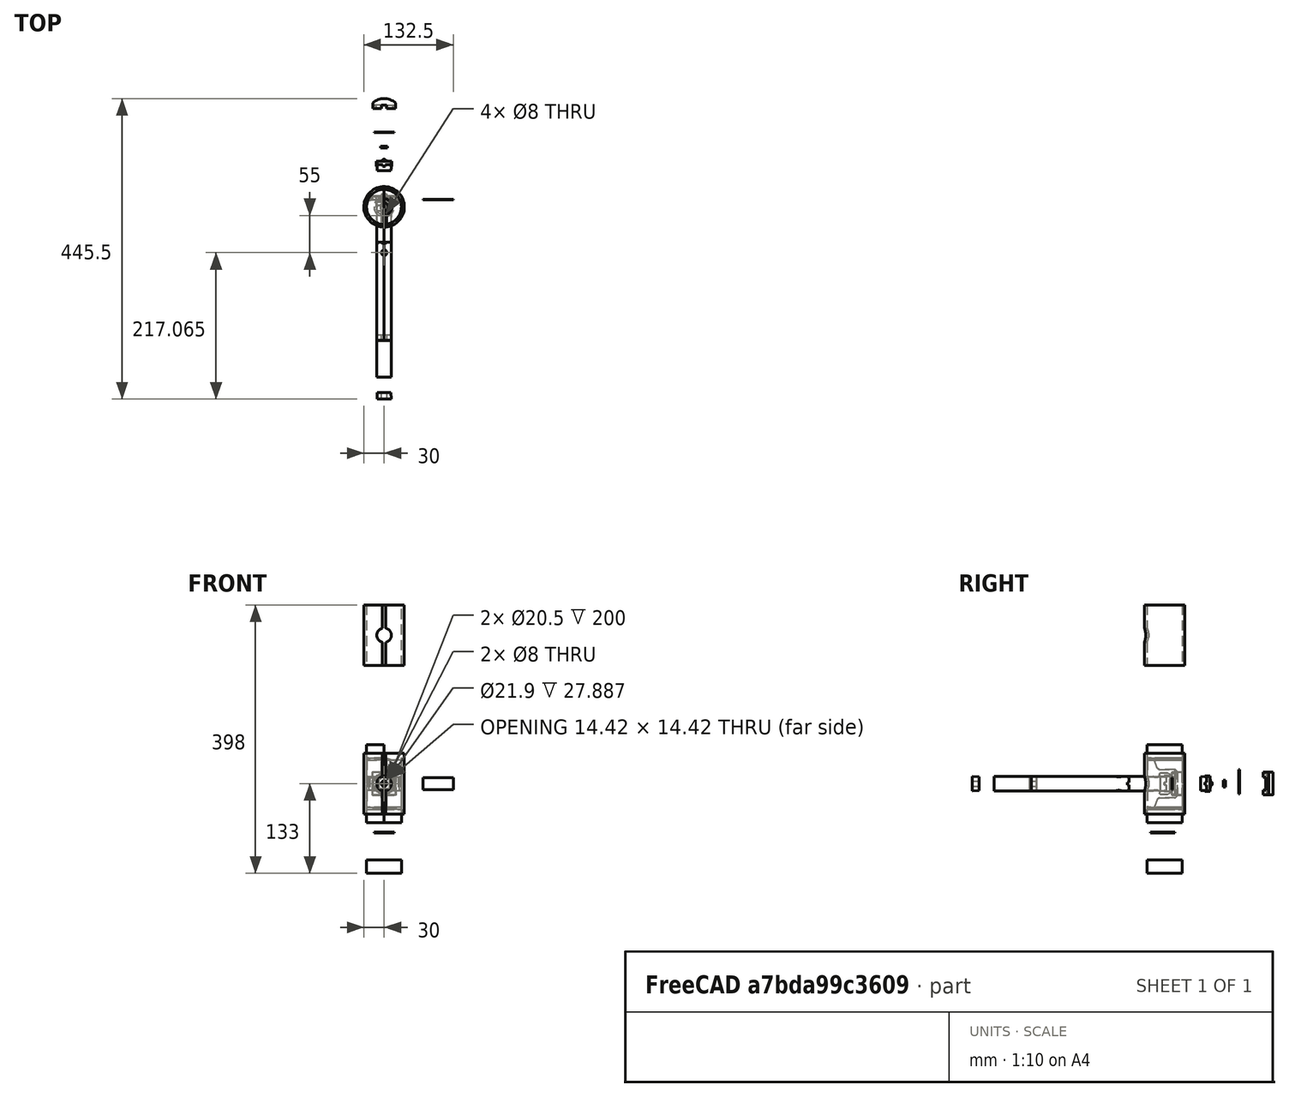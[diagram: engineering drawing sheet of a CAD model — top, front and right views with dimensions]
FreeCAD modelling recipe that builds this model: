
FCSTD DOCUMENT  (FreeCAD 0.21R33771 (Git))
Label: Hammer
License: All rights reserved
LicenseURL: https://en.wikipedia.org/wiki/All_rights_reserved
objects: Sketcher::SketchObject×52, PartDesign::Pad×26, PartDesign::Pocket×26, PartDesign::Body×26, TechDraw::DrawViewDimension×19, TechDraw::DrawProjGroupItem×18, PartDesign::Chamfer×14, App::Link×13, App::DocumentObjectGroupPython×13, Part::Feature×12, TechDraw::DrawViewBalloon×12, TechDraw::DrawSVGTemplate×7, TechDraw::DrawProjGroup×7, TechDraw::DrawPage×7, PartDesign::FeatureBase×6, PartDesign::AdditiveCone×4, PartDesign::Fillet×4, Spreadsheet::Sheet×3, App::DocumentObjectGroup×3, PartDesign::Draft×2, +6 more types
note: 276 computed .brp shape members not serialized (recipe doc carries the construction recipe); baked Part::Feature solids carry a one-line shape summary decoded from their .brp

FEATURE [Spreadsheet::Sheet] Spreadsheet  label="Properties"
  cells = A1='PropertyName; B1='Value; A2='Handle_OD; B2(Handle_OD)=21.5; A3='Head_ID; B3(Head_ID)=51.4; A4='Head_Len; B4(Handle_Len)=110; A5='Clearance; B5(Clearance)=0.2; A6='Inset_Len; B6(Insert_Len)=70; A7='Sensor_Wire_Track_Width; B7(Sensor_Wire_Track_Width)=8; A8='Spring_Plate_Len; B8(Spring_Plate_Len)=46; A9='Sensor_Diameter; B9(Sensor_Diameter)=30; A10='Handle_ID; B10(Handle_ID)=20.5
FEATURE [Sketcher::SketchObject] Sketch  label="base"
  FullyConstrained = true
  MapMode = 5
  Support = -> [XY_Plane001]
  expr: Constraints[1] = <<Properties>>.Head_ID
  sketch-geometry (1):
    g0: Circle CenterX=0 CenterY=0 CenterZ=0 NormalX=0 NormalY=0 NormalZ=1 AngleXU=0 Radius=25.7
  constraints (2):
    c: Coincident(g0,g-1)
    c: Diameter(g0) = 51.4
FEATURE [PartDesign::Pad] Pad  label="Base"
  Direction = (0,0,1)
  Length = 35
  Length2 = 35
  Profile = -> Sketch
  ReferenceAxis = -> Sketch [N_Axis]
  Type = 4
  expr: Length = <<Properties>>.Insert_Len / 2
  expr: Length2 = <<Properties>>.Insert_Len / 2
FEATURE [Sketcher::SketchObject] Sketch001  label="sensor_wire_slot"
  FullyConstrained = true
  MapMode = 5
  Support = -> [XY_Plane001]
  expr: Constraints[11] = <<Properties>>.Sensor_Wire_Track_Width
  expr: Constraints[1] = Sketch.Constraints[1]
  sketch-geometry (7):
    g0: Circle CenterX=0 CenterY=0 CenterZ=0 NormalX=0 NormalY=0 NormalZ=1 AngleXU=0 Radius=25.7
    g1: LineSegment StartX=-4 StartY=-25.3868 StartZ=0 EndX=-4 EndY=-14.4568 EndZ=0
    g2: LineSegment StartX=-4 StartY=-14.4568 StartZ=0 EndX=4 EndY=-14.4568 EndZ=0
    g3: LineSegment StartX=4 StartY=-14.4568 StartZ=0 EndX=4 EndY=-25.3868 EndZ=0
    g4: ArcOfCircle CenterX=0 CenterY=0 CenterZ=0 NormalX=0 NormalY=0 NormalZ=1 AngleXU=0 Radius=25.7 StartAngle=4.55611 EndAngle=4.86867
    g5: GeomPoint X=0 Y=-14.4568 Z=0
    g6: Circle CenterX=0 CenterY=0 CenterZ=0 NormalX=0 NormalY=0 NormalZ=1 AngleXU=0 Radius=15
  constraints (17):
    c: Coincident(g0,g-1)
    c: Diameter(g0) = 51.4
    c: Vertical(g1)
    c: Coincident(g2,g1)
    c: Horizontal(g2)
    c: Coincident(g3,g2)
    c: Vertical(g3)
    c: Coincident(g4,g0)
    c: Coincident(g4,g1)
    c: Coincident(g4,g3)
    c: PointOnObject(g3,g0)
    c: DistanceX(g2,g2) = 8
    c: Symmetric(g2,g2,g5)
    c: PointOnObject(g5,g-2)
    c: Coincident(g6,g4)
    c: Diameter(g6) = 30
    c: PointOnObject(g2,g6)
FEATURE [PartDesign::Pocket] Pocket  label="Sensor_Wire_Slot"
  BaseFeature = -> Pad
  Direction = (0,0,-1)
  Length = 35
  Length2 = 35
  Profile = -> Sketch001
  ReferenceAxis = -> Sketch001 [N_Axis]
  Type = 4
  expr: Length = <<Properties>>.Insert_Len / 2
  expr: Length2 = <<Properties>>.Insert_Len / 2
FEATURE [Sketcher::SketchObject] Sketch002  label="handle_hole"
  FullyConstrained = true
  MapMode = 5
  Placement = pos=(0,0,0) rot=(1,0,0;1.5708rad)
  Support = -> [XZ_Plane001]
  expr: Constraints[1] = <<Properties>>.Handle_OD + <<Properties>>.Clearance * 2
  sketch-geometry (1):
    g0: Circle CenterX=0 CenterY=0 CenterZ=0 NormalX=0 NormalY=0 NormalZ=1 AngleXU=0 Radius=10.95
  constraints (2):
    c: Coincident(g0,g-1)
    c: Diameter(g0) = 21.9
FEATURE [PartDesign::Pocket] Pocket001  label="Handle_hole"
  BaseFeature = -> Pocket
  Direction = (0,1,2e-16)
  Length = 25.7
  Length2 = 25.7
  Profile = -> Sketch002
  ReferenceAxis = -> Sketch002 [N_Axis]
  Type = 4
  expr: Length = <<Properties>>.Head_ID / 2
  expr: Length2 = <<Properties>>.Head_ID / 2
FEATURE [Sketcher::SketchObject] Sketch004  label="top_sensor_hole"
  FullyConstrained = true
  MapMode = 5
  Placement = pos=(0,0,0) rot=(0.57735,0.57735,0.57735;2.0944rad)
  Support = -> [YZ_Plane001]
  expr: Constraints[20] = <<Properties>>.Head_ID
  expr: Constraints[7] = <<Properties>>.Sensor_Diameter + 4
  sketch-geometry (9):
    g0: LineSegment StartX=-25.7 StartY=-17 StartZ=0 EndX=-25.7 EndY=17 EndZ=0
    g1: LineSegment StartX=25.7 StartY=17 StartZ=0 EndX=25.7 EndY=-17 EndZ=0
    g2: LineSegment StartX=25.7 StartY=-17 StartZ=0 EndX=-25.7 EndY=-17 EndZ=0
    g3: GeomPoint X=0 Y=0 Z=0
    g4: LineSegment StartX=10.5 StartY=17 StartZ=0 EndX=25.7 EndY=17 EndZ=0
    g5: LineSegment StartX=25.7 StartY=17 StartZ=0 EndX=25.7 EndY=-17 EndZ=0
    g6: LineSegment StartX=25.7 StartY=-17 StartZ=0 EndX=10.5 EndY=-17 EndZ=0
    g7: LineSegment StartX=10.5 StartY=-17 StartZ=0 EndX=10.5 EndY=17 EndZ=0
    g8: LineSegment StartX=-25.7 StartY=17 StartZ=0 EndX=25.7 EndY=17 EndZ=0
  constraints (23):
    c: Coincident(g1,g2)
    c: Coincident(g2,g0)
    c: Horizontal(g2)
    c: Vertical(g0)
    c: Vertical(g1)
    c: Symmetric(g1,g0,g3)
    c: Coincident(g3,g-1)
    c: DistanceY(g1,g1) = 34
    c: Coincident(g4,g5)
    c: Coincident(g5,g6)
    c: Coincident(g6,g7)
    c: Horizontal(g4)
    c: Horizontal(g6)
    c: Vertical(g5)
    c: Vertical(g7)
    c: PointOnObject(g5,g2)
    c: Coincident(g7,g4)
    c: Coincident(g8,g0)
    c: Coincident(g8,g1)
    c: Horizontal(g8)
    c: DistanceX(g8,g8) = 51.4
    c: Coincident(g4,g1)
    c: DistanceX(g3,g4) = 10.5
FEATURE [PartDesign::Pocket] Pocket002  label="Top_Sensor_Hole"
  BaseFeature = -> Pocket001
  Direction = (-1,2e-16,-3e-16)
  Length = 17
  Length2 = 17
  Profile = -> Sketch004
  ReferenceAxis = -> Sketch004 [N_Axis]
  Type = 4
  expr: Length = <<Properties>>.Sensor_Diameter / 2 + 2
  expr: Length2 = <<Properties>>.Sensor_Diameter / 2 + 2
FEATURE [PartDesign::Chamfer] Chamfer
  Angle = 70
  Base = -> Pocket002 [Edge30,Edge32]
  BaseFeature = -> Pocket002
  ChamferType = 2
  FlipDirection = false
  Size = 8
  Size2 = 1
  SupportTransform = false
  UseAllEdges = false
FEATURE [Sketcher::SketchObject] Sketch003  label="spring_plate_slot"
  FullyConstrained = true
  MapMode = 5
  Support = -> [XY_Plane001]
  expr: Constraints[1] = Sketch.Constraints[1]
  expr: Constraints[3] = <<Properties>>.Sensor_Diameter + <<Properties>>.Clearance * 2
  expr: Constraints[7] = <<Properties>>.Spring_Plate_Len
  sketch-geometry (15):
    g0: Circle CenterX=0 CenterY=0 CenterZ=0 NormalX=0 NormalY=0 NormalZ=1 AngleXU=0 Radius=25.7
    g1: LineSegment StartX=-15.2 StartY=15.4669 StartZ=0 EndX=15.2 EndY=15.4669 EndZ=0
    g2: GeomPoint X=0 Y=15.4669 Z=0
    g3: LineSegment StartX=-23 StartY=11.4669 StartZ=0 EndX=23 EndY=11.4669 EndZ=0
    g4: GeomPoint X=0 Y=11.4669 Z=0
    g5: LineSegment StartX=-15.2 StartY=15.4669 StartZ=0 EndX=-21 EndY=11.4669 EndZ=0
    g6: LineSegment StartX=15.2 StartY=15.4669 StartZ=0 EndX=21 EndY=11.4669 EndZ=0
    g7: LineSegment StartX=21 StartY=11.4669 StartZ=0 EndX=23 EndY=11.4669 EndZ=0
    g8: LineSegment StartX=-21 StartY=11.4669 StartZ=0 EndX=-23 EndY=11.4669 EndZ=0
    g9: ArcOfCircle CenterX=0 CenterY=0 CenterZ=0 NormalX=0 NormalY=0 NormalZ=1 AngleXU=0 Radius=25.7 StartAngle=2.6791 EndAngle=2.80587
    g10: ArcOfCircle CenterX=0 CenterY=0 CenterZ=0 NormalX=0 NormalY=0 NormalZ=1 AngleXU=0 Radius=25.7 StartAngle=0.335723 EndAngle=0.462496
    g11: LineSegment StartX=-11 StartY=10.5 StartZ=0 EndX=-24.2652 EndY=8.46691 EndZ=0
    g12: LineSegment StartX=11 StartY=10.5 StartZ=0 EndX=24.2652 EndY=8.46691 EndZ=0
    g13: LineSegment StartX=11 StartY=10.5 StartZ=0 EndX=-11 EndY=10.5 EndZ=0
    g14: GeomPoint X=0 Y=10.5 Z=0
  constraints (39):
    c: Coincident(g0,g-1)
    c: Diameter(g0) = 51.4
    c: Horizontal(g1)
    c: DistanceX(g1,g1) = 30.4
    c: Symmetric(g1,g1,g2)
    c: PointOnObject(g2,g-2)
    c: Horizontal(g3)
    c: DistanceX(g3,g3) = 46
    c: Symmetric(g3,g3,g4)
    c: PointOnObject(g4,g-2)
    c: Coincident(g5,g1)
    c: PointOnObject(g5,g3)
    c: Coincident(g6,g1)
    c: PointOnObject(g6,g3)
    c: Coincident(g7,g6)
    c: PointOnObject(g7,g0)
    c: Horizontal(g7)
    c: Coincident(g8,g5)
    c: PointOnObject(g8,g0)
    c: Horizontal(g8)
    c: Equal(g8,g7)
    c: PointOnObject(g3,g0)
    c: DistanceY(g6,g1) = 4
    c: DistanceX(g6,g7) = 2
    c: Coincident(g9,g0)
    c: Coincident(g9,g8)
    c: Coincident(g10,g9)
    c: Coincident(g10,g7)
    c: Coincident(g13,g12)
    c: Coincident(g13,g11)
    c: Horizontal(g13)
    c: Coincident(g10,g12)
    c: Coincident(g9,g11)
    c: DistanceX(g12,g6) = 10
    c: Equal(g12,g11)
    c: DistanceY(g10,g7) = 3
    c: Symmetric(g13,g13,g14)
    c: PointOnObject(g14,g-2)
    c: DistanceY(g9,g14) = 10.5
FEATURE [PartDesign::Pocket] Pocket003  label="Spring_Plate_Slot"
  BaseFeature = -> Chamfer
  Direction = (0,0,-1)
  Length = 10
  Length2 = 10
  Profile = -> Sketch003
  ReferenceAxis = -> Sketch003 [N_Axis]
  Type = 4
FEATURE [PartDesign::Chamfer] Chamfer001
  Angle = 45
  Base = -> Pocket003 [Edge43,Edge46,Edge45,Edge47,Edge44,Edge42]
  BaseFeature = -> Pocket003
  ChamferType = 0
  FlipDirection = false
  Size = 0.5
  Size2 = 1
  SupportTransform = false
  UseAllEdges = false
FEATURE [Sketcher::SketchObject] Sketch005  label="top_sens_base"
  FullyConstrained = true
  MapMode = 5
  Support = -> [XY_Plane]
  expr: Constraints[18] = <<Properties>>.Clearance
  expr: Constraints[1] = <<Properties>>.Head_ID
  expr: Constraints[3] = 34 - <<Properties>>.Clearance * 2
  expr: Constraints[6] = 10.5 + <<Properties>>.Clearance
  sketch-geometry (8):
    g0: Circle CenterX=0 CenterY=0 CenterZ=0 NormalX=0 NormalY=0 NormalZ=1 AngleXU=0 Radius=25.7
    g1: LineSegment StartX=-16.8 StartY=10.7 StartZ=0 EndX=16.8 EndY=10.7 EndZ=0
    g2: GeomPoint X=0 Y=10.7 Z=0
    g3: LineSegment StartX=-16.8 StartY=10.7 StartZ=0 EndX=-16.8 EndY=19.1836 EndZ=0
    g4: LineSegment StartX=16.8 StartY=10.7 StartZ=0 EndX=16.8 EndY=19.1836 EndZ=0
    g5: GeomPoint X=0 Y=25.7 Z=0
    g6: ArcOfCircle CenterX=0 CenterY=0 CenterZ=0 NormalX=0 NormalY=0 NormalZ=1 AngleXU=0 Radius=25.5 StartAngle=0.851542 EndAngle=2.29005
    g7: GeomPoint X=0 Y=25.5 Z=0
  constraints (19):
    c: Coincident(g0,g-1)
    c: Diameter(g0) = 51.4
    c: Horizontal(g1)
    c: DistanceX(g1,g1) = 33.6
    c: Symmetric(g1,g1,g2)
    c: PointOnObject(g2,g-2)
    c: DistanceY(g0,g2) = 10.7
    c: Coincident(g3,g1)
    c: Vertical(g3)
    c: Vertical(g4)
    c: Coincident(g4,g1)
    c: PointOnObject(g5,g0)
    c: PointOnObject(g5,g-2)
    c: Coincident(g6,g0)
    c: Coincident(g6,g3)
    c: Coincident(g6,g4)
    c: PointOnObject(g7,g6)
    c: PointOnObject(g7,g-2)
    c: DistanceY(g7,g5) = 0.2
FEATURE [PartDesign::Pad] Pad001  label="Top_Base"
  Direction = (0,0,1)
  Length = 16.8
  Length2 = 16.8
  Profile = -> Sketch005
  ReferenceAxis = -> Sketch005 [N_Axis]
  Type = 4
  expr: Length = <<Properties>>.Sensor_Diameter / 2 + 2 - <<Properties>>.Clearance
  expr: Length2 = <<Properties>>.Sensor_Diameter / 2 + 2 - <<Properties>>.Clearance
FEATURE [Sketcher::SketchObject] Sketch006
  FullyConstrained = true
  MapMode = 5
  Support = -> [XY_Plane]
  expr: Constraints[1] = Sketch003.Constraints[1]
  expr: Constraints[22] = Sketch003.Constraints[22]
  expr: Constraints[23] = Sketch003.Constraints[23]
  expr: Constraints[33] = Sketch003.Constraints[33]
  expr: Constraints[35] = Sketch003.Constraints[35]
  expr: Constraints[38] = Sketch003.Constraints[38]
  expr: Constraints[3] = Sketch003.Constraints[3]
  expr: Constraints[7] = Sketch003.Constraints[7]
  sketch-geometry (15):
    g0: Circle CenterX=0 CenterY=0 CenterZ=0 NormalX=0 NormalY=0 NormalZ=1 AngleXU=0 Radius=25.7
    g1: LineSegment StartX=-15.2 StartY=15.4669 StartZ=0 EndX=15.2 EndY=15.4669 EndZ=0
    g2: GeomPoint X=0 Y=15.4669 Z=0
    g3: LineSegment StartX=-23 StartY=11.4669 StartZ=0 EndX=23 EndY=11.4669 EndZ=0
    g4: GeomPoint X=0 Y=11.4669 Z=0
    g5: LineSegment StartX=-15.2 StartY=15.4669 StartZ=0 EndX=-21 EndY=11.4669 EndZ=0
    g6: LineSegment StartX=15.2 StartY=15.4669 StartZ=0 EndX=21 EndY=11.4669 EndZ=0
    g7: LineSegment StartX=21 StartY=11.4669 StartZ=0 EndX=23 EndY=11.4669 EndZ=0
    g8: LineSegment StartX=-21 StartY=11.4669 StartZ=0 EndX=-23 EndY=11.4669 EndZ=0
    g9: ArcOfCircle CenterX=0 CenterY=0 CenterZ=0 NormalX=0 NormalY=0 NormalZ=1 AngleXU=0 Radius=25.7 StartAngle=2.6791 EndAngle=2.80587
    g10: ArcOfCircle CenterX=0 CenterY=0 CenterZ=0 NormalX=0 NormalY=0 NormalZ=1 AngleXU=0 Radius=25.7 StartAngle=0.335723 EndAngle=0.462496
    g11: LineSegment StartX=-11 StartY=10.5 StartZ=0 EndX=-24.2652 EndY=8.46691 EndZ=0
    g12: LineSegment StartX=11 StartY=10.5 StartZ=0 EndX=24.2652 EndY=8.46691 EndZ=0
    g13: LineSegment StartX=11 StartY=10.5 StartZ=0 EndX=-11 EndY=10.5 EndZ=0
    g14: GeomPoint X=0 Y=10.5 Z=0
  constraints (40):
    c: Coincident(g0,g-1)
    c: Diameter(g0) = 51.4
    c: Horizontal(g1)
    c: DistanceX(g1,g1) = 30.4
    c: Symmetric(g1,g1,g2)
    c: PointOnObject(g2,g-2)
    c: Horizontal(g3)
    c: DistanceX(g3,g3) = 46
    c: Symmetric(g3,g3,g4)
    c: PointOnObject(g4,g-2)
    c: Coincident(g5,g1)
    c: PointOnObject(g5,g3)
    c: Coincident(g6,g1)
    c: PointOnObject(g6,g3)
    c: Coincident(g7,g6)
    c: PointOnObject(g7,g0)
    c: Horizontal(g7)
    c: Coincident(g8,g5)
    c: PointOnObject(g8,g0)
    c: Horizontal(g8)
    c: Equal(g8,g7)
    c: PointOnObject(g3,g0)
    c: DistanceY(g6,g1) = 4
    c: DistanceX(g6,g7) = 2
    c: Coincident(g9,g0)
    c: Coincident(g9,g8)
    c: Coincident(g10,g9)
    c: Coincident(g10,g7)
    c: Coincident(g13,g12)
    c: Coincident(g13,g11)
    c: Horizontal(g13)
    c: Coincident(g10,g12)
    c: Coincident(g9,g11)
    c: DistanceX(g12,g6) = 10
    c: Equal(g12,g11)
    c: DistanceY(g10,g7) = 3
    c: Symmetric(g13,g13,g14)
    c: PointOnObject(g14,g-2)
    c: DistanceY(g9,g14) = 10.5
    c: DistanceY(g9,g2) = 15.4669
FEATURE [PartDesign::Pocket] Pocket004
  BaseFeature = -> Pad001
  Direction = (0,0,-1)
  Length = 9.5
  Length2 = 9.5
  Profile = -> Sketch006
  ReferenceAxis = -> Sketch006 [N_Axis]
  Type = 4
FEATURE [PartDesign::Chamfer] Chamfer002
  Angle = 45
  Base = -> Pocket004 [Edge22,Edge12]
  BaseFeature = -> Pocket004
  ChamferType = 0
  FlipDirection = false
  Size = 0.3
  Size2 = 1
  SupportTransform = false
  UseAllEdges = false
FEATURE [Sketcher::SketchObject] Sketch007
  FullyConstrained = true
  MapMode = 5
  Placement = pos=(0,0,0) rot=(1,0,0;1.5708rad)
  Support = -> [XZ_Plane]
  expr: Constraints[11] = <<Properties>>.Sensor_Wire_Track_Width
  expr: Constraints[1] = <<Properties>>.Sensor_Diameter + 1
  expr: Constraints[27] = <<Properties>>.Sensor_Wire_Track_Width
  sketch-geometry (11):
    g0: Circle CenterX=0 CenterY=0 CenterZ=0 NormalX=0 NormalY=0 NormalZ=1 AngleXU=0 Radius=15.5
    g1: LineSegment StartX=-4 StartY=14.975 StartZ=0 EndX=-4 EndY=27.305 EndZ=0
    g2: LineSegment StartX=-4 StartY=27.305 StartZ=0 EndX=4 EndY=27.305 EndZ=0
    g3: LineSegment StartX=4 StartY=27.305 StartZ=0 EndX=4 EndY=14.975 EndZ=0
    g4: GeomPoint X=0 Y=27.305 Z=0
    g5: LineSegment StartX=-4 StartY=-14.975 StartZ=0 EndX=-4 EndY=-27.305 EndZ=0
    g6: LineSegment StartX=-4 StartY=-27.305 StartZ=0 EndX=4 EndY=-27.305 EndZ=0
    g7: LineSegment StartX=4 StartY=-27.305 StartZ=0 EndX=4 EndY=-14.975 EndZ=0
    g8: GeomPoint X=0 Y=-27.305 Z=0
    g9: ArcOfCircle CenterX=0 CenterY=0 CenterZ=0 NormalX=0 NormalY=0 NormalZ=1 AngleXU=0 Radius=15.5 StartAngle=1.83181 EndAngle=4.45137
    g10: ArcOfCircle CenterX=0 CenterY=0 CenterZ=0 NormalX=0 NormalY=0 NormalZ=1 AngleXU=0 Radius=15.5 StartAngle=4.97341 EndAngle=7.59296
  constraints (28):
    c: Coincident(g0,g-1)
    c: Diameter(g0) = 31
    c: PointOnObject(g1,g0)
    c: Vertical(g1)
    c: Coincident(g2,g1)
    c: Horizontal(g2)
    c: Coincident(g3,g2)
    c: PointOnObject(g3,g0)
    c: Vertical(g3)
    c: Symmetric(g2,g2,g4)
    c: PointOnObject(g4,g-2)
    c: DistanceX(g2,g2) = 8
    c: DistanceY(g3,g3) = 12.33
    c: Vertical(g5)
    c: Coincident(g6,g5)
    c: Horizontal(g6)
    c: Coincident(g7,g6)
    c: Vertical(g7)
    c: Symmetric(g6,g6,g8)
    c: PointOnObject(g8,g-2)
    c: Equal(g7,g3)
    c: Coincident(g9,g0)
    c: Coincident(g9,g1)
    c: Coincident(g9,g5)
    c: Coincident(g10,g9)
    c: Coincident(g10,g3)
    c: Coincident(g10,g7)
    c: DistanceX(g6,g6) = 8
FEATURE [PartDesign::Pocket] Pocket005
  BaseFeature = -> Chamfer002
  Direction = (0,1,2e-16)
  Length = 0
  Length2 = 5
  Offset = 0.4
  Profile = -> Sketch007
  ReferenceAxis = -> Sketch007 [N_Axis]
  Type = 3
  UpToFace = -> Chamfer002 [Face11]
FEATURE [PartDesign::Body] Body001  label="TopSensor"
  Group = -> [Sketch005,Pad001,Sketch006,Pocket004,Chamfer002,Sketch007,Pocket005]
  Origin = -> Origin
  Tip = -> Pocket005
FEATURE [Sketcher::SketchObject] Sketch008
  FullyConstrained = true
  MapMode = 5
  Placement = pos=(0,0,0) rot=(0.57735,0.57735,0.57735;2.0944rad)
  Support = -> [YZ_Plane001]
  expr: Constraints[16] = <<Properties>>.Sensor_Diameter + 2
  sketch-geometry (14):
    g0: LineSegment StartX=15.5 StartY=21 StartZ=0 EndX=15.5 EndY=-21 EndZ=0
    g1: LineSegment StartX=15.5 StartY=-21 StartZ=0 EndX=-19.02 EndY=-21 EndZ=0
    g2: LineSegment StartX=-19.02 StartY=-21 StartZ=0 EndX=-19.02 EndY=-16 EndZ=0
    g3: LineSegment StartX=-19.02 StartY=-16 StartZ=0 EndX=10.5 EndY=-16 EndZ=0
    g4: LineSegment StartX=10.5 StartY=-16 StartZ=0 EndX=10.5 EndY=16 EndZ=0
    g5: LineSegment StartX=10.5 StartY=16 StartZ=0 EndX=-19.02 EndY=16 EndZ=0
    g6: LineSegment StartX=-19.02 StartY=16 StartZ=0 EndX=-19.02 EndY=21 EndZ=0
    g7: LineSegment StartX=-19.02 StartY=21 StartZ=0 EndX=15.5 EndY=21 EndZ=0
    g8: GeomPoint X=10.5 Y=0 Z=0
    g9: GeomPoint X=15.5 Y=0 Z=0
    g10: GeomPoint X=15.5 Y=21 Z=0
    g11: GeomPoint X=15.5 Y=-21 Z=0
    g12: GeomPoint X=10.5 Y=16 Z=0
    g13: GeomPoint X=10.5 Y=-16 Z=0
  constraints (30):
    c: Vertical(g0)
    c: Horizontal(g1)
    c: Coincident(g2,g1)
    c: Vertical(g2)
    c: Coincident(g3,g2)
    c: Horizontal(g3)
    c: Vertical(g4)
    c: Horizontal(g5)
    c: Coincident(g6,g5)
    c: Vertical(g6)
    c: Coincident(g7,g6)
    c: Horizontal(g7)
    c: Symmetric(g10,g11,g9)
    c: Symmetric(g13,g12,g8)
    c: PointOnObject(g8,g-1)
    c: PointOnObject(g9,g-1)
    c: DistanceY(g13,g12) = 32
    c: DistanceY(g6,g6) = 5
    c: DistanceX(g8,g9) = 5
    c: DistanceX(g-1,g8) = 10.5
    c: DistanceX(g7,g10) = 34.52
    c: Coincident(g0,g10)
    c: Coincident(g7,g0)
    c: Coincident(g4,g12)
    c: Coincident(g5,g4)
    c: Coincident(g0,g11)
    c: Coincident(g4,g13)
    c: Coincident(g3,g4)
    c: Coincident(g1,g0)
    c: Equal(g3,g5)
FEATURE [PartDesign::Pocket] Pocket006
  BaseFeature = -> Chamfer001
  Direction = (-1,2e-16,-3e-16)
  Length = 4
  Length2 = 4
  Profile = -> Sketch008
  ReferenceAxis = -> Sketch008 [N_Axis]
  Type = 4
  expr: Length = <<Properties>>.Sensor_Wire_Track_Width / 2
  expr: Length2 = <<Properties>>.Sensor_Wire_Track_Width / 2
FEATURE [PartDesign::Chamfer] Chamfer003
  Angle = 65
  Base = -> Pocket006 [Edge148,Edge154]
  BaseFeature = -> Pocket006
  ChamferType = 2
  FlipDirection = false
  Size = 3
  Size2 = 1
  SupportTransform = false
  UseAllEdges = false
FEATURE [PartDesign::Chamfer] Chamfer004
  Angle = 45
  Base = -> Chamfer003 [Edge167,Edge85,Edge52,Edge56]
  BaseFeature = -> Chamfer003
  ChamferType = 0
  FlipDirection = false
  Size = 2
  Size2 = 1
  SupportTransform = false
  UseAllEdges = false
FEATURE [PartDesign::Chamfer] Chamfer005
  Angle = 45
  Base = -> Chamfer004 [Edge169,Edge38]
  BaseFeature = -> Chamfer004
  ChamferType = 1
  FlipDirection = false
  Size = 4
  Size2 = 3.999
  SupportTransform = false
  UseAllEdges = false
FEATURE [Sketcher::SketchObject] Sketch009
  FullyConstrained = true
  MapMode = 5
  Support = -> [XY_Plane002]
  sketch-geometry (2):
    g0: Circle CenterX=0 CenterY=0 CenterZ=0 NormalX=0 NormalY=0 NormalZ=1 AngleXU=0 Radius=26
    g1: Circle CenterX=0 CenterY=0 CenterZ=0 NormalX=0 NormalY=0 NormalZ=1 AngleXU=0 Radius=30
  constraints (4):
    c: Coincident(g0,g-1)
    c: Coincident(g1,g0)
    c: Diameter(g0) = 52
    c: Diameter(g1) = 60
FEATURE [PartDesign::Pad] Pad002
  Direction = (0,0,1)
  Length = 45
  Length2 = 45
  Profile = -> Sketch009
  ReferenceAxis = -> Sketch009 [N_Axis]
  Type = 4
FEATURE [Sketcher::SketchObject] Sketch010
  FullyConstrained = true
  MapMode = 5
  Placement = pos=(0,0,0) rot=(1,0,0;1.5708rad)
  Support = -> [XZ_Plane002]
  expr: Constraints[1] = <<Properties>>.Handle_OD
  sketch-geometry (1):
    g0: Circle CenterX=0 CenterY=0 CenterZ=0 NormalX=0 NormalY=0 NormalZ=1 AngleXU=0 Radius=10.75
  constraints (2):
    c: Coincident(g0,g-1)
    c: Diameter(g0) = 21.5
FEATURE [PartDesign::Pocket] Pocket007
  BaseFeature = -> Pad002
  Direction = (0,1,2e-16)
  Length = 5
  Length2 = 5
  Profile = -> Sketch010
  ReferenceAxis = -> Sketch010 [N_Axis]
  Reversed = true
  Type = 1
FEATURE [Sketcher::SketchObject] Sketch011
  FullyConstrained = true
  MapMode = 5
  Placement = pos=(0,0,0) rot=(1,0,0;1.5708rad)
  Support = -> [XZ_Plane003]
  expr: Constraints[3] = <<Properties>>.Handle_ID
  sketch-geometry (2):
    g0: Circle CenterX=0 CenterY=0 CenterZ=0 NormalX=0 NormalY=0 NormalZ=1 AngleXU=0 Radius=10.625
    g1: Circle CenterX=0 CenterY=0 CenterZ=0 NormalX=0 NormalY=0 NormalZ=1 AngleXU=0 Radius=10.25
  constraints (4):
    c: Coincident(g0,g-1)
    c: Diameter(g0) = 21.25
    c: Coincident(g1,g0)
    c: Diameter(g1) = 20.5
FEATURE [PartDesign::Pad] Pad003
  Direction = (0,-1,-2e-16)
  Length = 200
  Length2 = 10
  Placement = pos=(0,0,0) rot=(1,0,0;1.5708rad)
  Profile = -> Sketch011
  ReferenceAxis = -> Sketch011 [N_Axis]
  Type = 0
FEATURE [Sketcher::SketchObject] Sketch014
  FullyConstrained = true
  MapMode = 5
  Support = -> [XY_Plane005]
  sketch-geometry (5):
    g0: ArcOfCircle CenterX=0 CenterY=0 CenterZ=0 NormalX=0 NormalY=0 NormalZ=1 AngleXU=0 Radius=15 StartAngle=4.90695 EndAngle=10.801
    g1: LineSegment StartX=2.9 StartY=-14.717 StartZ=0 EndX=2.9 EndY=-20.717 EndZ=0
    g2: LineSegment StartX=2.9 StartY=-20.717 StartZ=0 EndX=-2.9 EndY=-20.717 EndZ=0
    g3: LineSegment StartX=-2.9 StartY=-20.717 StartZ=0 EndX=-2.9 EndY=-14.717 EndZ=0
    g4: LineSegment StartX=2.9 StartY=-14.717 StartZ=0 EndX=-2.9 EndY=-14.717 EndZ=0
  constraints (14):
    c: Coincident(g0,g-1)
    c: Radius(g0) = 15
    c: Coincident(g1,g0)
    c: Vertical(g1)
    c: Coincident(g2,g1)
    c: Horizontal(g2)
    c: Coincident(g3,g2)
    c: Coincident(g3,g0)
    c: Vertical(g3)
    c: DistanceX(g2,g2) = 5.8
    c: Coincident(g4,g0)
    c: Coincident(g4,g0)
    c: Horizontal(g4)
    c: DistanceY(g1,g1) = 6
FEATURE [PartDesign::Pad] Pad007
  Direction = (0,0,1)
  Length = 1
  Length2 = 10
  Profile = -> Sketch014
  ReferenceAxis = -> Sketch014 [N_Axis]
  Type = 0
FEATURE [PartDesign::Body] Body005  label="Sensor1"
  Group = -> [Sketch014,Pad007]
  Origin = -> Origin005
  Placement = pos=(0,0,37) rot=(0,0,1;0rad)
  Tip = -> Pad007
FEATURE [PartDesign::FeatureBase] Clone
  BaseFeature = -> Body005
FEATURE [PartDesign::Body] Body006  label="Sensor2"
  Group = -> [Clone]
  Origin = -> Origin006
  Placement = pos=(0,0,-37) rot=(0,1,0;3.14159rad)
  Tip = -> Clone
FEATURE [PartDesign::FeatureBase] Clone001
  BaseFeature = -> Body005
FEATURE [PartDesign::Body] Body007  label="Sensor3"
  Group = -> [Clone001]
  Origin = -> Origin007
  Placement = pos=(0,16,-4e-15) rot=(0,0.707107,-0.707107;3.14159rad)
  Tip = -> Clone001
FEATURE [PartDesign::AdditiveCone] Cone
  Angle = 360
  AttacherType = Attacher::AttachEngine3D
  BaseFeature = -> Chamfer005
  Height = 1.5
  MapMode = 5
  Placement = pos=(0,0,35) rot=(0,0,1;0rad)
  Radius1 = 12
  Radius2 = 6
  Support = -> [Chamfer005]
FEATURE [PartDesign::AdditiveCone] Cone001
  Angle = 360
  AttacherType = Attacher::AttachEngine3D
  BaseFeature = -> Cone
  Height = 1.5
  MapMode = 5
  Placement = pos=(0,0,-35) rot=(1,0,0;3.14159rad)
  Radius1 = 12
  Radius2 = 6
  Support = -> [Cone]
FEATURE [Sketcher::SketchObject] Sketch015
  FullyConstrained = true
  MapMode = 5
  Support = -> [XY_Plane008]
  sketch-geometry (1):
    g0: Circle CenterX=0 CenterY=0 CenterZ=0 NormalX=0 NormalY=0 NormalZ=1 AngleXU=0 Radius=26
  constraints (2):
    c: Coincident(g0,g-1)
    c: Diameter(g0) = 52
FEATURE [PartDesign::Pad] Pad008
  Direction = (0,0,1)
  Length = 20
  Length2 = 10
  Profile = -> Sketch015
  ReferenceAxis = -> Sketch015 [N_Axis]
  Type = 0
FEATURE [PartDesign::Body] Body008  label="Foam1"
  Group = -> [Sketch015,Pad008]
  Origin = -> Origin008
  Placement = pos=(0,0,38) rot=(0,0,1;0rad)
  Tip = -> Pad008
FEATURE [PartDesign::FeatureBase] Clone002
  BaseFeature = -> Body008
  Placement = pos=(0,0,38) rot=(0,0,1;0rad)
FEATURE [PartDesign::Body] Body009  label="Foam2"
  Group = -> [Clone002]
  Origin = -> Origin009
  Placement = pos=(0,0,0) rot=(1,0,0;3.14159rad)
  Tip = -> Clone002
FEATURE [Sketcher::SketchObject] Sketch016
  FullyConstrained = true
  MapMode = 5
  Support = -> [XY_Plane010]
  sketch-geometry (5):
    g0: LineSegment StartX=-22.5 StartY=-0.4 StartZ=0 EndX=-22.5 EndY=0.4 EndZ=0
    g1: LineSegment StartX=-22.5 StartY=0.4 StartZ=0 EndX=22.5 EndY=0.4 EndZ=0
    g2: LineSegment StartX=22.5 StartY=0.4 StartZ=0 EndX=22.5 EndY=-0.4 EndZ=0
    g3: LineSegment StartX=22.5 StartY=-0.4 StartZ=0 EndX=-22.5 EndY=-0.4 EndZ=0
    g4: GeomPoint X=0 Y=0 Z=0
  constraints (12):
    c: Coincident(g0,g1)
    c: Coincident(g1,g2)
    c: Coincident(g2,g3)
    c: Coincident(g3,g0)
    c: Horizontal(g1)
    c: Horizontal(g3)
    c: Vertical(g0)
    c: Vertical(g2)
    c: Symmetric(g1,g0,g4)
    c: Coincident(g4,g-1)
    c: DistanceX(g1,g1) = 45
    c: DistanceY(g2,g2) = 0.8
FEATURE [PartDesign::Pad] Pad009
  Direction = (0,0,1)
  Length = 9
  Length2 = 9
  Profile = -> Sketch016
  ReferenceAxis = -> Sketch016 [N_Axis]
  Type = 4
FEATURE [PartDesign::Body] Body010  label="ShimStock"
  Group = -> [Sketch016,Pad009]
  Origin = -> Origin010
  Placement = pos=(0,11,0) rot=(0,0,1;0rad)
  Tip = -> Pad009
FEATURE [Sketcher::SketchObject] Sketch017
  FullyConstrained = true
  MapMode = 5
  Placement = pos=(0,0,0) rot=(1,0,0;1.5708rad)
  Support = -> [XZ_Plane011]
  sketch-geometry (1):
    g0: Circle CenterX=0 CenterY=0 CenterZ=0 NormalX=0 NormalY=0 NormalZ=1 AngleXU=0 Radius=5
  constraints (2):
    c: Coincident(g0,g-1)
    c: Diameter(g0) = 10
FEATURE [PartDesign::Pad] Pad010
  Direction = (0,-1,-2e-16)
  Length = 3
  Length2 = 10
  Placement = pos=(0,0,0) rot=(1,0,0;1.5708rad)
  Profile = -> Sketch017
  ReferenceAxis = -> Sketch017 [N_Axis]
  Type = 0
FEATURE [PartDesign::Body] Body011  label="TopFoam"
  Group = -> [Sketch017,Pad010]
  Origin = -> Origin011
  Placement = pos=(0,15,0) rot=(0,0,1;0rad)
  Tip = -> Pad010
FEATURE [Sketcher::SketchObject] Sketch018
  FullyConstrained = false
  MapMode = 5
  Support = -> [XY_Plane003]
  sketch-geometry (1):
    g0: Circle CenterX=0 CenterY=-15.4348 CenterZ=0 NormalX=0 NormalY=0 NormalZ=1 AngleXU=0 Radius=4
  constraints (2):
    c: PointOnObject(g0,g-2)
    c: Diameter(g0) = 8
FEATURE [PartDesign::Pocket] Pocket008
  BaseFeature = -> Pad003
  Direction = (0,0,-1)
  Length = 50
  Length2 = 50
  Placement = pos=(0,0,0) rot=(1,0,0;1.5708rad)
  Profile = -> Sketch018
  ReferenceAxis = -> Sketch018 [N_Axis]
  Type = 4
FEATURE [Sketcher::SketchObject] Sketch019
  FullyConstrained = true
  MapMode = 5
  Placement = pos=(0,0,0) rot=(1,0,0;1.5708rad)
  Support = -> [XZ_Plane003]
  sketch-geometry (17):
    g0: LineSegment StartX=12 StartY=-2 StartZ=0 EndX=12 EndY=2 EndZ=0
    g1: LineSegment StartX=12 StartY=2 StartZ=0 EndX=2 EndY=2 EndZ=0
    g2: LineSegment StartX=2 StartY=2 StartZ=0 EndX=2 EndY=12 EndZ=0
    g3: LineSegment StartX=2 StartY=12 StartZ=0 EndX=-2 EndY=12 EndZ=0
    g4: LineSegment StartX=-2 StartY=12 StartZ=0 EndX=-2 EndY=2 EndZ=0
    g5: LineSegment StartX=-2 StartY=2 StartZ=0 EndX=-12 EndY=2 EndZ=0
    g6: LineSegment StartX=-12 StartY=2 StartZ=0 EndX=-12 EndY=-2 EndZ=0
    g7: LineSegment StartX=-12 StartY=-2 StartZ=0 EndX=-2 EndY=-2 EndZ=0
    g8: LineSegment StartX=-2 StartY=-2 StartZ=0 EndX=-2 EndY=-12 EndZ=0
    g9: LineSegment StartX=-2 StartY=-12 StartZ=0 EndX=2 EndY=-12 EndZ=0
    g10: LineSegment StartX=2 StartY=-12 StartZ=0 EndX=2 EndY=-2 EndZ=0
    g11: LineSegment StartX=2 StartY=-2 StartZ=0 EndX=12 EndY=-2 EndZ=0
    g12: LineSegment StartX=-2 StartY=-2 StartZ=0 EndX=-2 EndY=2 EndZ=0
    g13: LineSegment StartX=-2 StartY=2 StartZ=0 EndX=2 EndY=2 EndZ=0
    g14: LineSegment StartX=2 StartY=2 StartZ=0 EndX=2 EndY=-2 EndZ=0
    g15: LineSegment StartX=2 StartY=-2 StartZ=0 EndX=-2 EndY=-2 EndZ=0
    g16: GeomPoint X=0 Y=0 Z=0
  constraints (46):
    c: Vertical(g0)
    c: Coincident(g1,g0)
    c: Horizontal(g1)
    c: Coincident(g2,g1)
    c: Vertical(g2)
    c: Coincident(g3,g2)
    c: Horizontal(g3)
    c: Coincident(g4,g3)
    c: Vertical(g4)
    c: Coincident(g5,g4)
    c: Horizontal(g5)
    c: Coincident(g6,g5)
    c: Vertical(g6)
    c: Horizontal(g7)
    c: Coincident(g8,g7)
    c: Vertical(g8)
    c: Horizontal(g9)
    c: Coincident(g10,g9)
    c: Vertical(g10)
    c: Coincident(g11,g10)
    c: Coincident(g11,g0)
    c: Horizontal(g11)
    c: Equal(g0,g3)
    c: Equal(g3,g6)
    c: Equal(g6,g9)
    c: Coincident(g6,g7)
    c: Coincident(g9,g8)
    c: Equal(g11,g7)
    c: Equal(g11,g1)
    c: Equal(g2,g4)
    c: Equal(g5,g10)
    c: Coincident(g12,g13)
    c: Coincident(g13,g14)
    c: Coincident(g14,g15)
    c: Coincident(g15,g12)
    c: Horizontal(g13)
    c: Horizontal(g15)
    c: Vertical(g12)
    c: Vertical(g14)
    c: Symmetric(g13,g12,g16)
    c: Coincident(g16,g-1)
    c: Coincident(g13,g1)
    c: Coincident(g7,g12)
    c: DistanceX(g13,g13) = 4
    c: DistanceY(g2,g2) = 10
    c: Equal(g10,g2)
FEATURE [PartDesign::Pocket] Pocket009
  BaseFeature = -> Pocket008
  Direction = (0,1,2e-16)
  Length = 3
  Length2 = 5
  Placement = pos=(0,0,0) rot=(1,0,0;1.5708rad)
  Profile = -> Sketch019
  ReferenceAxis = -> Sketch019 [N_Axis]
  Reversed = true
  Type = 0
FEATURE [PartDesign::Body] Body003  label="MetalHandle"
  Group = -> [Sketch011,Pad003,Sketch018,Pocket008,Sketch019,Pocket009]
  Origin = -> Origin003
  Placement = pos=(0,2.5,0) rot=(0,0,1;0rad)
  Tip = -> Pocket009
FEATURE [Sketcher::SketchObject] Sketch020
  FullyConstrained = true
  MapMode = 5
  Placement = pos=(0,0,0) rot=(1,0,0;1.5708rad)
  Support = -> [XZ_Plane012]
  expr: Constraints[43] = Sketch019.Constraints[43]
  expr: Constraints[44] = Sketch019.Constraints[44]
  expr: Constraints[77] = <<Properties>>.Clearance
  expr: Constraints[78] = <<Properties>>.Clearance
  expr: Constraints[79] = <<Properties>>.Clearance
  expr: Constraints[81] = (<<Properties>>.Handle_OD + 2) / 2 - <<Properties>>.Clearance
  sketch-geometry (29):
    g0: LineSegment StartX=12 StartY=-2 StartZ=0 EndX=12 EndY=2 EndZ=0
    g1: LineSegment StartX=12 StartY=2 StartZ=0 EndX=2 EndY=2 EndZ=0
    g2: LineSegment StartX=2 StartY=2 StartZ=0 EndX=2 EndY=12 EndZ=0
    g3: LineSegment StartX=2 StartY=12 StartZ=0 EndX=-2 EndY=12 EndZ=0
    g4: LineSegment StartX=-2 StartY=12 StartZ=0 EndX=-2 EndY=2 EndZ=0
    g5: LineSegment StartX=-2 StartY=2 StartZ=0 EndX=-12 EndY=2 EndZ=0
    g6: LineSegment StartX=-12 StartY=2 StartZ=0 EndX=-12 EndY=-2 EndZ=0
    g7: LineSegment StartX=-12 StartY=-2 StartZ=0 EndX=-2 EndY=-2 EndZ=0
    g8: LineSegment StartX=-2 StartY=-2 StartZ=0 EndX=-2 EndY=-12 EndZ=0
    g9: LineSegment StartX=-2 StartY=-12 StartZ=0 EndX=2 EndY=-12 EndZ=0
    g10: LineSegment StartX=2 StartY=-12 StartZ=0 EndX=2 EndY=-2 EndZ=0
    g11: LineSegment StartX=2 StartY=-2 StartZ=0 EndX=12 EndY=-2 EndZ=0
    g12: LineSegment StartX=-2 StartY=-2 StartZ=0 EndX=-2 EndY=2 EndZ=0
    g13: LineSegment StartX=-2 StartY=2 StartZ=0 EndX=2 EndY=2 EndZ=0
    g14: LineSegment StartX=2 StartY=2 StartZ=0 EndX=2 EndY=-2 EndZ=0
    g15: LineSegment StartX=2 StartY=-2 StartZ=0 EndX=-2 EndY=-2 EndZ=0
    g16: GeomPoint X=0 Y=0 Z=0
    g17: LineSegment StartX=-1.8 StartY=11.55 StartZ=0 EndX=-1.8 EndY=1.8 EndZ=0
    g18: LineSegment StartX=-1.8 StartY=1.8 StartZ=0 EndX=-11.55 EndY=1.8 EndZ=0
    g19: LineSegment StartX=-11.55 StartY=1.8 StartZ=0 EndX=-11.55 EndY=-1.8 EndZ=0
    g20: LineSegment StartX=-11.55 StartY=-1.8 StartZ=0 EndX=-1.8 EndY=-1.8 EndZ=0
    g21: LineSegment StartX=-1.8 StartY=-1.8 StartZ=0 EndX=-1.8 EndY=-11.55 EndZ=0
    g22: LineSegment StartX=-1.8 StartY=-11.55 StartZ=0 EndX=1.8 EndY=-11.55 EndZ=0
    g23: LineSegment StartX=1.8 StartY=-11.55 StartZ=0 EndX=1.8 EndY=-1.8 EndZ=0
    g24: LineSegment StartX=1.8 StartY=-1.8 StartZ=0 EndX=11.55 EndY=-1.8 EndZ=0
    g25: LineSegment StartX=11.55 StartY=-1.8 StartZ=0 EndX=11.55 EndY=1.8 EndZ=0
    g26: LineSegment StartX=11.55 StartY=1.8 StartZ=0 EndX=1.8 EndY=1.8 EndZ=0
    g27: LineSegment StartX=1.8 StartY=1.8 StartZ=0 EndX=1.8 EndY=11.55 EndZ=0
    g28: LineSegment StartX=1.8 StartY=11.55 StartZ=0 EndX=-1.8 EndY=11.55 EndZ=0
  constraints (82):
    c: Vertical(g0)
    c: Coincident(g1,g0)
    c: Horizontal(g1)
    c: Coincident(g2,g1)
    c: Vertical(g2)
    c: Coincident(g3,g2)
    c: Horizontal(g3)
    c: Coincident(g4,g3)
    c: Vertical(g4)
    c: Coincident(g5,g4)
    c: Horizontal(g5)
    c: Coincident(g6,g5)
    c: Vertical(g6)
    c: Horizontal(g7)
    c: Coincident(g8,g7)
    c: Vertical(g8)
    c: Horizontal(g9)
    c: Coincident(g10,g9)
    c: Vertical(g10)
    c: Coincident(g11,g10)
    c: Coincident(g11,g0)
    c: Horizontal(g11)
    c: Equal(g0,g3)
    c: Equal(g3,g6)
    c: Equal(g6,g9)
    c: Coincident(g6,g7)
    c: Coincident(g9,g8)
    c: Equal(g11,g7)
    c: Equal(g11,g1)
    c: Equal(g2,g4)
    c: Equal(g5,g10)
    c: Coincident(g12,g13)
    c: Coincident(g13,g14)
    c: Coincident(g14,g15)
    c: Coincident(g15,g12)
    c: Horizontal(g13)
    c: Horizontal(g15)
    c: Vertical(g12)
    c: Vertical(g14)
    c: Symmetric(g13,g12,g16)
    c: Coincident(g16,g-1)
    c: Coincident(g13,g1)
    c: Coincident(g7,g12)
    c: DistanceX(g13,g13) = 4
    c: DistanceY(g2,g2) = 10
    c: Equal(g10,g2)
    c: Vertical(g17)
    c: Coincident(g18,g17)
    c: Horizontal(g18)
    c: Coincident(g19,g18)
    c: Vertical(g19)
    c: Coincident(g20,g19)
    c: Horizontal(g20)
    c: Coincident(g21,g20)
    c: Vertical(g21)
    c: Coincident(g22,g21)
    c: Horizontal(g22)
    c: Coincident(g23,g22)
    c: Vertical(g23)
    c: Coincident(g24,g23)
    c: Horizontal(g24)
    c: Coincident(g25,g24)
    c: Vertical(g25)
    c: Coincident(g26,g25)
    c: Horizontal(g26)
    c: Coincident(g27,g26)
    c: Vertical(g27)
    c: Coincident(g28,g27)
    c: Coincident(g28,g17)
    c: Horizontal(g28)
    c: Equal(g26,g18)
    c: Equal(g27,g17)
    c: Equal(g26,g24)
    c: Equal(g20,g24)
    c: Equal(g21,g23)
    c: Equal(g23,g27)
    c: Equal(g22,g25)
    c: DistanceX(g26,g1) = 0.2
    c: DistanceY(g26,g1) = 0.2
    c: DistanceY(g0,g24) = 0.2
    c: Equal(g23,g24)
    c: DistanceX(g16,g25) = 11.55
FEATURE [PartDesign::Pad] Pad011
  Direction = (0,-1,2e-16)
  Length = 2.8
  Length2 = 10
  Placement = pos=(0,0,0) rot=(1,0,0;1.5708rad)
  Profile = -> Sketch020
  ReferenceAxis = -> Sketch020 [N_Axis]
  Type = 0
FEATURE [Sketcher::SketchObject] Sketch021
  FullyConstrained = true
  MapMode = 5
  Placement = pos=(0,0,0) rot=(1,0,0;1.5708rad)
  Support = -> [XZ_Plane012]
  expr: Constraints[53] = Sketch020.Constraints[43]
  expr: Constraints[54] = Sketch020.Constraints[44]
  expr: Constraints[87] = Sketch020.Constraints[77]
  expr: Constraints[88] = Sketch020.Constraints[78]
  expr: Constraints[89] = Sketch020.Constraints[79]
  expr: Constraints[91] = Sketch020.Constraints[81]
  sketch-geometry (34):
    g0: LineSegment StartX=11.55 StartY=11.55 StartZ=0 EndX=11.55 EndY=-11.55 EndZ=0
    g1: LineSegment StartX=11.55 StartY=-11.55 StartZ=0 EndX=-11.55 EndY=-11.55 EndZ=0
    g2: LineSegment StartX=-11.55 StartY=-11.55 StartZ=0 EndX=-11.55 EndY=11.55 EndZ=0
    g3: LineSegment StartX=-11.55 StartY=11.55 StartZ=0 EndX=11.55 EndY=11.55 EndZ=0
    g4: GeomPoint X=0 Y=0 Z=0
    g5: LineSegment StartX=12 StartY=-2 StartZ=0 EndX=12 EndY=2 EndZ=0
    g6: LineSegment StartX=12 StartY=2 StartZ=0 EndX=2 EndY=2 EndZ=0
    g7: LineSegment StartX=2 StartY=2 StartZ=0 EndX=2 EndY=12 EndZ=0
    g8: LineSegment StartX=2 StartY=12 StartZ=0 EndX=-2 EndY=12 EndZ=0
    g9: LineSegment StartX=-2 StartY=12 StartZ=0 EndX=-2 EndY=2 EndZ=0
    g10: LineSegment StartX=-2 StartY=2 StartZ=0 EndX=-12 EndY=2 EndZ=0
    g11: LineSegment StartX=-12 StartY=2 StartZ=0 EndX=-12 EndY=-2 EndZ=0
    g12: LineSegment StartX=-12 StartY=-2 StartZ=0 EndX=-2 EndY=-2 EndZ=0
    g13: LineSegment StartX=-2 StartY=-2 StartZ=0 EndX=-2 EndY=-12 EndZ=0
    g14: LineSegment StartX=-2 StartY=-12 StartZ=0 EndX=2 EndY=-12 EndZ=0
    g15: LineSegment StartX=2 StartY=-12 StartZ=0 EndX=2 EndY=-2 EndZ=0
    g16: LineSegment StartX=2 StartY=-2 StartZ=0 EndX=12 EndY=-2 EndZ=0
    g17: LineSegment StartX=-2 StartY=-2 StartZ=0 EndX=-2 EndY=2 EndZ=0
    g18: LineSegment StartX=-2 StartY=2 StartZ=0 EndX=2 EndY=2 EndZ=0
    g19: LineSegment StartX=2 StartY=2 StartZ=0 EndX=2 EndY=-2 EndZ=0
    g20: LineSegment StartX=2 StartY=-2 StartZ=0 EndX=-2 EndY=-2 EndZ=0
    g21: GeomPoint X=0 Y=0 Z=0
    g22: LineSegment StartX=-1.8 StartY=11.55 StartZ=0 EndX=-1.8 EndY=1.8 EndZ=0
    g23: LineSegment StartX=-1.8 StartY=1.8 StartZ=0 EndX=-11.55 EndY=1.8 EndZ=0
    g24: LineSegment StartX=-11.55 StartY=1.8 StartZ=0 EndX=-11.55 EndY=-1.8 EndZ=0
    g25: LineSegment StartX=-11.55 StartY=-1.8 StartZ=0 EndX=-1.8 EndY=-1.8 EndZ=0
    g26: LineSegment StartX=-1.8 StartY=-1.8 StartZ=0 EndX=-1.8 EndY=-11.55 EndZ=0
    g27: LineSegment StartX=-1.8 StartY=-11.55 StartZ=0 EndX=1.8 EndY=-11.55 EndZ=0
    g28: LineSegment StartX=1.8 StartY=-11.55 StartZ=0 EndX=1.8 EndY=-1.8 EndZ=0
    g29: LineSegment StartX=1.8 StartY=-1.8 StartZ=0 EndX=11.55 EndY=-1.8 EndZ=0
    g30: LineSegment StartX=11.55 StartY=-1.8 StartZ=0 EndX=11.55 EndY=1.8 EndZ=0
    g31: LineSegment StartX=11.55 StartY=1.8 StartZ=0 EndX=1.8 EndY=1.8 EndZ=0
    g32: LineSegment StartX=1.8 StartY=1.8 StartZ=0 EndX=1.8 EndY=11.55 EndZ=0
    g33: LineSegment StartX=1.8 StartY=11.55 StartZ=0 EndX=-1.8 EndY=11.55 EndZ=0
  constraints (94):
    c: Coincident(g0,g1)
    c: Coincident(g1,g2)
    c: Coincident(g2,g3)
    c: Coincident(g3,g0)
    c: Horizontal(g1)
    c: Horizontal(g3)
    c: Vertical(g0)
    c: Vertical(g2)
    c: Symmetric(g1,g0,g4)
    c: Coincident(g4,g-1)
    c: Vertical(g5)
    c: Coincident(g6,g5)
    c: Horizontal(g6)
    c: Coincident(g7,g6)
    c: Vertical(g7)
    c: Coincident(g8,g7)
    c: Horizontal(g8)
    c: Coincident(g9,g8)
    c: Vertical(g9)
    c: Coincident(g10,g9)
    c: Horizontal(g10)
    c: Coincident(g11,g10)
    c: Vertical(g11)
    c: Horizontal(g12)
    c: Coincident(g13,g12)
    c: Vertical(g13)
    c: Horizontal(g14)
    c: Coincident(g15,g14)
    c: Vertical(g15)
    c: Coincident(g16,g15)
    c: Coincident(g16,g5)
    c: Horizontal(g16)
    c: Equal(g5,g8)
    c: Equal(g8,g11)
    c: Equal(g11,g14)
    c: Coincident(g11,g12)
    c: Coincident(g14,g13)
    c: Equal(g16,g12)
    c: Equal(g16,g6)
    c: Equal(g7,g9)
    c: Equal(g10,g15)
    c: Coincident(g17,g18)
    c: Coincident(g18,g19)
    c: Coincident(g19,g20)
    c: Coincident(g20,g17)
    c: Horizontal(g18)
    c: Horizontal(g20)
    c: Vertical(g17)
    c: Vertical(g19)
    c: Symmetric(g18,g17,g21)
    c: Coincident(g21,g-1)
    c: Coincident(g18,g6)
    c: Coincident(g12,g17)
    c: DistanceX(g18,g18) = 4
    c: DistanceY(g7,g7) = 10
    c: Equal(g15,g7)
    c: Vertical(g22)
    c: Coincident(g23,g22)
    c: Horizontal(g23)
    c: Coincident(g24,g23)
    c: Vertical(g24)
    c: Coincident(g25,g24)
    c: Horizontal(g25)
    c: Coincident(g26,g25)
    c: Vertical(g26)
    c: Coincident(g27,g26)
    c: Horizontal(g27)
    c: Coincident(g28,g27)
    c: Vertical(g28)
    c: Coincident(g29,g28)
    c: Horizontal(g29)
    c: Coincident(g30,g29)
    c: Vertical(g30)
    c: Coincident(g31,g30)
    c: Horizontal(g31)
    c: Coincident(g32,g31)
    c: Vertical(g32)
    c: Coincident(g33,g32)
    c: Coincident(g33,g22)
    c: Horizontal(g33)
    c: Equal(g31,g23)
    c: Equal(g32,g22)
    c: Equal(g31,g29)
    c: Equal(g25,g29)
    c: Equal(g26,g28)
    c: Equal(g28,g32)
    c: Equal(g27,g30)
    c: DistanceX(g31,g6) = 0.2
    c: DistanceY(g31,g6) = 0.2
    c: DistanceY(g5,g29) = 0.2
    c: Equal(g28,g29)
    c: DistanceX(g21,g30) = 11.55
    c: PointOnObject(g22,g3)
    c: PointOnObject(g23,g2)
FEATURE [PartDesign::Pad] Pad012
  BaseFeature = -> Pad011
  Direction = (0,-1,2e-16)
  Length = 5
  Length2 = 10
  Placement = pos=(0,0,0) rot=(1,0,0;1.5708rad)
  Profile = -> Sketch021
  ReferenceAxis = -> Sketch021 [N_Axis]
  Reversed = true
  Type = 0
FEATURE [Sketcher::SketchObject] Sketch022
  ExternalGeometry = -> [Cone001]
  FullyConstrained = true
  MapMode = 5
  Placement = pos=(2.3e-15,10.5,-35) rot=(-1,0,0;1.5708rad)
  Support = -> [Cone001]
  expr: Constraints[11] = <<Properties>>.Handle_OD + 2
  sketch-geometry (5):
    g0: LineSegment StartX=-11.75 StartY=-46.75 StartZ=0 EndX=-11.75 EndY=-23.25 EndZ=0
    g1: LineSegment StartX=-11.75 StartY=-23.25 StartZ=0 EndX=11.75 EndY=-23.25 EndZ=0
    g2: LineSegment StartX=11.75 StartY=-23.25 StartZ=0 EndX=11.75 EndY=-46.75 EndZ=0
    g3: LineSegment StartX=11.75 StartY=-46.75 StartZ=0 EndX=-11.75 EndY=-46.75 EndZ=0
    g4: GeomPoint X=-2.3e-15 Y=-35 Z=0
  constraints (12):
    c: Coincident(g0,g1)
    c: Coincident(g1,g2)
    c: Coincident(g2,g3)
    c: Coincident(g3,g0)
    c: Horizontal(g1)
    c: Horizontal(g3)
    c: Vertical(g0)
    c: Vertical(g2)
    c: Symmetric(g1,g0,g4)
    c: Coincident(g4,g-3)
    c: Equal(g2,g1)
    c: DistanceX(g1,g1) = 23.5
FEATURE [PartDesign::Pocket] Pocket010
  BaseFeature = -> Cone001
  Direction = (-2e-16,-1,2e-16)
  Length = 8
  Length2 = 5
  Placement = pos=(0,0,-35) rot=(1,0,0;3.14159rad)
  Profile = -> Sketch022
  ReferenceAxis = -> Sketch022 [N_Axis]
  Type = 0
FEATURE [Sketcher::SketchObject] Sketch023
  FullyConstrained = true
  MapMode = 5
  Placement = pos=(0,5,-2.2e-15) rot=(-1,0,0;1.5708rad)
  Support = -> [Pad012]
  sketch-geometry (1):
    g0: Circle CenterX=0 CenterY=0 CenterZ=0 NormalX=0 NormalY=0 NormalZ=1 AngleXU=0 Radius=2.5
  constraints (2):
    c: Coincident(g0,g-1)
    c: Diameter(g0) = 5
FEATURE [PartDesign::Pad] Pad013
  BaseFeature = -> Pad012
  Direction = (0,1,-2e-16)
  Length = 3
  Length2 = 10
  Placement = pos=(0,0,0) rot=(1,0,0;1.5708rad)
  Profile = -> Sketch023
  ReferenceAxis = -> Sketch023 [N_Axis]
  Type = 0
FEATURE [PartDesign::Fillet] Fillet
  Base = -> Pad013 [Edge51]
  BaseFeature = -> Pad013
  Placement = pos=(0,0,0) rot=(1,0,0;1.5708rad)
  Radius = 2
  SupportTransform = false
  UseAllEdges = false
FEATURE [Sketcher::SketchObject] Sketch024
  ExternalGeometry = -> [Cone001]
  FullyConstrained = true
  MapMode = 5
  Placement = pos=(6e-16,2.5,-35) rot=(-1,0,0;1.5708rad)
  Support = -> [Pocket010]
  expr: Constraints[11] = Sketch022.Constraints[11]
  expr: Constraints[54] = Sketch019.Constraints[43]
  expr: Constraints[55] = Sketch019.Constraints[44]
  sketch-geometry (34):
    g0: LineSegment StartX=-11.75 StartY=-46.75 StartZ=0 EndX=-11.75 EndY=-23.25 EndZ=0
    g1: LineSegment StartX=-11.75 StartY=-23.25 StartZ=0 EndX=11.75 EndY=-23.25 EndZ=0
    g2: LineSegment StartX=11.75 StartY=-23.25 StartZ=0 EndX=11.75 EndY=-46.75 EndZ=0
    g3: LineSegment StartX=11.75 StartY=-46.75 StartZ=0 EndX=-11.75 EndY=-46.75 EndZ=0
    g4: GeomPoint X=-2.4e-15 Y=-35 Z=0
    g5: LineSegment StartX=12 StartY=-37 StartZ=0 EndX=12 EndY=-33 EndZ=0
    g6: LineSegment StartX=12 StartY=-33 StartZ=0 EndX=2 EndY=-33 EndZ=0
    g7: LineSegment StartX=2 StartY=-33 StartZ=0 EndX=2 EndY=-23 EndZ=0
    g8: LineSegment StartX=2 StartY=-23 StartZ=0 EndX=-2 EndY=-23 EndZ=0
    g9: LineSegment StartX=-2 StartY=-23 StartZ=0 EndX=-2 EndY=-33 EndZ=0
    g10: LineSegment StartX=-2 StartY=-33 StartZ=0 EndX=-12 EndY=-33 EndZ=0
    g11: LineSegment StartX=-12 StartY=-33 StartZ=0 EndX=-12 EndY=-37 EndZ=0
    g12: LineSegment StartX=-12 StartY=-37 StartZ=0 EndX=-2 EndY=-37 EndZ=0
    g13: LineSegment StartX=-2 StartY=-37 StartZ=0 EndX=-2 EndY=-47 EndZ=0
    g14: LineSegment StartX=-2 StartY=-47 StartZ=0 EndX=2 EndY=-47 EndZ=0
    g15: LineSegment StartX=2 StartY=-47 StartZ=0 EndX=2 EndY=-37 EndZ=0
    g16: LineSegment StartX=2 StartY=-37 StartZ=0 EndX=12 EndY=-37 EndZ=0
    g17: LineSegment StartX=-2 StartY=-37 StartZ=0 EndX=-2 EndY=-33 EndZ=0
    g18: LineSegment StartX=-2 StartY=-33 StartZ=0 EndX=2 EndY=-33 EndZ=0
    g19: LineSegment StartX=2 StartY=-33 StartZ=0 EndX=2 EndY=-37 EndZ=0
    g20: LineSegment StartX=2 StartY=-37 StartZ=0 EndX=-2 EndY=-37 EndZ=0
    g21: GeomPoint X=0 Y=0 Z=0
    g22: LineSegment StartX=-2 StartY=-23.25 StartZ=0 EndX=2 EndY=-23.25 EndZ=0
    g23: LineSegment StartX=2 StartY=-23.25 StartZ=0 EndX=2 EndY=-33 EndZ=0
    g24: LineSegment StartX=2 StartY=-33 StartZ=0 EndX=11.75 EndY=-33 EndZ=0
    g25: LineSegment StartX=11.75 StartY=-33 StartZ=0 EndX=11.75 EndY=-37 EndZ=0
    g26: LineSegment StartX=11.75 StartY=-37 StartZ=0 EndX=2 EndY=-37 EndZ=0
    g27: LineSegment StartX=2 StartY=-37 StartZ=0 EndX=2 EndY=-46.75 EndZ=0
    g28: LineSegment StartX=2 StartY=-46.75 StartZ=0 EndX=-2 EndY=-46.75 EndZ=0
    g29: LineSegment StartX=-2 StartY=-46.75 StartZ=0 EndX=-2 EndY=-37 EndZ=0
    g30: LineSegment StartX=-2 StartY=-37 StartZ=0 EndX=-11.75 EndY=-37 EndZ=0
    g31: LineSegment StartX=-11.75 StartY=-37 StartZ=0 EndX=-11.75 EndY=-33 EndZ=0
    g32: LineSegment StartX=-11.75 StartY=-33 StartZ=0 EndX=-2 EndY=-33 EndZ=0
    g33: LineSegment StartX=-2 StartY=-33 StartZ=0 EndX=-2 EndY=-23.25 EndZ=0
  constraints (90):
    c: Coincident(g0,g1)
    c: Coincident(g1,g2)
    c: Coincident(g2,g3)
    c: Coincident(g3,g0)
    c: Horizontal(g1)
    c: Horizontal(g3)
    c: Vertical(g0)
    c: Vertical(g2)
    c: Symmetric(g1,g0,g4)
    c: Coincident(g4,g-3)
    c: Equal(g2,g1)
    c: DistanceX(g1,g1) = 23.5
    c: Vertical(g5)
    c: Coincident(g6,g5)
    c: Horizontal(g6)
    c: Coincident(g7,g6)
    c: Vertical(g7)
    c: Coincident(g8,g7)
    c: Horizontal(g8)
    c: Coincident(g9,g8)
    c: Vertical(g9)
    c: Coincident(g10,g9)
    c: Horizontal(g10)
    c: Coincident(g11,g10)
    c: Vertical(g11)
    c: Horizontal(g12)
    c: Coincident(g13,g12)
    c: Vertical(g13)
    c: Horizontal(g14)
    c: Coincident(g15,g14)
    c: Vertical(g15)
    c: Coincident(g16,g15)
    c: Coincident(g16,g5)
    c: Horizontal(g16)
    c: Equal(g5,g8)
    c: Equal(g8,g11)
    c: Equal(g11,g14)
    c: Coincident(g11,g12)
    c: Coincident(g14,g13)
    c: Equal(g16,g12)
    c: Equal(g16,g6)
    c: Equal(g7,g9)
    c: Equal(g10,g15)
    c: Coincident(g17,g18)
    c: Coincident(g18,g19)
    c: Coincident(g19,g20)
    c: Coincident(g20,g17)
    c: Horizontal(g18)
    c: Horizontal(g20)
    c: Vertical(g17)
    c: Vertical(g19)
    c: Coincident(g21,g-1)
    c: Coincident(g18,g6)
    c: Coincident(g12,g17)
    c: DistanceX(g18,g18) = 4
    c: DistanceY(g7,g7) = 10
    c: Equal(g15,g7)
    c: Symmetric(g6,g12,g4)
    c: PointOnObject(g22,g9)
    c: PointOnObject(g22,g1)
    c: Horizontal(g22)
    c: PointOnObject(g22,g7)
    c: Coincident(g23,g22)
    c: Coincident(g23,g6)
    c: Coincident(g24,g23)
    c: PointOnObject(g24,g2)
    c: Horizontal(g24)
    c: Coincident(g25,g24)
    c: PointOnObject(g25,g16)
    c: Vertical(g25)
    c: Coincident(g26,g25)
    c: Coincident(g26,g15)
    c: Coincident(g27,g26)
    c: PointOnObject(g27,g3)
    c: Vertical(g27)
    c: Coincident(g28,g27)
    c: PointOnObject(g28,g13)
    c: Horizontal(g28)
    c: Coincident(g29,g28)
    c: Coincident(g29,g12)
    c: Coincident(g30,g29)
    c: PointOnObject(g30,g0)
    c: Horizontal(g30)
    c: Coincident(g31,g30)
    c: PointOnObject(g31,g10)
    c: Vertical(g31)
    c: Coincident(g32,g31)
    c: Coincident(g32,g9)
    c: Coincident(g33,g32)
    c: Coincident(g33,g22)
FEATURE [PartDesign::Pocket] Pocket011
  BaseFeature = -> Pocket010
  Direction = (-2e-16,-1,2e-16)
  Length = 3
  Length2 = 5
  Placement = pos=(0,0,-35) rot=(1,0,0;3.14159rad)
  Profile = -> Sketch024
  ReferenceAxis = -> Sketch024 [N_Axis]
  Type = 0
FEATURE [PartDesign::Body] Body  label="HeadInstert"
  Group = -> [Sketch,Pad,Sketch001,Pocket,Sketch002,Pocket001,Sketch004,Pocket002,Chamfer,Sketch003,Pocket003,Chamfer001,Sketch008,Pocket006,Chamfer003,Chamfer004,Chamfer005,Cone,Cone001,Sketch022,Pocket010,Sketch024,Pocket011]
  Origin = -> Origin001
  Tip = -> Pocket011
FEATURE [PartDesign::Fillet] Fillet001
  Base = -> Fillet [Edge3]
  BaseFeature = -> Fillet
  Placement = pos=(0,0,0) rot=(1,0,0;1.5708rad)
  Radius = 7
  SupportTransform = false
  UseAllEdges = false
FEATURE [Sketcher::SketchObject] Sketch025
  FullyConstrained = true
  MapMode = 5
  Placement = pos=(0,0,0) rot=(1,0,0;1.5708rad)
  Support = -> [XZ_Plane012]
  expr: Constraints[1] = <<Properties>>.Handle_OD - <<Properties>>.Clearance * 2
  sketch-geometry (1):
    g0: Circle CenterX=0 CenterY=0 CenterZ=0 NormalX=0 NormalY=0 NormalZ=1 AngleXU=0 Radius=10.55
  constraints (2):
    c: Coincident(g0,g-1)
    c: Diameter(g0) = 21.1
FEATURE [PartDesign::Pad] Pad014
  BaseFeature = -> Fillet001
  Direction = (0,-1,2e-16)
  Length = 9
  Length2 = 10
  Placement = pos=(0,0,0) rot=(1,0,0;1.5708rad)
  Profile = -> Sketch025
  ReferenceAxis = -> Sketch025 [N_Axis]
  TaperAngle = -2
  Type = 0
FEATURE [PartDesign::Chamfer] Chamfer006
  Angle = 45
  Base = -> Pad014 [Edge15,Edge19,Edge10,Edge11]
  BaseFeature = -> Pad014
  ChamferType = 0
  FlipDirection = false
  Placement = pos=(0,0,0) rot=(1,0,0;1.5708rad)
  Size = 1
  Size2 = 1
  SupportTransform = false
  UseAllEdges = false
FEATURE [PartDesign::Body] Body012  label="Pusher"
  Group = -> [Sketch020,Pad011,Sketch021,Pad012,Sketch023,Pad013,Fillet,Fillet001,Sketch025,Pad014,Chamfer006]
  Origin = -> Origin012
  Placement = pos=(0,2.5,0) rot=(0,0,1;0rad)
  Tip = -> Chamfer006
FEATURE [Sketcher::SketchObject] Sketch026
  FullyConstrained = true
  MapMode = 5
  Placement = pos=(0,0,0) rot=(1,0,0;1.5708rad)
  Support = -> [XZ_Plane013]
  expr: Constraints[1] = <<Properties>>.Handle_OD - 1
  sketch-geometry (2):
    g0: Circle CenterX=0 CenterY=0 CenterZ=0 NormalX=0 NormalY=0 NormalZ=1 AngleXU=0 Radius=10.25
    g1: Circle CenterX=0 CenterY=0 CenterZ=0 NormalX=0 NormalY=0 NormalZ=1 AngleXU=0 Radius=4
  constraints (4):
    c: Coincident(g0,g-1)
    c: Diameter(g0) = 20.5
    c: Coincident(g1,g0)
    c: Diameter(g1) = 8
FEATURE [PartDesign::Pad] Pad015
  Direction = (0,-1,-2e-16)
  Length = 10
  Length2 = 10
  Placement = pos=(0,0,0) rot=(1,0,0;1.5708rad)
  Profile = -> Sketch026
  ReferenceAxis = -> Sketch026 [N_Axis]
  Type = 0
FEATURE [PartDesign::Draft] Draft
  Angle = 2
  Base = -> Pad015 [Face1]
  BaseFeature = -> Pad015
  NeutralPlane = -> Pad015 [Face3]
  Placement = pos=(0,0,0) rot=(1,0,0;1.5708rad)
  SupportTransform = false
FEATURE [PartDesign::Body] Body013  label="WirePlug"
  Group = -> [Sketch026,Pad015,Draft]
  Origin = -> Origin013
  Placement = pos=(0,-190,0) rot=(0,0,1;0rad)
  Tip = -> Draft
FEATURE [App::Link] Body_CutLink
  LinkTransform = true
  LinkedObject = -> Body
FEATURE [App::Link] Body001_CutLink
  LinkTransform = true
  LinkedObject = -> Body001
FEATURE [App::Link] Body002_CutLink
  LinkTransform = true
  LinkedObject = -> Body002
FEATURE [App::Link] Body003_CutLink
  LinkTransform = true
  LinkedObject = -> Body003
FEATURE [App::Link] Body005_CutLink
  LinkTransform = true
  LinkedObject = -> Body005
FEATURE [App::Link] Body006_CutLink
  LinkTransform = true
  LinkedObject = -> Body006
FEATURE [App::Link] Body007_CutLink
  LinkTransform = true
  LinkedObject = -> Body007
FEATURE [App::Link] Body008_CutLink
  LinkTransform = true
  LinkedObject = -> Body008
FEATURE [App::Link] Body009_CutLink
  LinkTransform = true
  LinkedObject = -> Body009
FEATURE [App::Link] Body010_CutLink
  LinkTransform = true
  LinkedObject = -> Body010
FEATURE [App::Link] Body011_CutLink
  LinkTransform = true
  LinkedObject = -> Body011
FEATURE [App::Link] Body012_CutLink
  LinkTransform = true
  LinkedObject = -> Body012
FEATURE [App::Link] Body013_CutLink
  LinkTransform = true
  LinkedObject = -> Body013
FEATURE [Part::FeaturePython] SectionCutCompound  # WARN: FeaturePython — macro-defined, semantics opaque (R4)
  Mode = 0
  Objects = -> [Body_CutLink,Body001_CutLink,Body002_CutLink,Body003_CutLink,Body005_CutLink,Body006_CutLink,Body007_CutLink,Body008_CutLink,Body009_CutLink,Body010_CutLink,Body011_CutLink,Body012_CutLink,Body013_CutLink]
  Tolerance = 0
FEATURE [Part::Box] SectionCutBoxX
  AttacherType = Attacher::AttachEngine3D
  Height = 117
  Length = 111
  Placement = pos=(0,-200.5,-58.5) rot=(0,0,1;0rad)
  Width = 256
FEATURE [Part::Cut] SectionCutX
  Base = -> SectionCutCompound
  Tool = -> SectionCutBoxX
FEATURE [Sketcher::SketchObject] Sketch027
  FullyConstrained = true
  MapMode = 5
  Placement = pos=(0,0,0) rot=(1,0,0;1.5708rad)
  Support = -> [XZ_Plane002]
  sketch-geometry (5):
    g0: LineSegment StartX=-2.5 StartY=-45 StartZ=0 EndX=-2.5 EndY=45 EndZ=0
    g1: LineSegment StartX=-2.5 StartY=45 StartZ=0 EndX=2.5 EndY=45 EndZ=0
    g2: LineSegment StartX=2.5 StartY=45 StartZ=0 EndX=2.5 EndY=-45 EndZ=0
    g3: LineSegment StartX=2.5 StartY=-45 StartZ=0 EndX=-2.5 EndY=-45 EndZ=0
    g4: GeomPoint X=0 Y=0 Z=0
  constraints (12):
    c: Coincident(g0,g1)
    c: Coincident(g1,g2)
    c: Coincident(g2,g3)
    c: Coincident(g3,g0)
    c: Horizontal(g1)
    c: Horizontal(g3)
    c: Vertical(g0)
    c: Vertical(g2)
    c: Symmetric(g1,g0,g4)
    c: Coincident(g4,g-1)
    c: DistanceX(g1,g1) = 5
    c: DistanceY(g2,g2) = 90
FEATURE [PartDesign::Pocket] Pocket012
  BaseFeature = -> Pocket007
  Direction = (0,1,2e-16)
  Length = 5
  Length2 = 5
  Profile = -> Sketch027
  ReferenceAxis = -> Sketch027 [N_Axis]
  Reversed = true
  Type = 1
FEATURE [PartDesign::Body] Body002  label="PVCHammerHeadShell"
  Group = -> [Sketch009,Pad002,Sketch010,Pocket007,Sketch027,Pocket012]
  Origin = -> Origin002
  Tip = -> Pocket012
FEATURE [App::DocumentObjectGroup] Group  label="Non3DPrints"
  Group = -> [Body007,Body006,Body005,Body003,Body002,Body008,Body009,Body010,Body011]
FEATURE [TechDraw::DrawSVGTemplate] Template004
  EditableTexts = AuthorName=Alex Anastasakis; CheckDate=2024/11/11; CreationDate=2024/11/10; FC-Scale=1:2; FC-Title=Hammer; SheetNumber=1 of 2; Subtitle=Course: Industrial Design for Game Hardware; SupervisorName=Alvaro Uribe Quevedo
  Height = 297
  Orientation = 1
  Template = C:/Program Files/FreeCAD 0.21/data/Mod/TechDraw/Templates/A3_LandscapeTD.svg
  Width = 420
FEATURE [Part::Feature] trajectory_line011
  Placement = pos=(0,-250,0) rot=(0,0,1;0rad)
  shape: bbox 2e-07 x 20 x 2e-07 mm, 0 faces, 0 solids (baked)
FEATURE [App::DocumentObjectGroupPython] SimpleGroup011  label="Plug"  # scripted group (container) (typed FeaturePython)
  AnimationStepTime = 0
  AnimationSteps = 60
  Distance = 30
  Group = -> [trajectory_line011]
  Revolutions = 0
  dir_vectors = (1) [(0,-1,2.0446e-18)]
  rot_centers = (1) [(4.44089e-15,-10,1.14086e-15)]
  rot_vectors = (1) [(0,-1,2.0446e-18)]
FEATURE [Part::Feature] trajectory_line
  shape: bbox 2e-07 x 2e-07 x 160 mm, 0 faces, 0 solids (baked)
FEATURE [App::DocumentObjectGroupPython] SimpleGroup  label="PVC"  # scripted group (container) (typed FeaturePython)
  AnimationStepTime = 0
  AnimationSteps = 80
  Distance = 210
  Group = -> [trajectory_line]
  Revolutions = 0
  dir_vectors = (1) [(0,0,1)]
  rot_centers = (1) [(-8.88178e-15,0.160065,45)]
  rot_vectors = (1) [(0,0,1)]
FEATURE [Part::Feature] trajectory_line001
  shape: bbox 2e-07 x 2e-07 x 40 mm, 0 faces, 0 solids (baked)
FEATURE [App::DocumentObjectGroupPython] SimpleGroup001  label="FoamL"  # scripted group (container) (typed FeaturePython)
  AnimationStepTime = 0
  AnimationSteps = 80
  Distance = 65
  Group = -> [trajectory_line001]
  Revolutions = 0
  dir_vectors = (1) [(0,0,1)]
  rot_centers = (1) [(-3.55271e-15,2.04964e-16,20)]
  rot_vectors = (1) [(0,0,1)]
FEATURE [Part::Feature] trajectory_line002
  Placement = pos=(0,0,-150) rot=(0,0,1;0rad)
  shape: bbox 2e-07 x 2e-07 x 40 mm, 0 faces, 0 solids (baked)
FEATURE [App::DocumentObjectGroupPython] SimpleGroup002  label="FoamR"  # scripted group (container) (typed FeaturePython)
  AnimationStepTime = 0
  AnimationSteps = 80
  Distance = 65
  Group = -> [trajectory_line002]
  Revolutions = 0
  dir_vectors = (1) [(0,0,1)]
  rot_centers = (1) [(-3.55271e-15,2.04964e-16,58)]
  rot_vectors = (1) [(0,0,1)]
FEATURE [Part::Feature] trajectory_line003
  shape: bbox 2e-07 x 2e-07 x 20 mm, 0 faces, 0 solids (baked)
FEATURE [App::DocumentObjectGroupPython] SimpleGroup003  label="SensL"  # scripted group (container) (typed FeaturePython)
  AnimationStepTime = 0
  AnimationSteps = 60
  Distance = 30
  Group = -> [trajectory_line003]
  Revolutions = 0
  dir_vectors = (1) [(0,0,1)]
  rot_centers = (1) [(-1.04153e-16,-0.81059,1)]
  rot_vectors = (1) [(0,0,1)]
FEATURE [Part::Feature] trajectory_line004
  Placement = pos=(0,0,-65) rot=(0,0,1;0rad)
  shape: bbox 2e-07 x 2e-07 x 20 mm, 0 faces, 0 solids (baked)
FEATURE [App::DocumentObjectGroupPython] SimpleGroup004  label="SensR"  # scripted group (container) (typed FeaturePython)
  AnimationStepTime = 0
  AnimationSteps = 60
  Distance = 30
  Group = -> [trajectory_line004]
  Revolutions = 0
  dir_vectors = (1) [(0,0,1)]
  rot_centers = (1) [(-1.04153e-16,-0.81059,1)]
  rot_vectors = (1) [(0,0,1)]
FEATURE [Part::Feature] trajectory_line005
  Placement = pos=(0,11,0) rot=(0,0,1;0rad)
  shape: bbox 80 x 2e-07 x 2e-07 mm, 0 faces, 0 solids (baked)
FEATURE [App::DocumentObjectGroupPython] SimpleGroup005  label="Plate"  # scripted group (container) (typed FeaturePython)
  AnimationStepTime = 0
  AnimationSteps = 80
  Distance = 90
  Group = -> [trajectory_line005]
  Revolutions = 0
  dir_vectors = (1) [(1,0,0)]
  rot_centers = (1) [(22.5,6.50521e-19,0)]
  rot_vectors = (1) [(1,0,0)]
FEATURE [Part::Feature] trajectory_line006
  Placement = pos=(-80,0,0) rot=(0,0,1;0rad)
  shape: bbox 2e-07 x 50 x 2e-07 mm, 0 faces, 0 solids (baked)
FEATURE [App::DocumentObjectGroupPython] SimpleGroup006  label="HandleAssembly"  # scripted group (container) (typed FeaturePython)
  AnimationStepTime = 0
  AnimationSteps = 40
  Distance = 60
  Group = -> [trajectory_line006]
  Revolutions = 0
  dir_vectors = (6) [(0,1,0),(0,1,0),(0,1,0),(0,1,0),(0,1,0),(0,1,0)]
  rot_centers = (6) [(80,0.4,-2.36848e-16),(80,0.4,-2.36848e-16),(80,0.4,-2.36848e-16),(80,0.4,-2.36848e-16),(80,0.4,-2.36848e-16),(80,0.4,-2.36848e-16)]
  rot_vectors = (6) [(0,1,0),(0,1,0),(0,1,0),(0,1,0),(0,1,0),(0,1,0)]
FEATURE [Part::Feature] trajectory_line007
  Placement = pos=(-80,0,0) rot=(0,0,1;0rad)
  shape: bbox 2e-07 x 30 x 2e-07 mm, 0 faces, 0 solids (baked)
FEATURE [App::DocumentObjectGroupPython] SimpleGroup007  label="Top003"  # scripted group (container) (typed FeaturePython)
  AnimationStepTime = 0
  AnimationSteps = 40
  Distance = 70
  Group = -> [trajectory_line007]
  Revolutions = 0
  dir_vectors = (3) [(0,1,0),(0,1,0),(0,1,0)]
  rot_centers = (3) [(80,0.4,-2.36848e-16),(80,0.4,-2.36848e-16),(80,0.4,-2.36848e-16)]
  rot_vectors = (3) [(0,1,0),(0,1,0),(0,1,0)]
FEATURE [Part::Feature] trajectory_line008
  Placement = pos=(0,118,0) rot=(0,0,1;0rad)
  shape: bbox 2e-07 x 25 x 2e-07 mm, 0 faces, 0 solids (baked)
FEATURE [App::DocumentObjectGroupPython] SimpleGroup008  label="Foam"  # scripted group (container) (typed FeaturePython)
  AnimationStepTime = 0
  AnimationSteps = 80
  Distance = 55
  Group = -> [trajectory_line008]
  Revolutions = 0
  dir_vectors = (1) [(-2.46519e-32,-1,-2.22045e-16)]
  rot_centers = (1) [(0,-3,-5.24025e-16)]
  rot_vectors = (1) [(-2.46519e-32,-1,-2.22045e-16)]
FEATURE [Part::Feature] trajectory_line009
  Placement = pos=(0,111,0) rot=(0,0,1;0rad)
  shape: bbox 2e-07 x 2e-07 x 15 mm, 0 faces, 0 solids (baked)
FEATURE [App::DocumentObjectGroupPython] SimpleGroup009  label="Sens"  # scripted group (container) (typed FeaturePython)
  AnimationStepTime = 0
  AnimationSteps = 80
  Distance = 35
  Group = -> [trajectory_line009]
  Revolutions = 0
  dir_vectors = (1) [(0,0,1)]
  rot_centers = (1) [(-1.04153e-16,-0.81059,1)]
  rot_vectors = (1) [(0,0,1)]
FEATURE [Part::Feature] trajectory_line010
  shape: bbox 2e-07 x 90 x 2e-07 mm, 0 faces, 0 solids (baked)
FEATURE [App::DocumentObjectGroupPython] SimpleGroup010  label="Handle"  # scripted group (container) (typed FeaturePython)
  AnimationStepTime = 0
  AnimationSteps = 40
  Distance = 120
  Group = -> [trajectory_line010]
  Revolutions = 0
  dir_vectors = (2) [(0,-1,2.0446e-18),(0,-1,2.0446e-18)]
  rot_centers = (2) [(4.44089e-15,-10,1.14086e-15),(4.44089e-15,-10,1.14086e-15)]
  rot_vectors = (2) [(0,-1,2.0446e-18),(0,-1,2.0446e-18)]
FEATURE [App::DocumentObjectGroupPython] ExplodedAssembly  # scripted group (container) (typed FeaturePython)
  AnimationStep = 0
  CurrentTrajectory = 0
  Group = -> [SimpleGroup,SimpleGroup001,SimpleGroup002,SimpleGroup003,SimpleGroup004,SimpleGroup005,SimpleGroup006,SimpleGroup007,SimpleGroup008,SimpleGroup009,SimpleGroup010,SimpleGroup011]
  InAnimation = false
  RemoveAllTrajectories = false
  ResetAnimation = false
FEATURE [Spreadsheet::Sheet] Spreadsheet001  label="#BOM#"
  cells = A1='PARTS LIST; A2='ITEM NO.; B2='QTY; C2='NAME; D2='PART DESCRIPTION; E2='MATERIAL; F2='COST; A3=1; B3=1; C3='Shell; D3='Hammer head reinforcement; E3='PVC; F3='$19.49 (tube of PVC); A4=2; B4=2; C4='Foam Disc; D4='Large foam disc; E4='Polyethylene Foam; F4='$26.99 (pack of foam); A5=3; B5=1; C5='Head Top Cover; D5='Cover for top sensor; E5='PLA; F5='$22.99 (1kg of filament); A6=4; B6=3; C6='Sensor; D6='Force sensor; E6='Plastic/Metal; F6='$14.19ea; A7=5; B7=1; C7='Foam Disc; D7='Small foam disc; E7='Foam; F7='Shares cost of item NO. 2; A8=6; B8=1; C8='Pusher; D8='Top sensor pusher; E8='PLA; F8='Shares cost of item NO. 3; A9=7; B9=1; C9='Head Inner; D9='Container and support of all components; E9='PLA; F9='Shares cost of item NO. 3; A10=8; B10=1; C10='Handle; E10='Metal; F10='$19.99 (broom stick with desired handle); A11=9; B11=1; C11='Plug; D11='Makes a smaller hole for cable management; E11='PLA; F11='Shares cost of item NO. 3; A12=10; B12=1; C12='Spring Plate; D12='Resets the pusher; E12='Steel; F12='$40.06 (pack of shim stock)
FEATURE [TechDraw::DrawViewSpreadsheet] Sheet
  CellEnd = F12
  CellStart = A1
  Font = osifont
  LineWidth = 0.5
  LockPosition = false
  Rotation = 0
  ScaleType = 2
  Source = -> Spreadsheet001
  Symbol = <blob: 14343 chars omitted>
  TextSize = 12
  X = 306.458
  Y = 238.752
FEATURE [TechDraw::DrawViewBalloon] Balloon001
  BubbleShape = 0
  EndType = 0
  EndTypeScale = 1
  KinkLength = 5
  LockPosition = false
  OriginX = -28.3847
  OriginY = 126.188
  Rotation = 0
  Scale = 0.5
  ScaleType = 0
  ShapeScale = 1
  Text = 2
  TextWrapLen = -1
  X = -73.8491
  Y = 217.191
FEATURE [TechDraw::DrawViewBalloon] Balloon003
  BubbleShape = 0
  EndType = 0
  EndTypeScale = 1
  KinkLength = 5
  LockPosition = false
  OriginX = 64.6649
  OriginY = 141.874
  Rotation = 0
  Scale = 0.5
  ScaleType = 0
  ShapeScale = 1
  Text = 4
  TextWrapLen = -1
  X = 174.864
  Y = 182.273
FEATURE [App::Part] Part
  Group = -> [Body,Body001,Body002,Body003,Body005,Body006,Body007,Body008,Body009,Body010,Body011,Group,Body012,Body013]
  Origin = -> Origin014
FEATURE [Sketcher::SketchObject] Sketch028  label="base001"
  FullyConstrained = true
  MapMode = 5
  Support = -> [XY_Plane016]
  expr: Constraints[1] = <<Properties001>>.Head_ID
  sketch-geometry (1):
    g0: Circle CenterX=0 CenterY=0 CenterZ=0 NormalX=0 NormalY=0 NormalZ=1 AngleXU=0 Radius=25.7
  constraints (2):
    c: Coincident(g0,g-1)
    c: Diameter(g0) = 51.4
FEATURE [PartDesign::Pad] Pad016  label="Base001"
  Direction = (0,0,1)
  Length = 35
  Length2 = 35
  Profile = -> Sketch028
  ReferenceAxis = -> Sketch028 [N_Axis]
  Type = 4
  expr: Length = <<Properties001>>.Insert_Len / 2
  expr: Length2 = <<Properties001>>.Insert_Len / 2
FEATURE [Sketcher::SketchObject] Sketch029  label="sensor_wire_slot001"
  FullyConstrained = true
  MapMode = 5
  Support = -> [XY_Plane016]
  expr: Constraints[11] = <<Properties001>>.Sensor_Wire_Track_Width
  expr: Constraints[1] = Sketch028.Constraints[1]
  sketch-geometry (7):
    g0: Circle CenterX=0 CenterY=0 CenterZ=0 NormalX=0 NormalY=0 NormalZ=1 AngleXU=0 Radius=25.7
    g1: LineSegment StartX=-4 StartY=-25.3868 StartZ=0 EndX=-4 EndY=-14.4568 EndZ=0
    g2: LineSegment StartX=-4 StartY=-14.4568 StartZ=0 EndX=4 EndY=-14.4568 EndZ=0
    g3: LineSegment StartX=4 StartY=-14.4568 StartZ=0 EndX=4 EndY=-25.3868 EndZ=0
    g4: ArcOfCircle CenterX=0 CenterY=0 CenterZ=0 NormalX=0 NormalY=0 NormalZ=1 AngleXU=0 Radius=25.7 StartAngle=4.55611 EndAngle=4.86867
    g5: GeomPoint X=0 Y=-14.4568 Z=0
    g6: Circle CenterX=0 CenterY=0 CenterZ=0 NormalX=0 NormalY=0 NormalZ=1 AngleXU=0 Radius=15
  constraints (17):
    c: Coincident(g0,g-1)
    c: Diameter(g0) = 51.4
    c: Vertical(g1)
    c: Coincident(g2,g1)
    c: Horizontal(g2)
    c: Coincident(g3,g2)
    c: Vertical(g3)
    c: Coincident(g4,g0)
    c: Coincident(g4,g1)
    c: Coincident(g4,g3)
    c: PointOnObject(g3,g0)
    c: DistanceX(g2,g2) = 8
    c: Symmetric(g2,g2,g5)
    c: PointOnObject(g5,g-2)
    c: Coincident(g6,g4)
    c: Diameter(g6) = 30
    c: PointOnObject(g2,g6)
FEATURE [PartDesign::Pocket] Pocket013  label="Sensor_Wire_Slot001"
  BaseFeature = -> Pad016
  Direction = (0,0,-1)
  Length = 35
  Length2 = 35
  Profile = -> Sketch029
  ReferenceAxis = -> Sketch029 [N_Axis]
  Type = 4
  expr: Length = <<Properties001>>.Insert_Len / 2
  expr: Length2 = <<Properties001>>.Insert_Len / 2
FEATURE [Sketcher::SketchObject] Sketch030  label="handle_hole001"
  FullyConstrained = true
  MapMode = 5
  Placement = pos=(0,0,0) rot=(1,0,0;1.5708rad)
  Support = -> [XZ_Plane016]
  expr: Constraints[1] = <<Properties001>>.Handle_OD + <<Properties001>>.Clearance * 2
  sketch-geometry (1):
    g0: Circle CenterX=0 CenterY=0 CenterZ=0 NormalX=0 NormalY=0 NormalZ=1 AngleXU=0 Radius=10.95
  constraints (2):
    c: Coincident(g0,g-1)
    c: Diameter(g0) = 21.9
FEATURE [PartDesign::Pocket] Pocket014  label="Handle_hole001"
  BaseFeature = -> Pocket013
  Direction = (0,1,2e-16)
  Length = 25.7
  Length2 = 25.7
  Profile = -> Sketch030
  ReferenceAxis = -> Sketch030 [N_Axis]
  Type = 4
  expr: Length = <<Properties001>>.Head_ID / 2
  expr: Length2 = <<Properties001>>.Head_ID / 2
FEATURE [Sketcher::SketchObject] Sketch031  label="spring_plate_slot001"
  FullyConstrained = true
  MapMode = 5
  Support = -> [XY_Plane016]
  expr: Constraints[1] = Sketch028.Constraints[1]
  expr: Constraints[3] = <<Properties001>>.Sensor_Diameter + <<Properties001>>.Clearance * 2
  expr: Constraints[7] = <<Properties001>>.Spring_Plate_Len
  sketch-geometry (15):
    g0: Circle CenterX=0 CenterY=0 CenterZ=0 NormalX=0 NormalY=0 NormalZ=1 AngleXU=0 Radius=25.7
    g1: LineSegment StartX=-15.2 StartY=15.4669 StartZ=0 EndX=15.2 EndY=15.4669 EndZ=0
    g2: GeomPoint X=0 Y=15.4669 Z=0
    g3: LineSegment StartX=-23 StartY=11.4669 StartZ=0 EndX=23 EndY=11.4669 EndZ=0
    g4: GeomPoint X=0 Y=11.4669 Z=0
    g5: LineSegment StartX=-15.2 StartY=15.4669 StartZ=0 EndX=-21 EndY=11.4669 EndZ=0
    g6: LineSegment StartX=15.2 StartY=15.4669 StartZ=0 EndX=21 EndY=11.4669 EndZ=0
    g7: LineSegment StartX=21 StartY=11.4669 StartZ=0 EndX=23 EndY=11.4669 EndZ=0
    g8: LineSegment StartX=-21 StartY=11.4669 StartZ=0 EndX=-23 EndY=11.4669 EndZ=0
    g9: ArcOfCircle CenterX=0 CenterY=0 CenterZ=0 NormalX=0 NormalY=0 NormalZ=1 AngleXU=0 Radius=25.7 StartAngle=2.6791 EndAngle=2.80587
    g10: ArcOfCircle CenterX=0 CenterY=0 CenterZ=0 NormalX=0 NormalY=0 NormalZ=1 AngleXU=0 Radius=25.7 StartAngle=0.335723 EndAngle=0.462496
    g11: LineSegment StartX=-11 StartY=10.5 StartZ=0 EndX=-24.2652 EndY=8.46691 EndZ=0
    g12: LineSegment StartX=11 StartY=10.5 StartZ=0 EndX=24.2652 EndY=8.46691 EndZ=0
    g13: LineSegment StartX=11 StartY=10.5 StartZ=0 EndX=-11 EndY=10.5 EndZ=0
    g14: GeomPoint X=0 Y=10.5 Z=0
  constraints (39):
    c: Coincident(g0,g-1)
    c: Diameter(g0) = 51.4
    c: Horizontal(g1)
    c: DistanceX(g1,g1) = 30.4
    c: Symmetric(g1,g1,g2)
    c: PointOnObject(g2,g-2)
    c: Horizontal(g3)
    c: DistanceX(g3,g3) = 46
    c: Symmetric(g3,g3,g4)
    c: PointOnObject(g4,g-2)
    c: Coincident(g5,g1)
    c: PointOnObject(g5,g3)
    c: Coincident(g6,g1)
    c: PointOnObject(g6,g3)
    c: Coincident(g7,g6)
    c: PointOnObject(g7,g0)
    c: Horizontal(g7)
    c: Coincident(g8,g5)
    c: PointOnObject(g8,g0)
    c: Horizontal(g8)
    c: Equal(g8,g7)
    c: PointOnObject(g3,g0)
    c: DistanceY(g6,g1) = 4
    c: DistanceX(g6,g7) = 2
    c: Coincident(g9,g0)
    c: Coincident(g9,g8)
    c: Coincident(g10,g9)
    c: Coincident(g10,g7)
    c: Coincident(g13,g12)
    c: Coincident(g13,g11)
    c: Horizontal(g13)
    c: Coincident(g10,g12)
    c: Coincident(g9,g11)
    c: DistanceX(g12,g6) = 10
    c: Equal(g12,g11)
    c: DistanceY(g10,g7) = 3
    c: Symmetric(g13,g13,g14)
    c: PointOnObject(g14,g-2)
    c: DistanceY(g9,g14) = 10.5
FEATURE [Sketcher::SketchObject] Sketch032  label="top_sensor_hole001"
  FullyConstrained = true
  MapMode = 5
  Placement = pos=(0,0,0) rot=(0.57735,0.57735,0.57735;2.0944rad)
  Support = -> [YZ_Plane016]
  expr: Constraints[20] = <<Properties001>>.Head_ID
  expr: Constraints[7] = <<Properties001>>.Sensor_Diameter + 4
  sketch-geometry (9):
    g0: LineSegment StartX=-25.7 StartY=-17 StartZ=0 EndX=-25.7 EndY=17 EndZ=0
    g1: LineSegment StartX=25.7 StartY=17 StartZ=0 EndX=25.7 EndY=-17 EndZ=0
    g2: LineSegment StartX=25.7 StartY=-17 StartZ=0 EndX=-25.7 EndY=-17 EndZ=0
    g3: GeomPoint X=0 Y=0 Z=0
    g4: LineSegment StartX=10.5 StartY=17 StartZ=0 EndX=25.7 EndY=17 EndZ=0
    g5: LineSegment StartX=25.7 StartY=17 StartZ=0 EndX=25.7 EndY=-17 EndZ=0
    g6: LineSegment StartX=25.7 StartY=-17 StartZ=0 EndX=10.5 EndY=-17 EndZ=0
    g7: LineSegment StartX=10.5 StartY=-17 StartZ=0 EndX=10.5 EndY=17 EndZ=0
    g8: LineSegment StartX=-25.7 StartY=17 StartZ=0 EndX=25.7 EndY=17 EndZ=0
  constraints (23):
    c: Coincident(g1,g2)
    c: Coincident(g2,g0)
    c: Horizontal(g2)
    c: Vertical(g0)
    c: Vertical(g1)
    c: Symmetric(g1,g0,g3)
    c: Coincident(g3,g-1)
    c: DistanceY(g1,g1) = 34
    c: Coincident(g4,g5)
    c: Coincident(g5,g6)
    c: Coincident(g6,g7)
    c: Horizontal(g4)
    c: Horizontal(g6)
    c: Vertical(g5)
    c: Vertical(g7)
    c: PointOnObject(g5,g2)
    c: Coincident(g7,g4)
    c: Coincident(g8,g0)
    c: Coincident(g8,g1)
    c: Horizontal(g8)
    c: DistanceX(g8,g8) = 51.4
    c: Coincident(g4,g1)
    c: DistanceX(g3,g4) = 10.5
FEATURE [PartDesign::Pocket] Pocket015  label="Top_Sensor_Hole001"
  BaseFeature = -> Pocket014
  Direction = (-1,2e-16,-3e-16)
  Length = 17
  Length2 = 17
  Profile = -> Sketch032
  ReferenceAxis = -> Sketch032 [N_Axis]
  Type = 4
  expr: Length = <<Properties001>>.Sensor_Diameter / 2 + 2
  expr: Length2 = <<Properties001>>.Sensor_Diameter / 2 + 2
FEATURE [PartDesign::Chamfer] Chamfer007
  Angle = 70
  Base = -> Pocket015 [Edge30,Edge32]
  BaseFeature = -> Pocket015
  ChamferType = 2
  FlipDirection = false
  Size = 8
  Size2 = 1
  SupportTransform = false
  UseAllEdges = false
FEATURE [PartDesign::Pocket] Pocket016  label="Spring_Plate_Slot001"
  BaseFeature = -> Chamfer007
  Direction = (0,0,-1)
  Length = 10
  Length2 = 10
  Profile = -> Sketch031
  ReferenceAxis = -> Sketch031 [N_Axis]
  Type = 4
FEATURE [PartDesign::Chamfer] Chamfer008
  Angle = 45
  Base = -> Pocket016 [Edge43,Edge46,Edge45,Edge47,Edge44,Edge42]
  BaseFeature = -> Pocket016
  ChamferType = 0
  FlipDirection = false
  Size = 0.5
  Size2 = 1
  SupportTransform = false
  UseAllEdges = false
FEATURE [Sketcher::SketchObject] Sketch033  label="top_sens_base001"
  FullyConstrained = true
  MapMode = 5
  Support = -> [XY_Plane015]
  expr: Constraints[18] = <<Properties001>>.Clearance
  expr: Constraints[1] = <<Properties001>>.Head_ID
  expr: Constraints[3] = 34 - <<Properties001>>.Clearance * 2
  expr: Constraints[6] = 10.5 + <<Properties001>>.Clearance
  sketch-geometry (8):
    g0: Circle CenterX=0 CenterY=0 CenterZ=0 NormalX=0 NormalY=0 NormalZ=1 AngleXU=0 Radius=25.7
    g1: LineSegment StartX=-16.8 StartY=10.7 StartZ=0 EndX=16.8 EndY=10.7 EndZ=0
    g2: GeomPoint X=0 Y=10.7 Z=0
    g3: LineSegment StartX=-16.8 StartY=10.7 StartZ=0 EndX=-16.8 EndY=19.1836 EndZ=0
    g4: LineSegment StartX=16.8 StartY=10.7 StartZ=0 EndX=16.8 EndY=19.1836 EndZ=0
    g5: GeomPoint X=0 Y=25.7 Z=0
    g6: ArcOfCircle CenterX=0 CenterY=0 CenterZ=0 NormalX=0 NormalY=0 NormalZ=1 AngleXU=0 Radius=25.5 StartAngle=0.851542 EndAngle=2.29005
    g7: GeomPoint X=0 Y=25.5 Z=0
  constraints (19):
    c: Coincident(g0,g-1)
    c: Diameter(g0) = 51.4
    c: Horizontal(g1)
    c: DistanceX(g1,g1) = 33.6
    c: Symmetric(g1,g1,g2)
    c: PointOnObject(g2,g-2)
    c: DistanceY(g0,g2) = 10.7
    c: Coincident(g3,g1)
    c: Vertical(g3)
    c: Vertical(g4)
    c: Coincident(g4,g1)
    c: PointOnObject(g5,g0)
    c: PointOnObject(g5,g-2)
    c: Coincident(g6,g0)
    c: Coincident(g6,g3)
    c: Coincident(g6,g4)
    c: PointOnObject(g7,g6)
    c: PointOnObject(g7,g-2)
    c: DistanceY(g7,g5) = 0.2
FEATURE [PartDesign::Pad] Pad017  label="Top_Base001"
  Direction = (0,0,1)
  Length = 16.8
  Length2 = 16.8
  Profile = -> Sketch033
  ReferenceAxis = -> Sketch033 [N_Axis]
  Type = 4
  expr: Length = <<Properties001>>.Sensor_Diameter / 2 + 2 - <<Properties001>>.Clearance
  expr: Length2 = <<Properties001>>.Sensor_Diameter / 2 + 2 - <<Properties001>>.Clearance
FEATURE [Sketcher::SketchObject] Sketch034
  FullyConstrained = true
  MapMode = 5
  Support = -> [XY_Plane015]
  expr: Constraints[1] = Sketch031.Constraints[1]
  expr: Constraints[22] = Sketch031.Constraints[22]
  expr: Constraints[23] = Sketch031.Constraints[23]
  expr: Constraints[33] = Sketch031.Constraints[33]
  expr: Constraints[35] = Sketch031.Constraints[35]
  expr: Constraints[38] = Sketch031.Constraints[38]
  expr: Constraints[3] = Sketch031.Constraints[3]
  expr: Constraints[7] = Sketch031.Constraints[7]
  sketch-geometry (15):
    g0: Circle CenterX=0 CenterY=0 CenterZ=0 NormalX=0 NormalY=0 NormalZ=1 AngleXU=0 Radius=25.7
    g1: LineSegment StartX=-15.2 StartY=15.4669 StartZ=0 EndX=15.2 EndY=15.4669 EndZ=0
    g2: GeomPoint X=0 Y=15.4669 Z=0
    g3: LineSegment StartX=-23 StartY=11.4669 StartZ=0 EndX=23 EndY=11.4669 EndZ=0
    g4: GeomPoint X=0 Y=11.4669 Z=0
    g5: LineSegment StartX=-15.2 StartY=15.4669 StartZ=0 EndX=-21 EndY=11.4669 EndZ=0
    g6: LineSegment StartX=15.2 StartY=15.4669 StartZ=0 EndX=21 EndY=11.4669 EndZ=0
    g7: LineSegment StartX=21 StartY=11.4669 StartZ=0 EndX=23 EndY=11.4669 EndZ=0
    g8: LineSegment StartX=-21 StartY=11.4669 StartZ=0 EndX=-23 EndY=11.4669 EndZ=0
    g9: ArcOfCircle CenterX=0 CenterY=0 CenterZ=0 NormalX=0 NormalY=0 NormalZ=1 AngleXU=0 Radius=25.7 StartAngle=2.6791 EndAngle=2.80587
    g10: ArcOfCircle CenterX=0 CenterY=0 CenterZ=0 NormalX=0 NormalY=0 NormalZ=1 AngleXU=0 Radius=25.7 StartAngle=0.335723 EndAngle=0.462496
    g11: LineSegment StartX=-11 StartY=10.5 StartZ=0 EndX=-24.2652 EndY=8.46691 EndZ=0
    g12: LineSegment StartX=11 StartY=10.5 StartZ=0 EndX=24.2652 EndY=8.46691 EndZ=0
    g13: LineSegment StartX=11 StartY=10.5 StartZ=0 EndX=-11 EndY=10.5 EndZ=0
    g14: GeomPoint X=0 Y=10.5 Z=0
  constraints (40):
    c: Coincident(g0,g-1)
    c: Diameter(g0) = 51.4
    c: Horizontal(g1)
    c: DistanceX(g1,g1) = 30.4
    c: Symmetric(g1,g1,g2)
    c: PointOnObject(g2,g-2)
    c: Horizontal(g3)
    c: DistanceX(g3,g3) = 46
    c: Symmetric(g3,g3,g4)
    c: PointOnObject(g4,g-2)
    c: Coincident(g5,g1)
    c: PointOnObject(g5,g3)
    c: Coincident(g6,g1)
    c: PointOnObject(g6,g3)
    c: Coincident(g7,g6)
    c: PointOnObject(g7,g0)
    c: Horizontal(g7)
    c: Coincident(g8,g5)
    c: PointOnObject(g8,g0)
    c: Horizontal(g8)
    c: Equal(g8,g7)
    c: PointOnObject(g3,g0)
    c: DistanceY(g6,g1) = 4
    c: DistanceX(g6,g7) = 2
    c: Coincident(g9,g0)
    c: Coincident(g9,g8)
    c: Coincident(g10,g9)
    c: Coincident(g10,g7)
    c: Coincident(g13,g12)
    c: Coincident(g13,g11)
    c: Horizontal(g13)
    c: Coincident(g10,g12)
    c: Coincident(g9,g11)
    c: DistanceX(g12,g6) = 10
    c: Equal(g12,g11)
    c: DistanceY(g10,g7) = 3
    c: Symmetric(g13,g13,g14)
    c: PointOnObject(g14,g-2)
    c: DistanceY(g9,g14) = 10.5
    c: DistanceY(g9,g2) = 15.4669
FEATURE [PartDesign::Pocket] Pocket017
  BaseFeature = -> Pad017
  Direction = (0,0,-1)
  Length = 9.5
  Length2 = 9.5
  Profile = -> Sketch034
  ReferenceAxis = -> Sketch034 [N_Axis]
  Type = 4
FEATURE [PartDesign::Chamfer] Chamfer009
  Angle = 45
  Base = -> Pocket017 [Edge22,Edge12]
  BaseFeature = -> Pocket017
  ChamferType = 0
  FlipDirection = false
  Size = 0.3
  Size2 = 1
  SupportTransform = false
  UseAllEdges = false
FEATURE [Sketcher::SketchObject] Sketch035
  FullyConstrained = true
  MapMode = 5
  Placement = pos=(0,0,0) rot=(1,0,0;1.5708rad)
  Support = -> [XZ_Plane015]
  expr: Constraints[11] = <<Properties001>>.Sensor_Wire_Track_Width
  expr: Constraints[1] = <<Properties001>>.Sensor_Diameter + 1
  expr: Constraints[27] = <<Properties001>>.Sensor_Wire_Track_Width
  sketch-geometry (11):
    g0: Circle CenterX=0 CenterY=0 CenterZ=0 NormalX=0 NormalY=0 NormalZ=1 AngleXU=0 Radius=15.5
    g1: LineSegment StartX=-4 StartY=14.975 StartZ=0 EndX=-4 EndY=27.305 EndZ=0
    g2: LineSegment StartX=-4 StartY=27.305 StartZ=0 EndX=4 EndY=27.305 EndZ=0
    g3: LineSegment StartX=4 StartY=27.305 StartZ=0 EndX=4 EndY=14.975 EndZ=0
    g4: GeomPoint X=0 Y=27.305 Z=0
    g5: LineSegment StartX=-4 StartY=-14.975 StartZ=0 EndX=-4 EndY=-27.305 EndZ=0
    g6: LineSegment StartX=-4 StartY=-27.305 StartZ=0 EndX=4 EndY=-27.305 EndZ=0
    g7: LineSegment StartX=4 StartY=-27.305 StartZ=0 EndX=4 EndY=-14.975 EndZ=0
    g8: GeomPoint X=0 Y=-27.305 Z=0
    g9: ArcOfCircle CenterX=0 CenterY=0 CenterZ=0 NormalX=0 NormalY=0 NormalZ=1 AngleXU=0 Radius=15.5 StartAngle=1.83181 EndAngle=4.45137
    g10: ArcOfCircle CenterX=0 CenterY=0 CenterZ=0 NormalX=0 NormalY=0 NormalZ=1 AngleXU=0 Radius=15.5 StartAngle=4.97341 EndAngle=7.59296
  constraints (28):
    c: Coincident(g0,g-1)
    c: Diameter(g0) = 31
    c: PointOnObject(g1,g0)
    c: Vertical(g1)
    c: Coincident(g2,g1)
    c: Horizontal(g2)
    c: Coincident(g3,g2)
    c: PointOnObject(g3,g0)
    c: Vertical(g3)
    c: Symmetric(g2,g2,g4)
    c: PointOnObject(g4,g-2)
    c: DistanceX(g2,g2) = 8
    c: DistanceY(g3,g3) = 12.33
    c: Vertical(g5)
    c: Coincident(g6,g5)
    c: Horizontal(g6)
    c: Coincident(g7,g6)
    c: Vertical(g7)
    c: Symmetric(g6,g6,g8)
    c: PointOnObject(g8,g-2)
    c: Equal(g7,g3)
    c: Coincident(g9,g0)
    c: Coincident(g9,g1)
    c: Coincident(g9,g5)
    c: Coincident(g10,g9)
    c: Coincident(g10,g3)
    c: Coincident(g10,g7)
    c: DistanceX(g6,g6) = 8
FEATURE [PartDesign::Pocket] Pocket018
  BaseFeature = -> Chamfer009
  Direction = (0,1,2e-16)
  Length = 0
  Length2 = 5
  Offset = 0.4
  Profile = -> Sketch035
  ReferenceAxis = -> Sketch035 [N_Axis]
  Type = 3
  UpToFace = -> Chamfer009 [Face11]
FEATURE [PartDesign::Body] Body015  label="TopSensor001"
  Group = -> [Sketch033,Pad017,Sketch034,Pocket017,Chamfer009,Sketch035,Pocket018]
  Origin = -> Origin015
  Placement = pos=(0,135,0) rot=(0,0,1;0rad)
  Tip = -> Pocket018
FEATURE [Sketcher::SketchObject] Sketch036
  FullyConstrained = true
  MapMode = 5
  Placement = pos=(0,0,0) rot=(0.57735,0.57735,0.57735;2.0944rad)
  Support = -> [YZ_Plane016]
  expr: Constraints[16] = <<Properties001>>.Sensor_Diameter + 2
  sketch-geometry (14):
    g0: LineSegment StartX=15.5 StartY=21 StartZ=0 EndX=15.5 EndY=-21 EndZ=0
    g1: LineSegment StartX=15.5 StartY=-21 StartZ=0 EndX=-19.02 EndY=-21 EndZ=0
    g2: LineSegment StartX=-19.02 StartY=-21 StartZ=0 EndX=-19.02 EndY=-16 EndZ=0
    g3: LineSegment StartX=-19.02 StartY=-16 StartZ=0 EndX=10.5 EndY=-16 EndZ=0
    g4: LineSegment StartX=10.5 StartY=-16 StartZ=0 EndX=10.5 EndY=16 EndZ=0
    g5: LineSegment StartX=10.5 StartY=16 StartZ=0 EndX=-19.02 EndY=16 EndZ=0
    g6: LineSegment StartX=-19.02 StartY=16 StartZ=0 EndX=-19.02 EndY=21 EndZ=0
    g7: LineSegment StartX=-19.02 StartY=21 StartZ=0 EndX=15.5 EndY=21 EndZ=0
    g8: GeomPoint X=10.5 Y=0 Z=0
    g9: GeomPoint X=15.5 Y=0 Z=0
    g10: GeomPoint X=15.5 Y=21 Z=0
    g11: GeomPoint X=15.5 Y=-21 Z=0
    g12: GeomPoint X=10.5 Y=16 Z=0
    g13: GeomPoint X=10.5 Y=-16 Z=0
  constraints (30):
    c: Vertical(g0)
    c: Horizontal(g1)
    c: Coincident(g2,g1)
    c: Vertical(g2)
    c: Coincident(g3,g2)
    c: Horizontal(g3)
    c: Vertical(g4)
    c: Horizontal(g5)
    c: Coincident(g6,g5)
    c: Vertical(g6)
    c: Coincident(g7,g6)
    c: Horizontal(g7)
    c: Symmetric(g10,g11,g9)
    c: Symmetric(g13,g12,g8)
    c: PointOnObject(g8,g-1)
    c: PointOnObject(g9,g-1)
    c: DistanceY(g13,g12) = 32
    c: DistanceY(g6,g6) = 5
    c: DistanceX(g8,g9) = 5
    c: DistanceX(g-1,g8) = 10.5
    c: DistanceX(g7,g10) = 34.52
    c: Coincident(g0,g10)
    c: Coincident(g7,g0)
    c: Coincident(g4,g12)
    c: Coincident(g5,g4)
    c: Coincident(g0,g11)
    c: Coincident(g4,g13)
    c: Coincident(g3,g4)
    c: Coincident(g1,g0)
    c: Equal(g3,g5)
FEATURE [PartDesign::Pocket] Pocket019
  BaseFeature = -> Chamfer008
  Direction = (-1,2e-16,-3e-16)
  Length = 4
  Length2 = 4
  Profile = -> Sketch036
  ReferenceAxis = -> Sketch036 [N_Axis]
  Type = 4
  expr: Length = <<Properties001>>.Sensor_Wire_Track_Width / 2
  expr: Length2 = <<Properties001>>.Sensor_Wire_Track_Width / 2
FEATURE [PartDesign::Chamfer] Chamfer010
  Angle = 65
  Base = -> Pocket019 [Edge148,Edge154]
  BaseFeature = -> Pocket019
  ChamferType = 2
  FlipDirection = false
  Size = 3
  Size2 = 1
  SupportTransform = false
  UseAllEdges = false
FEATURE [PartDesign::Chamfer] Chamfer011
  Angle = 45
  Base = -> Chamfer010 [Edge167,Edge85,Edge52,Edge56]
  BaseFeature = -> Chamfer010
  ChamferType = 0
  FlipDirection = false
  Size = 2
  Size2 = 1
  SupportTransform = false
  UseAllEdges = false
FEATURE [PartDesign::Chamfer] Chamfer012
  Angle = 45
  Base = -> Chamfer011 [Edge169,Edge38]
  BaseFeature = -> Chamfer011
  ChamferType = 1
  FlipDirection = false
  Size = 4
  Size2 = 3.999
  SupportTransform = false
  UseAllEdges = false
FEATURE [PartDesign::AdditiveCone] Cone002
  Angle = 360
  AttacherType = Attacher::AttachEngine3D
  BaseFeature = -> Chamfer012
  Height = 1.5
  MapMode = 5
  Placement = pos=(0,0,35) rot=(0,0,1;0rad)
  Radius1 = 12
  Radius2 = 6
  Support = -> [Chamfer012]
FEATURE [PartDesign::AdditiveCone] Cone003
  Angle = 360
  AttacherType = Attacher::AttachEngine3D
  BaseFeature = -> Cone002
  Height = 1.5
  MapMode = 5
  Placement = pos=(0,0,-35) rot=(1,0,0;3.14159rad)
  Radius1 = 12
  Radius2 = 6
  Support = -> [Cone002]
FEATURE [Sketcher::SketchObject] Sketch037
  FullyConstrained = true
  MapMode = 5
  Support = -> [XY_Plane017]
  sketch-geometry (2):
    g0: Circle CenterX=0 CenterY=0 CenterZ=0 NormalX=0 NormalY=0 NormalZ=1 AngleXU=0 Radius=26
    g1: Circle CenterX=0 CenterY=0 CenterZ=0 NormalX=0 NormalY=0 NormalZ=1 AngleXU=0 Radius=30
  constraints (4):
    c: Coincident(g0,g-1)
    c: Coincident(g1,g0)
    c: Diameter(g0) = 52
    c: Diameter(g1) = 60
FEATURE [PartDesign::Pad] Pad018
  Direction = (0,0,1)
  Length = 45
  Length2 = 45
  Profile = -> Sketch037
  ReferenceAxis = -> Sketch037 [N_Axis]
  Type = 4
FEATURE [Sketcher::SketchObject] Sketch038
  FullyConstrained = true
  MapMode = 5
  Placement = pos=(0,0,0) rot=(1,0,0;1.5708rad)
  Support = -> [XZ_Plane017]
  expr: Constraints[1] = <<Properties001>>.Handle_OD
  sketch-geometry (1):
    g0: Circle CenterX=0 CenterY=0 CenterZ=0 NormalX=0 NormalY=0 NormalZ=1 AngleXU=0 Radius=10.75
  constraints (2):
    c: Coincident(g0,g-1)
    c: Diameter(g0) = 21.5
FEATURE [PartDesign::Pocket] Pocket020
  BaseFeature = -> Pad018
  Direction = (0,1,2e-16)
  Length = 5
  Length2 = 5
  Profile = -> Sketch038
  ReferenceAxis = -> Sketch038 [N_Axis]
  Reversed = true
  Type = 1
FEATURE [Sketcher::SketchObject] Sketch039
  FullyConstrained = true
  MapMode = 5
  Placement = pos=(0,0,0) rot=(1,0,0;1.5708rad)
  Support = -> [XZ_Plane018]
  expr: Constraints[3] = <<Properties001>>.Handle_ID
  sketch-geometry (2):
    g0: Circle CenterX=0 CenterY=0 CenterZ=0 NormalX=0 NormalY=0 NormalZ=1 AngleXU=0 Radius=10.625
    g1: Circle CenterX=0 CenterY=0 CenterZ=0 NormalX=0 NormalY=0 NormalZ=1 AngleXU=0 Radius=10.25
  constraints (4):
    c: Coincident(g0,g-1)
    c: Diameter(g0) = 21.25
    c: Coincident(g1,g0)
    c: Diameter(g1) = 20.5
FEATURE [PartDesign::Pad] Pad019
  Direction = (0,-1,-2e-16)
  Length = 200
  Length2 = 10
  Placement = pos=(0,0,0) rot=(1,0,0;1.5708rad)
  Profile = -> Sketch039
  ReferenceAxis = -> Sketch039 [N_Axis]
  Type = 0
FEATURE [Sketcher::SketchObject] Sketch040
  FullyConstrained = true
  MapMode = 5
  Support = -> [XY_Plane019]
  sketch-geometry (5):
    g0: ArcOfCircle CenterX=0 CenterY=0 CenterZ=0 NormalX=0 NormalY=0 NormalZ=1 AngleXU=0 Radius=15 StartAngle=4.90695 EndAngle=10.801
    g1: LineSegment StartX=2.9 StartY=-14.717 StartZ=0 EndX=2.9 EndY=-20.717 EndZ=0
    g2: LineSegment StartX=2.9 StartY=-20.717 StartZ=0 EndX=-2.9 EndY=-20.717 EndZ=0
    g3: LineSegment StartX=-2.9 StartY=-20.717 StartZ=0 EndX=-2.9 EndY=-14.717 EndZ=0
    g4: LineSegment StartX=2.9 StartY=-14.717 StartZ=0 EndX=-2.9 EndY=-14.717 EndZ=0
  constraints (14):
    c: Coincident(g0,g-1)
    c: Radius(g0) = 15
    c: Coincident(g1,g0)
    c: Vertical(g1)
    c: Coincident(g2,g1)
    c: Horizontal(g2)
    c: Coincident(g3,g2)
    c: Coincident(g3,g0)
    c: Vertical(g3)
    c: DistanceX(g2,g2) = 5.8
    c: Coincident(g4,g0)
    c: Coincident(g4,g0)
    c: Horizontal(g4)
    c: DistanceY(g1,g1) = 6
FEATURE [PartDesign::Pad] Pad020
  Direction = (0,0,1)
  Length = 1
  Length2 = 10
  Profile = -> Sketch040
  ReferenceAxis = -> Sketch040 [N_Axis]
  Type = 0
FEATURE [PartDesign::Body] Body018  label="Sensor004"
  Group = -> [Sketch040,Pad020]
  Origin = -> Origin019
  Placement = pos=(0,0,72) rot=(0,0,1;0rad)
  Tip = -> Pad020
FEATURE [PartDesign::FeatureBase] Clone003
  BaseFeature = -> Body018
FEATURE [PartDesign::Body] Body019  label="Sensor005"
  Group = -> [Clone003]
  Origin = -> Origin020
  Placement = pos=(0,0,-72) rot=(0,1,0;3.14159rad)
  Tip = -> Clone003
FEATURE [PartDesign::FeatureBase] Clone004
  BaseFeature = -> Body018
FEATURE [PartDesign::Body] Body020  label="Sensor006"
  Group = -> [Clone004]
  Origin = -> Origin021
  Placement = pos=(0,111,1.7e-14) rot=(0,0.707107,-0.707107;3.14159rad)
  Tip = -> Clone004
FEATURE [Sketcher::SketchObject] Sketch041
  FullyConstrained = true
  MapMode = 5
  Support = -> [XY_Plane022]
  sketch-geometry (1):
    g0: Circle CenterX=0 CenterY=0 CenterZ=0 NormalX=0 NormalY=0 NormalZ=1 AngleXU=0 Radius=26
  constraints (2):
    c: Coincident(g0,g-1)
    c: Diameter(g0) = 52
FEATURE [PartDesign::Pad] Pad021
  Direction = (0,0,1)
  Length = 20
  Length2 = 10
  Profile = -> Sketch041
  ReferenceAxis = -> Sketch041 [N_Axis]
  Type = 0
FEATURE [PartDesign::Body] Body021  label="Foam003"
  Group = -> [Sketch041,Pad021]
  Origin = -> Origin022
  Placement = pos=(0,0,108) rot=(0,0,1;0rad)
  Tip = -> Pad021
FEATURE [PartDesign::FeatureBase] Clone005
  BaseFeature = -> Body021
  Placement = pos=(0,0,38) rot=(0,0,1;0rad)
FEATURE [PartDesign::Body] Body022  label="Foam004"
  Group = -> [Clone005]
  Origin = -> Origin023
  Placement = pos=(0,0,-75) rot=(1,0,0;3.14159rad)
  Tip = -> Clone005
FEATURE [Sketcher::SketchObject] Sketch042
  FullyConstrained = true
  MapMode = 5
  Support = -> [XY_Plane024]
  sketch-geometry (5):
    g0: LineSegment StartX=-22.5 StartY=-0.4 StartZ=0 EndX=-22.5 EndY=0.4 EndZ=0
    g1: LineSegment StartX=-22.5 StartY=0.4 StartZ=0 EndX=22.5 EndY=0.4 EndZ=0
    g2: LineSegment StartX=22.5 StartY=0.4 StartZ=0 EndX=22.5 EndY=-0.4 EndZ=0
    g3: LineSegment StartX=22.5 StartY=-0.4 StartZ=0 EndX=-22.5 EndY=-0.4 EndZ=0
    g4: GeomPoint X=0 Y=0 Z=0
  constraints (12):
    c: Coincident(g0,g1)
    c: Coincident(g1,g2)
    c: Coincident(g2,g3)
    c: Coincident(g3,g0)
    c: Horizontal(g1)
    c: Horizontal(g3)
    c: Vertical(g0)
    c: Vertical(g2)
    c: Symmetric(g1,g0,g4)
    c: Coincident(g4,g-1)
    c: DistanceX(g1,g1) = 45
    c: DistanceY(g2,g2) = 0.8
FEATURE [PartDesign::Pad] Pad022
  Direction = (0,0,1)
  Length = 9
  Length2 = 9
  Profile = -> Sketch042
  ReferenceAxis = -> Sketch042 [N_Axis]
  Type = 4
FEATURE [PartDesign::Body] Body023  label="ShimStock001"
  Group = -> [Sketch042,Pad022]
  Origin = -> Origin024
  Placement = pos=(80,11,0) rot=(0,0,1;0rad)
  Tip = -> Pad022
FEATURE [Sketcher::SketchObject] Sketch043
  FullyConstrained = true
  MapMode = 5
  Placement = pos=(0,0,0) rot=(1,0,0;1.5708rad)
  Support = -> [XZ_Plane025]
  sketch-geometry (1):
    g0: Circle CenterX=0 CenterY=0 CenterZ=0 NormalX=0 NormalY=0 NormalZ=1 AngleXU=0 Radius=5
  constraints (2):
    c: Coincident(g0,g-1)
    c: Diameter(g0) = 10
FEATURE [PartDesign::Pad] Pad023
  Direction = (0,-1,-2e-16)
  Length = 3
  Length2 = 10
  Placement = pos=(0,0,0) rot=(1,0,0;1.5708rad)
  Profile = -> Sketch043
  ReferenceAxis = -> Sketch043 [N_Axis]
  Type = 0
FEATURE [PartDesign::Body] Body024  label="TopFoam001"
  Group = -> [Sketch043,Pad023]
  Origin = -> Origin025
  Placement = pos=(0,90,0) rot=(0,0,1;0rad)
  Tip = -> Pad023
FEATURE [Sketcher::SketchObject] Sketch044
  FullyConstrained = false
  MapMode = 5
  Support = -> [XY_Plane018]
  sketch-geometry (1):
    g0: Circle CenterX=0 CenterY=-15.4348 CenterZ=0 NormalX=0 NormalY=0 NormalZ=1 AngleXU=0 Radius=4
  constraints (2):
    c: PointOnObject(g0,g-2)
    c: Diameter(g0) = 8
FEATURE [PartDesign::Pocket] Pocket021
  BaseFeature = -> Pad019
  Direction = (0,0,-1)
  Length = 50
  Length2 = 50
  Placement = pos=(0,0,0) rot=(1,0,0;1.5708rad)
  Profile = -> Sketch044
  ReferenceAxis = -> Sketch044 [N_Axis]
  Type = 4
FEATURE [Sketcher::SketchObject] Sketch045
  FullyConstrained = true
  MapMode = 5
  Placement = pos=(0,0,0) rot=(1,0,0;1.5708rad)
  Support = -> [XZ_Plane018]
  sketch-geometry (17):
    g0: LineSegment StartX=12 StartY=-2 StartZ=0 EndX=12 EndY=2 EndZ=0
    g1: LineSegment StartX=12 StartY=2 StartZ=0 EndX=2 EndY=2 EndZ=0
    g2: LineSegment StartX=2 StartY=2 StartZ=0 EndX=2 EndY=12 EndZ=0
    g3: LineSegment StartX=2 StartY=12 StartZ=0 EndX=-2 EndY=12 EndZ=0
    g4: LineSegment StartX=-2 StartY=12 StartZ=0 EndX=-2 EndY=2 EndZ=0
    g5: LineSegment StartX=-2 StartY=2 StartZ=0 EndX=-12 EndY=2 EndZ=0
    g6: LineSegment StartX=-12 StartY=2 StartZ=0 EndX=-12 EndY=-2 EndZ=0
    g7: LineSegment StartX=-12 StartY=-2 StartZ=0 EndX=-2 EndY=-2 EndZ=0
    g8: LineSegment StartX=-2 StartY=-2 StartZ=0 EndX=-2 EndY=-12 EndZ=0
    g9: LineSegment StartX=-2 StartY=-12 StartZ=0 EndX=2 EndY=-12 EndZ=0
    g10: LineSegment StartX=2 StartY=-12 StartZ=0 EndX=2 EndY=-2 EndZ=0
    g11: LineSegment StartX=2 StartY=-2 StartZ=0 EndX=12 EndY=-2 EndZ=0
    g12: LineSegment StartX=-2 StartY=-2 StartZ=0 EndX=-2 EndY=2 EndZ=0
    g13: LineSegment StartX=-2 StartY=2 StartZ=0 EndX=2 EndY=2 EndZ=0
    g14: LineSegment StartX=2 StartY=2 StartZ=0 EndX=2 EndY=-2 EndZ=0
    g15: LineSegment StartX=2 StartY=-2 StartZ=0 EndX=-2 EndY=-2 EndZ=0
    g16: GeomPoint X=0 Y=0 Z=0
  constraints (46):
    c: Vertical(g0)
    c: Coincident(g1,g0)
    c: Horizontal(g1)
    c: Coincident(g2,g1)
    c: Vertical(g2)
    c: Coincident(g3,g2)
    c: Horizontal(g3)
    c: Coincident(g4,g3)
    c: Vertical(g4)
    c: Coincident(g5,g4)
    c: Horizontal(g5)
    c: Coincident(g6,g5)
    c: Vertical(g6)
    c: Horizontal(g7)
    c: Coincident(g8,g7)
    c: Vertical(g8)
    c: Horizontal(g9)
    c: Coincident(g10,g9)
    c: Vertical(g10)
    c: Coincident(g11,g10)
    c: Coincident(g11,g0)
    c: Horizontal(g11)
    c: Equal(g0,g3)
    c: Equal(g3,g6)
    c: Equal(g6,g9)
    c: Coincident(g6,g7)
    c: Coincident(g9,g8)
    c: Equal(g11,g7)
    c: Equal(g11,g1)
    c: Equal(g2,g4)
    c: Equal(g5,g10)
    c: Coincident(g12,g13)
    c: Coincident(g13,g14)
    c: Coincident(g14,g15)
    c: Coincident(g15,g12)
    c: Horizontal(g13)
    c: Horizontal(g15)
    c: Vertical(g12)
    c: Vertical(g14)
    c: Symmetric(g13,g12,g16)
    c: Coincident(g16,g-1)
    c: Coincident(g13,g1)
    c: Coincident(g7,g12)
    c: DistanceX(g13,g13) = 4
    c: DistanceY(g2,g2) = 10
    c: Equal(g10,g2)
FEATURE [PartDesign::Pocket] Pocket022
  BaseFeature = -> Pocket021
  Direction = (0,1,2e-16)
  Length = 3
  Length2 = 5
  Placement = pos=(0,0,0) rot=(1,0,0;1.5708rad)
  Profile = -> Sketch045
  ReferenceAxis = -> Sketch045 [N_Axis]
  Reversed = true
  Type = 0
FEATURE [PartDesign::Body] Body017  label="MetalHandle001"
  Group = -> [Sketch039,Pad019,Sketch044,Pocket021,Sketch045,Pocket022]
  Origin = -> Origin018
  Placement = pos=(0,-52.5,0) rot=(0,0,1;0rad)
  Tip = -> Pocket022
FEATURE [Sketcher::SketchObject] Sketch046
  FullyConstrained = true
  MapMode = 5
  Placement = pos=(0,0,0) rot=(1,0,0;1.5708rad)
  Support = -> [XZ_Plane026]
  expr: Constraints[43] = Sketch045.Constraints[43]
  expr: Constraints[44] = Sketch045.Constraints[44]
  expr: Constraints[77] = <<Properties001>>.Clearance
  expr: Constraints[78] = <<Properties001>>.Clearance
  expr: Constraints[79] = <<Properties001>>.Clearance
  expr: Constraints[81] = (<<Properties001>>.Handle_OD + 2) / 2 - <<Properties001>>.Clearance
  sketch-geometry (29):
    g0: LineSegment StartX=12 StartY=-2 StartZ=0 EndX=12 EndY=2 EndZ=0
    g1: LineSegment StartX=12 StartY=2 StartZ=0 EndX=2 EndY=2 EndZ=0
    g2: LineSegment StartX=2 StartY=2 StartZ=0 EndX=2 EndY=12 EndZ=0
    g3: LineSegment StartX=2 StartY=12 StartZ=0 EndX=-2 EndY=12 EndZ=0
    g4: LineSegment StartX=-2 StartY=12 StartZ=0 EndX=-2 EndY=2 EndZ=0
    g5: LineSegment StartX=-2 StartY=2 StartZ=0 EndX=-12 EndY=2 EndZ=0
    g6: LineSegment StartX=-12 StartY=2 StartZ=0 EndX=-12 EndY=-2 EndZ=0
    g7: LineSegment StartX=-12 StartY=-2 StartZ=0 EndX=-2 EndY=-2 EndZ=0
    g8: LineSegment StartX=-2 StartY=-2 StartZ=0 EndX=-2 EndY=-12 EndZ=0
    g9: LineSegment StartX=-2 StartY=-12 StartZ=0 EndX=2 EndY=-12 EndZ=0
    g10: LineSegment StartX=2 StartY=-12 StartZ=0 EndX=2 EndY=-2 EndZ=0
    g11: LineSegment StartX=2 StartY=-2 StartZ=0 EndX=12 EndY=-2 EndZ=0
    g12: LineSegment StartX=-2 StartY=-2 StartZ=0 EndX=-2 EndY=2 EndZ=0
    g13: LineSegment StartX=-2 StartY=2 StartZ=0 EndX=2 EndY=2 EndZ=0
    g14: LineSegment StartX=2 StartY=2 StartZ=0 EndX=2 EndY=-2 EndZ=0
    g15: LineSegment StartX=2 StartY=-2 StartZ=0 EndX=-2 EndY=-2 EndZ=0
    g16: GeomPoint X=0 Y=0 Z=0
    g17: LineSegment StartX=-1.8 StartY=11.55 StartZ=0 EndX=-1.8 EndY=1.8 EndZ=0
    g18: LineSegment StartX=-1.8 StartY=1.8 StartZ=0 EndX=-11.55 EndY=1.8 EndZ=0
    g19: LineSegment StartX=-11.55 StartY=1.8 StartZ=0 EndX=-11.55 EndY=-1.8 EndZ=0
    g20: LineSegment StartX=-11.55 StartY=-1.8 StartZ=0 EndX=-1.8 EndY=-1.8 EndZ=0
    g21: LineSegment StartX=-1.8 StartY=-1.8 StartZ=0 EndX=-1.8 EndY=-11.55 EndZ=0
    g22: LineSegment StartX=-1.8 StartY=-11.55 StartZ=0 EndX=1.8 EndY=-11.55 EndZ=0
    g23: LineSegment StartX=1.8 StartY=-11.55 StartZ=0 EndX=1.8 EndY=-1.8 EndZ=0
    g24: LineSegment StartX=1.8 StartY=-1.8 StartZ=0 EndX=11.55 EndY=-1.8 EndZ=0
    g25: LineSegment StartX=11.55 StartY=-1.8 StartZ=0 EndX=11.55 EndY=1.8 EndZ=0
    g26: LineSegment StartX=11.55 StartY=1.8 StartZ=0 EndX=1.8 EndY=1.8 EndZ=0
    g27: LineSegment StartX=1.8 StartY=1.8 StartZ=0 EndX=1.8 EndY=11.55 EndZ=0
    g28: LineSegment StartX=1.8 StartY=11.55 StartZ=0 EndX=-1.8 EndY=11.55 EndZ=0
  constraints (82):
    c: Vertical(g0)
    c: Coincident(g1,g0)
    c: Horizontal(g1)
    c: Coincident(g2,g1)
    c: Vertical(g2)
    c: Coincident(g3,g2)
    c: Horizontal(g3)
    c: Coincident(g4,g3)
    c: Vertical(g4)
    c: Coincident(g5,g4)
    c: Horizontal(g5)
    c: Coincident(g6,g5)
    c: Vertical(g6)
    c: Horizontal(g7)
    c: Coincident(g8,g7)
    c: Vertical(g8)
    c: Horizontal(g9)
    c: Coincident(g10,g9)
    c: Vertical(g10)
    c: Coincident(g11,g10)
    c: Coincident(g11,g0)
    c: Horizontal(g11)
    c: Equal(g0,g3)
    c: Equal(g3,g6)
    c: Equal(g6,g9)
    c: Coincident(g6,g7)
    c: Coincident(g9,g8)
    c: Equal(g11,g7)
    c: Equal(g11,g1)
    c: Equal(g2,g4)
    c: Equal(g5,g10)
    c: Coincident(g12,g13)
    c: Coincident(g13,g14)
    c: Coincident(g14,g15)
    c: Coincident(g15,g12)
    c: Horizontal(g13)
    c: Horizontal(g15)
    c: Vertical(g12)
    c: Vertical(g14)
    c: Symmetric(g13,g12,g16)
    c: Coincident(g16,g-1)
    c: Coincident(g13,g1)
    c: Coincident(g7,g12)
    c: DistanceX(g13,g13) = 4
    c: DistanceY(g2,g2) = 10
    c: Equal(g10,g2)
    c: Vertical(g17)
    c: Coincident(g18,g17)
    c: Horizontal(g18)
    c: Coincident(g19,g18)
    c: Vertical(g19)
    c: Coincident(g20,g19)
    c: Horizontal(g20)
    c: Coincident(g21,g20)
    c: Vertical(g21)
    c: Coincident(g22,g21)
    c: Horizontal(g22)
    c: Coincident(g23,g22)
    c: Vertical(g23)
    c: Coincident(g24,g23)
    c: Horizontal(g24)
    c: Coincident(g25,g24)
    c: Vertical(g25)
    c: Coincident(g26,g25)
    c: Horizontal(g26)
    c: Coincident(g27,g26)
    c: Vertical(g27)
    c: Coincident(g28,g27)
    c: Coincident(g28,g17)
    c: Horizontal(g28)
    c: Equal(g26,g18)
    c: Equal(g27,g17)
    c: Equal(g26,g24)
    c: Equal(g20,g24)
    c: Equal(g21,g23)
    c: Equal(g23,g27)
    c: Equal(g22,g25)
    c: DistanceX(g26,g1) = 0.2
    c: DistanceY(g26,g1) = 0.2
    c: DistanceY(g0,g24) = 0.2
    c: Equal(g23,g24)
    c: DistanceX(g16,g25) = 11.55
FEATURE [PartDesign::Pad] Pad024
  Direction = (0,-1,2e-16)
  Length = 2.8
  Length2 = 10
  Placement = pos=(0,0,0) rot=(1,0,0;1.5708rad)
  Profile = -> Sketch046
  ReferenceAxis = -> Sketch046 [N_Axis]
  Type = 0
FEATURE [Sketcher::SketchObject] Sketch047
  FullyConstrained = true
  MapMode = 5
  Placement = pos=(0,0,0) rot=(1,0,0;1.5708rad)
  Support = -> [XZ_Plane026]
  expr: Constraints[53] = Sketch046.Constraints[43]
  expr: Constraints[54] = Sketch046.Constraints[44]
  expr: Constraints[87] = Sketch046.Constraints[77]
  expr: Constraints[88] = Sketch046.Constraints[78]
  expr: Constraints[89] = Sketch046.Constraints[79]
  expr: Constraints[91] = Sketch046.Constraints[81]
  sketch-geometry (34):
    g0: LineSegment StartX=11.55 StartY=11.55 StartZ=0 EndX=11.55 EndY=-11.55 EndZ=0
    g1: LineSegment StartX=11.55 StartY=-11.55 StartZ=0 EndX=-11.55 EndY=-11.55 EndZ=0
    g2: LineSegment StartX=-11.55 StartY=-11.55 StartZ=0 EndX=-11.55 EndY=11.55 EndZ=0
    g3: LineSegment StartX=-11.55 StartY=11.55 StartZ=0 EndX=11.55 EndY=11.55 EndZ=0
    g4: GeomPoint X=0 Y=0 Z=0
    g5: LineSegment StartX=12 StartY=-2 StartZ=0 EndX=12 EndY=2 EndZ=0
    g6: LineSegment StartX=12 StartY=2 StartZ=0 EndX=2 EndY=2 EndZ=0
    g7: LineSegment StartX=2 StartY=2 StartZ=0 EndX=2 EndY=12 EndZ=0
    g8: LineSegment StartX=2 StartY=12 StartZ=0 EndX=-2 EndY=12 EndZ=0
    g9: LineSegment StartX=-2 StartY=12 StartZ=0 EndX=-2 EndY=2 EndZ=0
    g10: LineSegment StartX=-2 StartY=2 StartZ=0 EndX=-12 EndY=2 EndZ=0
    g11: LineSegment StartX=-12 StartY=2 StartZ=0 EndX=-12 EndY=-2 EndZ=0
    g12: LineSegment StartX=-12 StartY=-2 StartZ=0 EndX=-2 EndY=-2 EndZ=0
    g13: LineSegment StartX=-2 StartY=-2 StartZ=0 EndX=-2 EndY=-12 EndZ=0
    g14: LineSegment StartX=-2 StartY=-12 StartZ=0 EndX=2 EndY=-12 EndZ=0
    g15: LineSegment StartX=2 StartY=-12 StartZ=0 EndX=2 EndY=-2 EndZ=0
    g16: LineSegment StartX=2 StartY=-2 StartZ=0 EndX=12 EndY=-2 EndZ=0
    g17: LineSegment StartX=-2 StartY=-2 StartZ=0 EndX=-2 EndY=2 EndZ=0
    g18: LineSegment StartX=-2 StartY=2 StartZ=0 EndX=2 EndY=2 EndZ=0
    g19: LineSegment StartX=2 StartY=2 StartZ=0 EndX=2 EndY=-2 EndZ=0
    g20: LineSegment StartX=2 StartY=-2 StartZ=0 EndX=-2 EndY=-2 EndZ=0
    g21: GeomPoint X=0 Y=0 Z=0
    g22: LineSegment StartX=-1.8 StartY=11.55 StartZ=0 EndX=-1.8 EndY=1.8 EndZ=0
    g23: LineSegment StartX=-1.8 StartY=1.8 StartZ=0 EndX=-11.55 EndY=1.8 EndZ=0
    g24: LineSegment StartX=-11.55 StartY=1.8 StartZ=0 EndX=-11.55 EndY=-1.8 EndZ=0
    g25: LineSegment StartX=-11.55 StartY=-1.8 StartZ=0 EndX=-1.8 EndY=-1.8 EndZ=0
    g26: LineSegment StartX=-1.8 StartY=-1.8 StartZ=0 EndX=-1.8 EndY=-11.55 EndZ=0
    g27: LineSegment StartX=-1.8 StartY=-11.55 StartZ=0 EndX=1.8 EndY=-11.55 EndZ=0
    g28: LineSegment StartX=1.8 StartY=-11.55 StartZ=0 EndX=1.8 EndY=-1.8 EndZ=0
    g29: LineSegment StartX=1.8 StartY=-1.8 StartZ=0 EndX=11.55 EndY=-1.8 EndZ=0
    g30: LineSegment StartX=11.55 StartY=-1.8 StartZ=0 EndX=11.55 EndY=1.8 EndZ=0
    g31: LineSegment StartX=11.55 StartY=1.8 StartZ=0 EndX=1.8 EndY=1.8 EndZ=0
    g32: LineSegment StartX=1.8 StartY=1.8 StartZ=0 EndX=1.8 EndY=11.55 EndZ=0
    g33: LineSegment StartX=1.8 StartY=11.55 StartZ=0 EndX=-1.8 EndY=11.55 EndZ=0
  constraints (94):
    c: Coincident(g0,g1)
    c: Coincident(g1,g2)
    c: Coincident(g2,g3)
    c: Coincident(g3,g0)
    c: Horizontal(g1)
    c: Horizontal(g3)
    c: Vertical(g0)
    c: Vertical(g2)
    c: Symmetric(g1,g0,g4)
    c: Coincident(g4,g-1)
    c: Vertical(g5)
    c: Coincident(g6,g5)
    c: Horizontal(g6)
    c: Coincident(g7,g6)
    c: Vertical(g7)
    c: Coincident(g8,g7)
    c: Horizontal(g8)
    c: Coincident(g9,g8)
    c: Vertical(g9)
    c: Coincident(g10,g9)
    c: Horizontal(g10)
    c: Coincident(g11,g10)
    c: Vertical(g11)
    c: Horizontal(g12)
    c: Coincident(g13,g12)
    c: Vertical(g13)
    c: Horizontal(g14)
    c: Coincident(g15,g14)
    c: Vertical(g15)
    c: Coincident(g16,g15)
    c: Coincident(g16,g5)
    c: Horizontal(g16)
    c: Equal(g5,g8)
    c: Equal(g8,g11)
    c: Equal(g11,g14)
    c: Coincident(g11,g12)
    c: Coincident(g14,g13)
    c: Equal(g16,g12)
    c: Equal(g16,g6)
    c: Equal(g7,g9)
    c: Equal(g10,g15)
    c: Coincident(g17,g18)
    c: Coincident(g18,g19)
    c: Coincident(g19,g20)
    c: Coincident(g20,g17)
    c: Horizontal(g18)
    c: Horizontal(g20)
    c: Vertical(g17)
    c: Vertical(g19)
    c: Symmetric(g18,g17,g21)
    c: Coincident(g21,g-1)
    c: Coincident(g18,g6)
    c: Coincident(g12,g17)
    c: DistanceX(g18,g18) = 4
    c: DistanceY(g7,g7) = 10
    c: Equal(g15,g7)
    c: Vertical(g22)
    c: Coincident(g23,g22)
    c: Horizontal(g23)
    c: Coincident(g24,g23)
    c: Vertical(g24)
    c: Coincident(g25,g24)
    c: Horizontal(g25)
    c: Coincident(g26,g25)
    c: Vertical(g26)
    c: Coincident(g27,g26)
    c: Horizontal(g27)
    c: Coincident(g28,g27)
    c: Vertical(g28)
    c: Coincident(g29,g28)
    c: Horizontal(g29)
    c: Coincident(g30,g29)
    c: Vertical(g30)
    c: Coincident(g31,g30)
    c: Horizontal(g31)
    c: Coincident(g32,g31)
    c: Vertical(g32)
    c: Coincident(g33,g32)
    c: Coincident(g33,g22)
    c: Horizontal(g33)
    c: Equal(g31,g23)
    c: Equal(g32,g22)
    c: Equal(g31,g29)
    c: Equal(g25,g29)
    c: Equal(g26,g28)
    c: Equal(g28,g32)
    c: Equal(g27,g30)
    c: DistanceX(g31,g6) = 0.2
    c: DistanceY(g31,g6) = 0.2
    c: DistanceY(g5,g29) = 0.2
    c: Equal(g28,g29)
    c: DistanceX(g21,g30) = 11.55
    c: PointOnObject(g22,g3)
    c: PointOnObject(g23,g2)
FEATURE [PartDesign::Pad] Pad025
  BaseFeature = -> Pad024
  Direction = (0,-1,2e-16)
  Length = 5
  Length2 = 10
  Placement = pos=(0,0,0) rot=(1,0,0;1.5708rad)
  Profile = -> Sketch047
  ReferenceAxis = -> Sketch047 [N_Axis]
  Reversed = true
  Type = 0
FEATURE [Sketcher::SketchObject] Sketch048
  ExternalGeometry = -> [Cone003]
  FullyConstrained = true
  MapMode = 5
  Placement = pos=(2.3e-15,10.5,-35) rot=(-1,0,0;1.5708rad)
  Support = -> [Cone003]
  expr: Constraints[11] = <<Properties001>>.Handle_OD + 2
  sketch-geometry (5):
    g0: LineSegment StartX=-11.75 StartY=-46.75 StartZ=0 EndX=-11.75 EndY=-23.25 EndZ=0
    g1: LineSegment StartX=-11.75 StartY=-23.25 StartZ=0 EndX=11.75 EndY=-23.25 EndZ=0
    g2: LineSegment StartX=11.75 StartY=-23.25 StartZ=0 EndX=11.75 EndY=-46.75 EndZ=0
    g3: LineSegment StartX=11.75 StartY=-46.75 StartZ=0 EndX=-11.75 EndY=-46.75 EndZ=0
    g4: GeomPoint X=-2.3e-15 Y=-35 Z=0
  constraints (12):
    c: Coincident(g0,g1)
    c: Coincident(g1,g2)
    c: Coincident(g2,g3)
    c: Coincident(g3,g0)
    c: Horizontal(g1)
    c: Horizontal(g3)
    c: Vertical(g0)
    c: Vertical(g2)
    c: Symmetric(g1,g0,g4)
    c: Coincident(g4,g-3)
    c: Equal(g2,g1)
    c: DistanceX(g1,g1) = 23.5
FEATURE [PartDesign::Pocket] Pocket023
  BaseFeature = -> Cone003
  Direction = (-2e-16,-1,2e-16)
  Length = 8
  Length2 = 5
  Placement = pos=(0,0,-35) rot=(1,0,0;3.14159rad)
  Profile = -> Sketch048
  ReferenceAxis = -> Sketch048 [N_Axis]
  Type = 0
FEATURE [Sketcher::SketchObject] Sketch049
  FullyConstrained = true
  MapMode = 5
  Placement = pos=(0,5,-2.2e-15) rot=(-1,0,0;1.5708rad)
  Support = -> [Pad025]
  sketch-geometry (1):
    g0: Circle CenterX=0 CenterY=0 CenterZ=0 NormalX=0 NormalY=0 NormalZ=1 AngleXU=0 Radius=2.5
  constraints (2):
    c: Coincident(g0,g-1)
    c: Diameter(g0) = 5
FEATURE [PartDesign::Pad] Pad026
  BaseFeature = -> Pad025
  Direction = (0,1,-2e-16)
  Length = 3
  Length2 = 10
  Placement = pos=(0,0,0) rot=(1,0,0;1.5708rad)
  Profile = -> Sketch049
  ReferenceAxis = -> Sketch049 [N_Axis]
  Type = 0
FEATURE [PartDesign::Fillet] Fillet002
  Base = -> Pad026 [Edge51]
  BaseFeature = -> Pad026
  Placement = pos=(0,0,0) rot=(1,0,0;1.5708rad)
  Radius = 2
  SupportTransform = false
  UseAllEdges = false
FEATURE [PartDesign::Fillet] Fillet003
  Base = -> Fillet002 [Edge3]
  BaseFeature = -> Fillet002
  Placement = pos=(0,0,0) rot=(1,0,0;1.5708rad)
  Radius = 7
  SupportTransform = false
  UseAllEdges = false
FEATURE [Sketcher::SketchObject] Sketch050
  ExternalGeometry = -> [Cone003]
  FullyConstrained = true
  MapMode = 5
  Placement = pos=(6e-16,2.5,-35) rot=(-1,0,0;1.5708rad)
  Support = -> [Pocket023]
  expr: Constraints[11] = Sketch048.Constraints[11]
  expr: Constraints[54] = Sketch045.Constraints[43]
  expr: Constraints[55] = Sketch045.Constraints[44]
  sketch-geometry (34):
    g0: LineSegment StartX=-11.75 StartY=-46.75 StartZ=0 EndX=-11.75 EndY=-23.25 EndZ=0
    g1: LineSegment StartX=-11.75 StartY=-23.25 StartZ=0 EndX=11.75 EndY=-23.25 EndZ=0
    g2: LineSegment StartX=11.75 StartY=-23.25 StartZ=0 EndX=11.75 EndY=-46.75 EndZ=0
    g3: LineSegment StartX=11.75 StartY=-46.75 StartZ=0 EndX=-11.75 EndY=-46.75 EndZ=0
    g4: GeomPoint X=-2.4e-15 Y=-35 Z=0
    g5: LineSegment StartX=12 StartY=-37 StartZ=0 EndX=12 EndY=-33 EndZ=0
    g6: LineSegment StartX=12 StartY=-33 StartZ=0 EndX=2 EndY=-33 EndZ=0
    g7: LineSegment StartX=2 StartY=-33 StartZ=0 EndX=2 EndY=-23 EndZ=0
    g8: LineSegment StartX=2 StartY=-23 StartZ=0 EndX=-2 EndY=-23 EndZ=0
    g9: LineSegment StartX=-2 StartY=-23 StartZ=0 EndX=-2 EndY=-33 EndZ=0
    g10: LineSegment StartX=-2 StartY=-33 StartZ=0 EndX=-12 EndY=-33 EndZ=0
    g11: LineSegment StartX=-12 StartY=-33 StartZ=0 EndX=-12 EndY=-37 EndZ=0
    g12: LineSegment StartX=-12 StartY=-37 StartZ=0 EndX=-2 EndY=-37 EndZ=0
    g13: LineSegment StartX=-2 StartY=-37 StartZ=0 EndX=-2 EndY=-47 EndZ=0
    g14: LineSegment StartX=-2 StartY=-47 StartZ=0 EndX=2 EndY=-47 EndZ=0
    g15: LineSegment StartX=2 StartY=-47 StartZ=0 EndX=2 EndY=-37 EndZ=0
    g16: LineSegment StartX=2 StartY=-37 StartZ=0 EndX=12 EndY=-37 EndZ=0
    g17: LineSegment StartX=-2 StartY=-37 StartZ=0 EndX=-2 EndY=-33 EndZ=0
    g18: LineSegment StartX=-2 StartY=-33 StartZ=0 EndX=2 EndY=-33 EndZ=0
    g19: LineSegment StartX=2 StartY=-33 StartZ=0 EndX=2 EndY=-37 EndZ=0
    g20: LineSegment StartX=2 StartY=-37 StartZ=0 EndX=-2 EndY=-37 EndZ=0
    g21: GeomPoint X=0 Y=0 Z=0
    g22: LineSegment StartX=-2 StartY=-23.25 StartZ=0 EndX=2 EndY=-23.25 EndZ=0
    g23: LineSegment StartX=2 StartY=-23.25 StartZ=0 EndX=2 EndY=-33 EndZ=0
    g24: LineSegment StartX=2 StartY=-33 StartZ=0 EndX=11.75 EndY=-33 EndZ=0
    g25: LineSegment StartX=11.75 StartY=-33 StartZ=0 EndX=11.75 EndY=-37 EndZ=0
    g26: LineSegment StartX=11.75 StartY=-37 StartZ=0 EndX=2 EndY=-37 EndZ=0
    g27: LineSegment StartX=2 StartY=-37 StartZ=0 EndX=2 EndY=-46.75 EndZ=0
    g28: LineSegment StartX=2 StartY=-46.75 StartZ=0 EndX=-2 EndY=-46.75 EndZ=0
    g29: LineSegment StartX=-2 StartY=-46.75 StartZ=0 EndX=-2 EndY=-37 EndZ=0
    g30: LineSegment StartX=-2 StartY=-37 StartZ=0 EndX=-11.75 EndY=-37 EndZ=0
    g31: LineSegment StartX=-11.75 StartY=-37 StartZ=0 EndX=-11.75 EndY=-33 EndZ=0
    g32: LineSegment StartX=-11.75 StartY=-33 StartZ=0 EndX=-2 EndY=-33 EndZ=0
    g33: LineSegment StartX=-2 StartY=-33 StartZ=0 EndX=-2 EndY=-23.25 EndZ=0
  constraints (90):
    c: Coincident(g0,g1)
    c: Coincident(g1,g2)
    c: Coincident(g2,g3)
    c: Coincident(g3,g0)
    c: Horizontal(g1)
    c: Horizontal(g3)
    c: Vertical(g0)
    c: Vertical(g2)
    c: Symmetric(g1,g0,g4)
    c: Coincident(g4,g-3)
    c: Equal(g2,g1)
    c: DistanceX(g1,g1) = 23.5
    c: Vertical(g5)
    c: Coincident(g6,g5)
    c: Horizontal(g6)
    c: Coincident(g7,g6)
    c: Vertical(g7)
    c: Coincident(g8,g7)
    c: Horizontal(g8)
    c: Coincident(g9,g8)
    c: Vertical(g9)
    c: Coincident(g10,g9)
    c: Horizontal(g10)
    c: Coincident(g11,g10)
    c: Vertical(g11)
    c: Horizontal(g12)
    c: Coincident(g13,g12)
    c: Vertical(g13)
    c: Horizontal(g14)
    c: Coincident(g15,g14)
    c: Vertical(g15)
    c: Coincident(g16,g15)
    c: Coincident(g16,g5)
    c: Horizontal(g16)
    c: Equal(g5,g8)
    c: Equal(g8,g11)
    c: Equal(g11,g14)
    c: Coincident(g11,g12)
    c: Coincident(g14,g13)
    c: Equal(g16,g12)
    c: Equal(g16,g6)
    c: Equal(g7,g9)
    c: Equal(g10,g15)
    c: Coincident(g17,g18)
    c: Coincident(g18,g19)
    c: Coincident(g19,g20)
    c: Coincident(g20,g17)
    c: Horizontal(g18)
    c: Horizontal(g20)
    c: Vertical(g17)
    c: Vertical(g19)
    c: Coincident(g21,g-1)
    c: Coincident(g18,g6)
    c: Coincident(g12,g17)
    c: DistanceX(g18,g18) = 4
    c: DistanceY(g7,g7) = 10
    c: Equal(g15,g7)
    c: Symmetric(g6,g12,g4)
    c: PointOnObject(g22,g9)
    c: PointOnObject(g22,g1)
    c: Horizontal(g22)
    c: PointOnObject(g22,g7)
    c: Coincident(g23,g22)
    c: Coincident(g23,g6)
    c: Coincident(g24,g23)
    c: PointOnObject(g24,g2)
    c: Horizontal(g24)
    c: Coincident(g25,g24)
    c: PointOnObject(g25,g16)
    c: Vertical(g25)
    c: Coincident(g26,g25)
    c: Coincident(g26,g15)
    c: Coincident(g27,g26)
    c: PointOnObject(g27,g3)
    c: Vertical(g27)
    c: Coincident(g28,g27)
    c: PointOnObject(g28,g13)
    c: Horizontal(g28)
    c: Coincident(g29,g28)
    c: Coincident(g29,g12)
    c: Coincident(g30,g29)
    c: PointOnObject(g30,g0)
    c: Horizontal(g30)
    c: Coincident(g31,g30)
    c: PointOnObject(g31,g10)
    c: Vertical(g31)
    c: Coincident(g32,g31)
    c: Coincident(g32,g9)
    c: Coincident(g33,g32)
    c: Coincident(g33,g22)
FEATURE [PartDesign::Pocket] Pocket024
  BaseFeature = -> Pocket023
  Direction = (-2e-16,-1,2e-16)
  Length = 3
  Length2 = 5
  Placement = pos=(0,0,-35) rot=(1,0,0;3.14159rad)
  Profile = -> Sketch050
  ReferenceAxis = -> Sketch050 [N_Axis]
  Type = 0
FEATURE [PartDesign::Body] Body014  label="HeadInstert001"
  Group = -> [Sketch028,Pad016,Sketch029,Pocket013,Sketch030,Pocket014,Sketch032,Pocket015,Chamfer007,Sketch031,Pocket016,Chamfer008,Sketch036,Pocket019,Chamfer010,Chamfer011,Chamfer012,Cone002,Cone003,Sketch048,Pocket023,Sketch050,Pocket024]
  Origin = -> Origin016
  Tip = -> Pocket024
FEATURE [Sketcher::SketchObject] Sketch051
  FullyConstrained = true
  MapMode = 5
  Placement = pos=(0,0,0) rot=(1,0,0;1.5708rad)
  Support = -> [XZ_Plane026]
  expr: Constraints[1] = <<Properties001>>.Handle_OD - <<Properties001>>.Clearance * 2
  sketch-geometry (1):
    g0: Circle CenterX=0 CenterY=0 CenterZ=0 NormalX=0 NormalY=0 NormalZ=1 AngleXU=0 Radius=10.55
  constraints (2):
    c: Coincident(g0,g-1)
    c: Diameter(g0) = 21.1
FEATURE [PartDesign::Pad] Pad027
  BaseFeature = -> Fillet003
  Direction = (0,-1,2e-16)
  Length = 9
  Length2 = 10
  Placement = pos=(0,0,0) rot=(1,0,0;1.5708rad)
  Profile = -> Sketch051
  ReferenceAxis = -> Sketch051 [N_Axis]
  TaperAngle = -2
  Type = 0
FEATURE [PartDesign::Chamfer] Chamfer013
  Angle = 45
  Base = -> Pad027 [Edge15,Edge19,Edge10,Edge11]
  BaseFeature = -> Pad027
  ChamferType = 0
  FlipDirection = false
  Placement = pos=(0,0,0) rot=(1,0,0;1.5708rad)
  Size = 1
  Size2 = 1
  SupportTransform = false
  UseAllEdges = false
FEATURE [PartDesign::Body] Body025  label="Pusher001"
  Group = -> [Sketch046,Pad024,Sketch047,Pad025,Sketch049,Pad026,Fillet002,Fillet003,Sketch051,Pad027,Chamfer013]
  Origin = -> Origin026
  Placement = pos=(0,62.5,0) rot=(0,0,1;0rad)
  Tip = -> Chamfer013
FEATURE [Sketcher::SketchObject] Sketch052
  FullyConstrained = true
  MapMode = 5
  Placement = pos=(0,0,0) rot=(1,0,0;1.5708rad)
  Support = -> [XZ_Plane027]
  expr: Constraints[1] = <<Properties001>>.Handle_OD - 1
  sketch-geometry (2):
    g0: Circle CenterX=0 CenterY=0 CenterZ=0 NormalX=0 NormalY=0 NormalZ=1 AngleXU=0 Radius=10.25
    g1: Circle CenterX=0 CenterY=0 CenterZ=0 NormalX=0 NormalY=0 NormalZ=1 AngleXU=0 Radius=4
  constraints (4):
    c: Coincident(g0,g-1)
    c: Diameter(g0) = 20.5
    c: Coincident(g1,g0)
    c: Diameter(g1) = 8
FEATURE [PartDesign::Pad] Pad028
  Direction = (0,-1,-2e-16)
  Length = 10
  Length2 = 10
  Placement = pos=(0,0,0) rot=(1,0,0;1.5708rad)
  Profile = -> Sketch052
  ReferenceAxis = -> Sketch052 [N_Axis]
  Type = 0
FEATURE [PartDesign::Draft] Draft001
  Angle = 2
  Base = -> Pad028 [Face1]
  BaseFeature = -> Pad028
  NeutralPlane = -> Pad028 [Face3]
  Placement = pos=(0,0,0) rot=(1,0,0;1.5708rad)
  SupportTransform = false
FEATURE [PartDesign::Body] Body026  label="WirePlug001"
  Group = -> [Sketch052,Pad028,Draft001]
  Origin = -> Origin027
  Placement = pos=(0,-275,0) rot=(0,0,1;0rad)
  Tip = -> Draft001
FEATURE [Sketcher::SketchObject] Sketch053
  FullyConstrained = true
  MapMode = 5
  Placement = pos=(0,0,0) rot=(1,0,0;1.5708rad)
  Support = -> [XZ_Plane017]
  sketch-geometry (5):
    g0: LineSegment StartX=-2.5 StartY=-45 StartZ=0 EndX=-2.5 EndY=45 EndZ=0
    g1: LineSegment StartX=-2.5 StartY=45 StartZ=0 EndX=2.5 EndY=45 EndZ=0
    g2: LineSegment StartX=2.5 StartY=45 StartZ=0 EndX=2.5 EndY=-45 EndZ=0
    g3: LineSegment StartX=2.5 StartY=-45 StartZ=0 EndX=-2.5 EndY=-45 EndZ=0
    g4: GeomPoint X=0 Y=0 Z=0
  constraints (12):
    c: Coincident(g0,g1)
    c: Coincident(g1,g2)
    c: Coincident(g2,g3)
    c: Coincident(g3,g0)
    c: Horizontal(g1)
    c: Horizontal(g3)
    c: Vertical(g0)
    c: Vertical(g2)
    c: Symmetric(g1,g0,g4)
    c: Coincident(g4,g-1)
    c: DistanceX(g1,g1) = 5
    c: DistanceY(g2,g2) = 90
FEATURE [PartDesign::Pocket] Pocket025
  BaseFeature = -> Pocket020
  Direction = (0,1,2e-16)
  Length = 5
  Length2 = 5
  Profile = -> Sketch053
  ReferenceAxis = -> Sketch053 [N_Axis]
  Reversed = true
  Type = 1
FEATURE [PartDesign::Body] Body016  label="PVCHammerHeadShell001"
  Group = -> [Sketch037,Pad018,Sketch038,Pocket020,Sketch053,Pocket025]
  Origin = -> Origin017
  Placement = pos=(0,0,220) rot=(0,0,1;0rad)
  Tip = -> Pocket025
FEATURE [App::DocumentObjectGroup] Group002  label="Non3DPrints001"
  Group = -> [Body020,Body019,Body018,Body017,Body016,Body021,Body022,Body023,Body024]
FEATURE [App::Part] Part001  label="PartExploded"
  Group = -> [Body014,Body015,Body016,Body017,Body018,Body019,Body020,Body021,Body022,Body023,Body024,Group002,Body025,Body026]
  Origin = -> Origin028
FEATURE [Spreadsheet::Sheet] Spreadsheet002  label="Properties001"
  cells = A1='PropertyName; B1='Value; A2='Handle_OD; B2(Handle_OD)=21.5; A3='Head_ID; B3(Head_ID)=51.4; A4='Head_Len; B4(Handle_Len)=110; A5='Clearance; B5(Clearance)=0.2; A6='Inset_Len; B6(Insert_Len)=70; A7='Sensor_Wire_Track_Width; B7(Sensor_Wire_Track_Width)=8; A8='Spring_Plate_Len; B8(Spring_Plate_Len)=46; A9='Sensor_Diameter; B9(Sensor_Diameter)=30; A10='Handle_ID; B10(Handle_ID)=20.5
FEATURE [TechDraw::DrawProjGroupItem] ProjItem  label="Front"
  CoarseView = false
  Direction = (0.57735,0.57735,-0.57735)
  Focus = 100
  HardHidden = false
  IsoCount = 0
  IsoHidden = false
  IsoVisible = false
  LockPosition = true
  Perspective = false
  Rotation = 0
  RotationVector = (-0.707106,0,-0.707106)
  ScaleType = 2
  ScrubCount = 0
  SeamHidden = false
  SeamVisible = false
  SmoothHidden = false
  SmoothVisible = true
  Source = -> [Part001]
  Type = 0
  X = 0
  XDirection = (-0.707106,0,-0.707106)
  Y = 0
FEATURE [TechDraw::DrawProjGroup] ProjGroup
  Anchor = -> ProjItem
  AutoDistribute = true
  LockPosition = false
  ProjectionType = 1
  Rotation = 0
  Scale = 0.5
  ScaleType = 0
  Source = -> [Part001]
  Views = -> [ProjItem]
  X = 96.5675
  Y = 146.729
  spacingX = 15
  spacingY = 15
FEATURE [TechDraw::DrawViewBalloon] Balloon
  BubbleShape = 0
  EndType = 0
  EndTypeScale = 1
  KinkLength = 5
  LockPosition = false
  OriginX = -138.132
  OriginY = 182.717
  Rotation = 0
  Scale = 0.5
  ScaleType = 0
  ShapeScale = 1
  SourceView = -> ProjItem
  Text = 1
  TextWrapLen = -1
  X = -98.132
  Y = 222.717
FEATURE [TechDraw::DrawViewBalloon] Balloon004
  BubbleShape = 0
  EndType = 0
  EndTypeScale = 1
  KinkLength = 5
  LockPosition = false
  OriginX = -36.6198
  OriginY = 124.71
  Rotation = 0
  Scale = 0.5
  ScaleType = 0
  ShapeScale = 1
  SourceView = -> ProjItem
  Text = 2
  TextWrapLen = -1
  X = -62.0848
  Y = 222.717
FEATURE [TechDraw::DrawViewBalloon] Balloon005
  BubbleShape = 0
  EndType = 0
  EndTypeScale = 1
  KinkLength = 5
  LockPosition = false
  OriginX = 31.7456
  OriginY = 183.546
  Rotation = 0
  Scale = 0.5
  ScaleType = 0
  ShapeScale = 1
  SourceView = -> ProjItem
  Text = 3
  TextWrapLen = -1
  X = -12.6753
  Y = 222.095
FEATURE [TechDraw::DrawViewBalloon] Balloon006
  BubbleShape = 0
  EndType = 0
  EndTypeScale = 1
  KinkLength = 5
  LockPosition = false
  OriginX = 63.2351
  OriginY = 139.626
  Rotation = 0
  Scale = 0.5
  ScaleType = 0
  ShapeScale = 1
  SourceView = -> ProjItem
  Text = 4
  TextWrapLen = -1
  X = 186.931
  Y = 169.268
FEATURE [TechDraw::DrawViewBalloon] Balloon007
  BubbleShape = 0
  EndType = 0
  EndTypeScale = 1
  KinkLength = 5
  LockPosition = false
  OriginX = 53.291
  OriginY = 121.395
  Rotation = 0
  Scale = 0.5
  ScaleType = 0
  ShapeScale = 1
  SourceView = -> ProjItem
  Text = 5
  TextWrapLen = -1
  X = 186.931
  Y = 132.806
FEATURE [TechDraw::DrawViewBalloon] Balloon008
  BubbleShape = 0
  EndType = 0
  EndTypeScale = 1
  KinkLength = 5
  LockPosition = false
  OriginX = 64.0638
  OriginY = 104.408
  Rotation = 0
  Scale = 0.5
  ScaleType = 0
  ShapeScale = 1
  SourceView = -> ProjItem
  Text = 6
  TextWrapLen = -1
  X = 187.345
  Y = 94.6873
FEATURE [TechDraw::DrawViewBalloon] Balloon009
  BubbleShape = 0
  EndType = 0
  EndTypeScale = 1
  KinkLength = 5
  LockPosition = false
  OriginX = 73.1791
  OriginY = 65.0457
  Rotation = 0
  Scale = 0.5
  ScaleType = 0
  ShapeScale = 1
  SourceView = -> ProjItem
  Text = 7
  TextWrapLen = -1
  X = 187.76
  Y = 54.4967
FEATURE [TechDraw::DrawViewBalloon] Balloon010
  BubbleShape = 0
  EndType = 0
  EndTypeScale = 1
  KinkLength = 5
  LockPosition = false
  OriginX = 59.5061
  OriginY = -63.8127
  Rotation = 0
  Scale = 0.5
  ScaleType = 0
  ShapeScale = 1
  SourceView = -> ProjItem
  Text = 8
  TextWrapLen = -1
  X = 186.931
  Y = -54.8878
FEATURE [TechDraw::DrawViewBalloon] Balloon011
  BubbleShape = 0
  EndType = 0
  EndTypeScale = 1
  KinkLength = 5
  LockPosition = false
  OriginX = 58.6774
  OriginY = -176.098
  Rotation = 0
  Scale = 0.5
  ScaleType = 0
  ShapeScale = 1
  SourceView = -> ProjItem
  Text = 9
  TextWrapLen = -1
  X = 188.174
  Y = -129.883
FEATURE [TechDraw::DrawViewBalloon] Balloon012
  BubbleShape = 0
  EndType = 0
  EndTypeScale = 1
  KinkLength = 5
  LockPosition = false
  OriginX = -23.2574
  OriginY = 15.7398
  Rotation = 0
  Scale = 0.5
  ScaleType = 0
  ShapeScale = 1
  SourceView = -> ProjItem
  Text = 10
  TextWrapLen = -1
  X = -59.9095
  Y = -229.634
FEATURE [TechDraw::DrawPage] Page004  label="Exploded"
  KeepUpdated = true
  NextBalloonIndex = 11
  ProjectionType = 1
  Scale = 0.5
  Template = -> Template004
  Views = -> [Sheet,Balloon001,Balloon003,ProjGroup,Balloon,Balloon004,Balloon005,Balloon006,Balloon007,Balloon008,Balloon009,Balloon010,Balloon011,Balloon012]
FEATURE [App::DocumentObjectGroup] Group001  label="Hammer Exploded"
  Group = -> [Page004,Spreadsheet001,Balloon,Balloon004,Balloon005,Balloon006,Balloon007,Balloon008,Balloon009,Balloon010,Balloon011,Balloon012]
FEATURE [TechDraw::DrawSVGTemplate] Template
  EditableTexts = AuthorName=Alex Anastasakis; CheckDate=2024/11/11; CreationDate=2024/11/10; FC-Scale=1:2; FC-Title=Hammer; SheetNumber=2 of 2; Subtitle=Course: Industrial Design for Game Hardware; SupervisorName=Alvaro Uribe Quevedo
  Height = 297
  Orientation = 1
  Template = C:/Program Files/FreeCAD 0.21/data/Mod/TechDraw/Templates/A3_LandscapeTD.svg
  Width = 420
FEATURE [TechDraw::DrawProjGroupItem] ProjItem001  label="Front001"
  CoarseView = false
  Direction = (1,0,0)
  Focus = 100
  HardHidden = false
  IsoCount = 0
  IsoHidden = false
  IsoVisible = false
  LockPosition = true
  Perspective = false
  Rotation = 0
  RotationVector = (0,0,-1)
  Scale = 0.5
  ScaleType = 2
  ScrubCount = 0
  SeamHidden = false
  SeamVisible = false
  SmoothHidden = false
  SmoothVisible = true
  Source = -> [Part]
  Type = 0
  X = 0
  XDirection = (0,0,-1)
  Y = 0
FEATURE [TechDraw::DrawProjGroupItem] ProjItem002  label="Right"
  CoarseView = false
  Direction = (1e-16,0,-1)
  Focus = 100
  HardHidden = false
  IsoCount = 0
  IsoHidden = false
  IsoVisible = false
  LockPosition = false
  Perspective = false
  Rotation = 0
  RotationVector = (1,0,0)
  Scale = 0.5
  ScaleType = 2
  ScrubCount = 0
  SeamHidden = false
  SeamVisible = false
  SmoothHidden = false
  SmoothVisible = true
  Source = -> [Part]
  Type = 2
  X = 59
  XDirection = (-1,0,-1e-16)
  Y = 0
FEATURE [TechDraw::DrawProjGroupItem] ProjItem004  label="FrontBottomLeft"
  CoarseView = false
  Direction = (0.57735,-0.57735,0.57735)
  Focus = 100
  HardHidden = false
  IsoCount = 0
  IsoHidden = false
  IsoVisible = false
  LockPosition = false
  Perspective = false
  Rotation = 0
  RotationVector = (1,0,0)
  Scale = 0.5
  ScaleType = 2
  ScrubCount = 0
  SeamHidden = false
  SeamVisible = false
  SmoothHidden = false
  SmoothVisible = true
  Source = -> [Part]
  Type = 8
  X = -73.6985
  XDirection = (0.707107,0,-0.707107)
  Y = -126.708
FEATURE [TechDraw::DrawProjGroupItem] ProjItem005  label="Bottom"
  CoarseView = false
  Direction = (0,-1,0)
  Focus = 100
  HardHidden = false
  IsoCount = 0
  IsoHidden = false
  IsoVisible = false
  LockPosition = false
  Perspective = false
  Rotation = 0
  RotationVector = (1,0,0)
  ScaleType = 2
  ScrubCount = 0
  SeamHidden = false
  SeamVisible = false
  SmoothHidden = false
  SmoothVisible = true
  Source = -> [Part]
  Type = 5
  X = 0
  XDirection = (0,0,-1)
  Y = -126.708
FEATURE [TechDraw::DrawProjGroup] ProjGroup001
  Anchor = -> ProjItem001
  AutoDistribute = true
  LockPosition = false
  ProjectionType = 1
  Rotation = 0
  Scale = 0.5
  ScaleType = 0
  Source = -> [Part]
  Views = -> [ProjItem001,ProjItem002,ProjItem004,ProjItem005]
  X = 216.242
  Y = 205.089
  spacingX = 15
  spacingY = 15
FEATURE [TechDraw::DrawPage] Page  label="Assembly"
  KeepUpdated = true
  NextBalloonIndex = 1
  ProjectionType = 1
  Scale = 0.5
  Template = -> Template
  Views = -> [ProjGroup001]
FEATURE [TechDraw::DrawSVGTemplate] Template005
  EditableTexts = AuthorName=Alex Anastasakis; CheckDate=2024/11/10; CreationDate=2024/11/10; DrawingNumber=2; FC-Scale=2:1; FC-Title=Large Foam Disc; SheetNumber=1 of 1; Subtitle=Course: Industrial Design for Game Hardware; SupervisorName=Alvaro Uribe Quevedo
  Height = 297
  Orientation = 1
  Template = C:/Program Files/FreeCAD 0.21/data/Mod/TechDraw/Templates/A3_LandscapeTD.svg
  Width = 420
FEATURE [TechDraw::DrawProjGroupItem] ProjItem006  label="Front002"
  CoarseView = false
  Direction = (1,0,0)
  Focus = 100
  HardHidden = false
  IsoCount = 0
  IsoHidden = false
  IsoVisible = false
  LockPosition = true
  Perspective = false
  Rotation = 0
  RotationVector = (0,0,-1)
  Scale = 2
  ScaleType = 2
  ScrubCount = 0
  SeamHidden = false
  SeamVisible = false
  SmoothHidden = false
  SmoothVisible = true
  Source = -> [Body008]
  Type = 0
  X = 0
  XDirection = (0,0,-1)
  Y = 0
FEATURE [TechDraw::DrawProjGroupItem] ProjItem007  label="Right001"
  CoarseView = false
  Direction = (1e-16,0,-1)
  Focus = 100
  HardHidden = false
  IsoCount = 0
  IsoHidden = false
  IsoVisible = false
  LockPosition = false
  Perspective = false
  Rotation = 0
  RotationVector = (1,0,0)
  Scale = 2
  ScaleType = 2
  ScrubCount = 0
  SeamHidden = false
  SeamVisible = false
  SmoothHidden = false
  SmoothVisible = true
  Source = -> [Body008]
  Type = 2
  X = 112
  XDirection = (-1,0,-1e-16)
  Y = 0
FEATURE [TechDraw::DrawProjGroup] ProjGroup002
  Anchor = -> ProjItem006
  AutoDistribute = true
  LockPosition = false
  ProjectionType = 1
  Rotation = 0
  Scale = 2
  ScaleType = 0
  Source = -> [Body008]
  Views = -> [ProjItem006,ProjItem007]
  X = 154.783
  Y = 175.756
  spacingX = 40
  spacingY = 15
FEATURE [TechDraw::DrawViewDimension] Dimension
  AngleOverride = false
  Arbitrary = false
  ArbitraryTolerances = false
  EqualTolerance = true
  ExtensionAngle = 0
  FormatSpec = ⌀%.2w
  FormatSpecOverTolerance = %+.2w
  FormatSpecUnderTolerance = %+.2w
  Inverted = false
  LineAngle = 0
  LockPosition = false
  MeasureType = 1
  OverTolerance = 0
  References2D = -> [ProjItem007]
  Rotation = 0
  Scale = 2
  ScaleType = 0
  TheoreticalExact = false
  Type = 5
  UnderTolerance = 0
  X = 74.6367
  Y = 46.6479
FEATURE [TechDraw::DrawViewDimension] Dimension001
  AngleOverride = false
  Arbitrary = false
  ArbitraryTolerances = false
  EqualTolerance = true
  ExtensionAngle = 0
  FormatSpec = %.2w
  FormatSpecOverTolerance = %+.2w
  FormatSpecUnderTolerance = %+.2w
  Inverted = false
  LineAngle = 0
  LockPosition = false
  MeasureType = 1
  OverTolerance = 0
  References2D = -> [ProjItem006]
  Rotation = 0
  Scale = 2
  ScaleType = 0
  TheoreticalExact = false
  Type = 1
  UnderTolerance = 0
  X = 1.38216
  Y = 76.6146
FEATURE [TechDraw::DrawPage] Page005  label="FoamLarge"
  KeepUpdated = true
  NextBalloonIndex = 1
  ProjectionType = 0
  Scale = 2
  Template = -> Template005
  Views = -> [ProjGroup002,Dimension,Dimension001]
FEATURE [TechDraw::DrawSVGTemplate] Template006
  EditableTexts = AuthorName=Alex Anastasakis; CheckDate=2024/11/10; CreationDate=2024/11/10; DrawingNumber=1; FC-Scale=1:1; FC-Title=Shell; SheetNumber=1 of 1; Subtitle=Course: Industrial Design for Game Hardware; SupervisorName=Alvaro Uribe Quevedo
  Height = 297
  Orientation = 1
  Template = C:/Program Files/FreeCAD 0.21/data/Mod/TechDraw/Templates/A3_LandscapeTD.svg
  Width = 420
FEATURE [TechDraw::DrawProjGroupItem] ProjItem008  label="Front003"
  CoarseView = false
  Direction = (1,0,0)
  Focus = 100
  HardHidden = false
  IsoCount = 0
  IsoHidden = false
  IsoVisible = false
  LockPosition = true
  Perspective = false
  Rotation = 0
  RotationVector = (0,0,-1)
  ScaleType = 2
  ScrubCount = 0
  SeamHidden = false
  SeamVisible = false
  SmoothHidden = false
  SmoothVisible = true
  Source = -> [Body002]
  Type = 0
  X = 0
  XDirection = (0,0,-1)
  Y = 0
FEATURE [TechDraw::DrawProjGroupItem] ProjItem011  label="Bottom001"
  CoarseView = false
  Direction = (0,-1,0)
  Focus = 100
  HardHidden = false
  IsoCount = 0
  IsoHidden = false
  IsoVisible = false
  LockPosition = false
  Perspective = false
  Rotation = 0
  RotationVector = (1,0,0)
  ScaleType = 2
  ScrubCount = 0
  SeamHidden = false
  SeamVisible = false
  SmoothHidden = false
  SmoothVisible = true
  Source = -> [Body002]
  Type = 5
  X = 0
  XDirection = (0,0,-1)
  Y = -74.9478
FEATURE [TechDraw::DrawProjGroupItem] ProjItem012  label="Right002"
  CoarseView = false
  Direction = (1e-16,0,-1)
  Focus = 100
  HardHidden = false
  IsoCount = 0
  IsoHidden = false
  IsoVisible = false
  LockPosition = false
  Perspective = false
  Rotation = 0
  RotationVector = (1,0,0)
  ScaleType = 2
  ScrubCount = 0
  SeamHidden = false
  SeamVisible = false
  SmoothHidden = false
  SmoothVisible = true
  Source = -> [Body002]
  Type = 2
  X = 113.033
  XDirection = (-1,0,-1e-16)
  Y = 0
FEATURE [TechDraw::DrawProjGroupItem] ProjItem013  label="FrontTopRight"
  CoarseView = false
  Direction = (0.57735,0.57735,-0.57735)
  Focus = 100
  HardHidden = false
  IsoCount = 0
  IsoHidden = false
  IsoVisible = false
  LockPosition = false
  Perspective = false
  Rotation = 0
  RotationVector = (1,0,0)
  ScaleType = 2
  ScrubCount = 0
  SeamHidden = false
  SeamVisible = false
  SmoothHidden = false
  SmoothVisible = true
  Source = -> [Body002]
  Type = 7
  X = 113.033
  XDirection = (-0.707107,0,-0.707107)
  Y = 90.7051
FEATURE [TechDraw::DrawProjGroup] ProjGroup003
  Anchor = -> ProjItem008
  AutoDistribute = true
  LockPosition = false
  ProjectionType = 1
  Rotation = 0
  ScaleType = 0
  Source = -> [Body002]
  Views = -> [ProjItem008,ProjItem011,ProjItem012,ProjItem013]
  X = 160.242
  Y = 137.788
  spacingX = 15
  spacingY = 15
FEATURE [TechDraw::DrawViewDimension] Dimension002
  AngleOverride = false
  Arbitrary = false
  ArbitraryTolerances = false
  EqualTolerance = true
  ExtensionAngle = 0
  FormatSpec = %.2w
  FormatSpecOverTolerance = %+.2w
  FormatSpecUnderTolerance = %+.2w
  Inverted = false
  LineAngle = 0
  LockPosition = false
  MeasureType = 1
  OverTolerance = 0
  References2D = -> [ProjItem008]
  Rotation = 0
  ScaleType = 0
  TheoreticalExact = false
  Type = 1
  UnderTolerance = 0
  X = -1.47147
  Y = 48.0454
FEATURE [TechDraw::DrawViewDimension] Dimension003
  AngleOverride = false
  Arbitrary = false
  ArbitraryTolerances = false
  EqualTolerance = true
  ExtensionAngle = 0
  FormatSpec = ⌀%.2w
  FormatSpecOverTolerance = %+.2w
  FormatSpecUnderTolerance = %+.2w
  Inverted = false
  LineAngle = 0
  LockPosition = false
  MeasureType = 1
  OverTolerance = 0
  References2D = -> [ProjItem012]
  Rotation = 0
  ScaleType = 0
  TheoreticalExact = false
  Type = 5
  UnderTolerance = 0
  X = 51.639
  Y = 24.393
FEATURE [TechDraw::DrawViewDimension] Dimension004
  AngleOverride = false
  Arbitrary = false
  ArbitraryTolerances = false
  EqualTolerance = true
  ExtensionAngle = 0
  FormatSpec = ⌀%.2w
  FormatSpecOverTolerance = %+.2w
  FormatSpecUnderTolerance = %+.2w
  Inverted = false
  LineAngle = 0
  LockPosition = false
  MeasureType = 1
  OverTolerance = 0
  References2D = -> [ProjItem012]
  Rotation = 0
  ScaleType = 0
  TheoreticalExact = false
  Type = 5
  UnderTolerance = 0
  X = 49.128
  Y = -24.1698
FEATURE [TechDraw::DrawViewDimension] Dimension005
  AngleOverride = false
  Arbitrary = false
  ArbitraryTolerances = false
  EqualTolerance = true
  ExtensionAngle = 0
  FormatSpec = %.2w
  FormatSpecOverTolerance = %+.2w
  FormatSpecUnderTolerance = %+.2w
  Inverted = false
  LineAngle = 0
  LockPosition = false
  MeasureType = 1
  OverTolerance = 0
  References2D = -> [ProjItem011]
  Rotation = 0
  ScaleType = 0
  TheoreticalExact = false
  Type = 2
  UnderTolerance = 0
  X = -63.0177
  Y = 16.6369
FEATURE [TechDraw::DrawViewDimension] Dimension006
  AngleOverride = false
  Arbitrary = false
  ArbitraryTolerances = false
  EqualTolerance = true
  ExtensionAngle = 0
  FormatSpec = ⌀%.2w
  FormatSpecOverTolerance = %+.2w
  FormatSpecUnderTolerance = %+.2w
  Inverted = false
  LineAngle = 0
  LockPosition = false
  MeasureType = 1
  OverTolerance = 0
  References2D = -> [ProjItem011]
  Rotation = 0
  ScaleType = 0
  TheoreticalExact = false
  Type = 5
  UnderTolerance = 0
  X = 59.0411
  Y = 28.2673
FEATURE [TechDraw::DrawPage] Page006  label="PVC001"
  KeepUpdated = true
  NextBalloonIndex = 1
  ProjectionType = 0
  Template = -> Template006
  Views = -> [ProjGroup003,Dimension002,Dimension003,Dimension004,Dimension005,Dimension006]
FEATURE [TechDraw::DrawSVGTemplate] Template007
  EditableTexts = Designed_by_Name=Alex Anastasakis; Drawing_number=5; FC-Date=2024/11/10; FC-SC=5:1; FC-SH=1 of 1; FC-Title=Small Foam Disc; Subtitle=Course: Industrial Design for Game Hardware
  Height = 210
  Orientation = 1
  Template = C:/Program Files/FreeCAD 0.21/data/Mod/TechDraw/Templates/A4_LandscapeTD.svg
  Width = 297
FEATURE [TechDraw::DrawProjGroupItem] ProjItem014  label="Front004"
  CoarseView = false
  Direction = (1,0,0)
  Focus = 100
  HardHidden = false
  IsoCount = 0
  IsoHidden = false
  IsoVisible = false
  LockPosition = true
  Perspective = false
  Rotation = 0
  RotationVector = (0,0,-1)
  Scale = 5
  ScaleType = 2
  ScrubCount = 0
  SeamHidden = false
  SeamVisible = false
  SmoothHidden = false
  SmoothVisible = true
  Source = -> [Body011]
  Type = 0
  X = 0
  XDirection = (0,0,-1)
  Y = 0
FEATURE [TechDraw::DrawProjGroupItem] ProjItem015  label="Top"
  CoarseView = false
  Direction = (0,1,0)
  Focus = 100
  HardHidden = false
  IsoCount = 0
  IsoHidden = false
  IsoVisible = false
  LockPosition = false
  Perspective = false
  Rotation = 0
  RotationVector = (1,0,0)
  Scale = 5
  ScaleType = 2
  ScrubCount = 0
  SeamHidden = false
  SeamVisible = false
  SmoothHidden = false
  SmoothVisible = true
  Source = -> [Body011]
  Type = 4
  X = 0
  XDirection = (0,0,-1)
  Y = 47.5
FEATURE [TechDraw::DrawProjGroup] ProjGroup004
  Anchor = -> ProjItem014
  AutoDistribute = true
  LockPosition = false
  ProjectionType = 1
  Rotation = 0
  Scale = 5
  ScaleType = 0
  Source = -> [Body011]
  Views = -> [ProjItem014,ProjItem015]
  X = 141.061
  Y = 94.4418
  spacingX = 15
  spacingY = 15
FEATURE [TechDraw::DrawViewDimension] Dimension007
  AngleOverride = false
  Arbitrary = false
  ArbitraryTolerances = false
  EqualTolerance = true
  ExtensionAngle = 0
  FormatSpec = %.2w
  FormatSpecOverTolerance = %+.2w
  FormatSpecUnderTolerance = %+.2w
  Inverted = false
  LineAngle = 0
  LockPosition = false
  MeasureType = 1
  OverTolerance = 0
  References2D = -> [ProjItem014]
  Rotation = 0
  Scale = 5
  ScaleType = 0
  TheoreticalExact = false
  Type = 2
  UnderTolerance = 0
  X = 37.7178
  Y = -16.9366
FEATURE [TechDraw::DrawViewDimension] Dimension008
  AngleOverride = false
  Arbitrary = false
  ArbitraryTolerances = false
  EqualTolerance = true
  ExtensionAngle = 0
  FormatSpec = ⌀%.2w
  FormatSpecOverTolerance = %+.2w
  FormatSpecUnderTolerance = %+.2w
  Inverted = false
  LineAngle = 0
  LockPosition = false
  MeasureType = 1
  OverTolerance = 0
  References2D = -> [ProjItem015]
  Rotation = 0
  Scale = 5
  ScaleType = 0
  TheoreticalExact = false
  Type = 5
  UnderTolerance = 0
  X = 44.1524
  Y = 19.9166
FEATURE [TechDraw::DrawPage] Page007  label="FoamSmall"
  KeepUpdated = true
  NextBalloonIndex = 1
  ProjectionType = 0
  Scale = 5
  Template = -> Template007
  Views = -> [ProjGroup004,Dimension007,Dimension008]
FEATURE [TechDraw::DrawSVGTemplate] Template008
  EditableTexts = AuthorName=Alex Anastasakis; CheckDate=2024/11/10; CreationDate=2024/11/10; DrawingNumber=8; FC-Scale=1:1; FC-Title=Handle; SheetNumber=1 of 1; Subtitle=Course: Industrial Design for Game Hardware; SupervisorName=Alvaro Uribe Quevedo
  Height = 297
  Orientation = 1
  Template = C:/Program Files/FreeCAD 0.21/data/Mod/TechDraw/Templates/A3_LandscapeTD.svg
  Width = 420
FEATURE [TechDraw::DrawProjGroupItem] ProjItem016  label="Front005"
  CoarseView = false
  Direction = (1,0,0)
  Focus = 100
  HardHidden = false
  IsoCount = 0
  IsoHidden = false
  IsoVisible = false
  LockPosition = true
  Perspective = false
  Rotation = 0
  RotationVector = (0,0,-1)
  ScaleType = 2
  ScrubCount = 0
  SeamHidden = false
  SeamVisible = false
  SmoothHidden = false
  SmoothVisible = true
  Source = -> [Body003]
  Type = 0
  X = 0
  XDirection = (0,0,-1)
  Y = 0
FEATURE [TechDraw::DrawProjGroupItem] ProjItem017  label="Right003"
  CoarseView = false
  Direction = (1e-16,0,-1)
  Focus = 100
  HardHidden = false
  IsoCount = 0
  IsoHidden = false
  IsoVisible = false
  LockPosition = false
  Perspective = false
  Rotation = 0
  RotationVector = (1,0,0)
  ScaleType = 2
  ScrubCount = 0
  SeamHidden = false
  SeamVisible = false
  SmoothHidden = false
  SmoothVisible = true
  Source = -> [Body003]
  Type = 2
  X = 51.25
  XDirection = (-1,0,-1e-16)
  Y = 0
FEATURE [TechDraw::DrawProjGroupItem] ProjItem018  label="Top004"
  Caption = See detail 1
  CoarseView = false
  Direction = (0,1,0)
  Focus = 100
  HardHidden = false
  IsoCount = 0
  IsoHidden = false
  IsoVisible = false
  LockPosition = false
  Perspective = false
  Rotation = 0
  RotationVector = (1,0,0)
  ScaleType = 2
  ScrubCount = 0
  SeamHidden = false
  SeamVisible = false
  SmoothHidden = false
  SmoothVisible = true
  Source = -> [Body003]
  Type = 4
  X = 0
  XDirection = (0,0,-1)
  Y = 125.625
FEATURE [TechDraw::DrawProjGroup] ProjGroup005
  Anchor = -> ProjItem016
  AutoDistribute = true
  LockPosition = false
  ProjectionType = 1
  Rotation = 0
  ScaleType = 0
  Source = -> [Body003]
  Views = -> [ProjItem016,ProjItem017,ProjItem018]
  X = 129.996
  Y = 125.78
  spacingX = 30
  spacingY = 15
FEATURE [TechDraw::DrawViewDimension] Dimension009
  AngleOverride = false
  Arbitrary = false
  ArbitraryTolerances = false
  EqualTolerance = true
  ExtensionAngle = 0
  FormatSpec = ⌀%.2w
  FormatSpecOverTolerance = %+.2w
  FormatSpecUnderTolerance = %+.2w
  Inverted = false
  LineAngle = 0
  LockPosition = false
  MeasureType = 1
  OverTolerance = 0
  References2D = -> [ProjItem018]
  Rotation = 0
  ScaleType = 0
  TheoreticalExact = false
  Type = 5
  UnderTolerance = 0
  X = 29.8241
  Y = 14.7041
FEATURE [TechDraw::DrawViewDetail] Detail  label="Detail 1"
  AnchorPoint = (8.47,-5.65,0)
  BaseView = -> ProjItem018
  Caption = Scale 10:1
  CoarseView = false
  Direction = (0,1,0)
  Focus = 100
  HardHidden = false
  IsoCount = 0
  IsoHidden = false
  IsoVisible = false
  LockPosition = false
  Perspective = false
  Radius = 2
  Reference = 1
  Rotation = 0
  Scale = 10
  ScaleType = 2
  ScrubCount = 0
  SeamHidden = false
  SeamVisible = false
  SmoothHidden = false
  SmoothVisible = true
  Source = -> [Body003]
  X = 61.6586
  XDirection = (0,0,-1)
  Y = 237.415
FEATURE [TechDraw::DrawViewDimension] Dimension010
  AngleOverride = false
  Arbitrary = false
  ArbitraryTolerances = false
  EqualTolerance = true
  ExtensionAngle = 0
  FormatSpec = %.2w
  FormatSpecOverTolerance = %+.2w
  FormatSpecUnderTolerance = %+.2w
  Inverted = false
  LineAngle = 0
  LockPosition = false
  MeasureType = 1
  OverTolerance = 0
  References2D = -> [Detail]
  Rotation = 0
  ScaleType = 0
  TheoreticalExact = false
  Type = 0
  UnderTolerance = 0
  X = -30.562
  Y = -15.8848
FEATURE [TechDraw::DrawViewDimension] Dimension011
  AngleOverride = false
  Arbitrary = false
  ArbitraryTolerances = false
  EqualTolerance = true
  ExtensionAngle = 0
  FormatSpec = ⌀%.2w
  FormatSpecOverTolerance = %+.2w
  FormatSpecUnderTolerance = %+.2w
  Inverted = false
  LineAngle = 0
  LockPosition = false
  MeasureType = 1
  OverTolerance = 0
  References2D = -> [ProjItem017]
  Rotation = 0
  ScaleType = 0
  TheoreticalExact = false
  Type = 5
  UnderTolerance = 0
  X = -25.8773
  Y = 66.7435
FEATURE [TechDraw::DrawViewDimension] Dimension012
  AngleOverride = false
  Arbitrary = false
  ArbitraryTolerances = false
  EqualTolerance = true
  ExtensionAngle = 0
  FormatSpec = %.2w
  FormatSpecOverTolerance = %+.2w
  FormatSpecUnderTolerance = %+.2w
  Inverted = false
  LineAngle = 0
  LockPosition = false
  MeasureType = 1
  OverTolerance = 0
  References2D = -> [ProjItem017]
  Rotation = 0
  ScaleType = 0
  TheoreticalExact = false
  Type = 1
  UnderTolerance = 0
  X = -13.1244
  Y = 115.629
FEATURE [TechDraw::DrawViewDimension] Dimension013
  AngleOverride = false
  Arbitrary = false
  ArbitraryTolerances = false
  EqualTolerance = true
  ExtensionAngle = 0
  FormatSpec = %.2w
  FormatSpecOverTolerance = %+.2w
  FormatSpecUnderTolerance = %+.2w
  Inverted = false
  LineAngle = 0
  LockPosition = false
  MeasureType = 1
  OverTolerance = 0
  References2D = -> [ProjItem017]
  Rotation = 0
  ScaleType = 0
  TheoreticalExact = false
  Type = 2
  UnderTolerance = 0
  X = 19.7503
  Y = 116.456
FEATURE [TechDraw::DrawViewDimension] Dimension014
  AngleOverride = false
  Arbitrary = false
  ArbitraryTolerances = false
  EqualTolerance = true
  ExtensionAngle = 0
  FormatSpec = %.2w
  FormatSpecOverTolerance = %+.2w
  FormatSpecUnderTolerance = %+.2w
  Inverted = false
  LineAngle = 0
  LockPosition = false
  MeasureType = 1
  OverTolerance = 0
  References2D = -> [ProjItem017]
  Rotation = 0
  ScaleType = 0
  TheoreticalExact = false
  Type = 2
  UnderTolerance = 0
  X = 39.4426
  Y = 76.8949
FEATURE [TechDraw::DrawViewDimension] Dimension015
  AngleOverride = false
  Arbitrary = false
  ArbitraryTolerances = false
  EqualTolerance = true
  ExtensionAngle = 0
  FormatSpec = %.2w
  FormatSpecOverTolerance = %+.2w
  FormatSpecUnderTolerance = %+.2w
  Inverted = false
  LineAngle = 0
  LockPosition = false
  MeasureType = 1
  OverTolerance = 0
  References2D = -> [ProjItem016]
  Rotation = 0
  ScaleType = 0
  TheoreticalExact = false
  Type = 2
  UnderTolerance = 0
  X = -28.9334
  Y = 2.82287
FEATURE [TechDraw::DrawPage] Page008  label="Handle001"
  KeepUpdated = true
  NextBalloonIndex = 1
  ProjectionType = 0
  Template = -> Template008
  Views = -> [ProjGroup005,Dimension009,Detail,Dimension010,Dimension011,Dimension012,Dimension013,Dimension014,Dimension015]
FEATURE [TechDraw::DrawSVGTemplate] Template009
  EditableTexts = Designed_by_Name=Alex Anastasakis; Drawing_number=10; FC-Date=2024/11/10; FC-SC=3:1; FC-SH=1 of 1; FC-Title=Spring Plate; Subtitle=Course: Industrial Design for Game Hardware
  Height = 210
  Orientation = 1
  Template = C:/Program Files/FreeCAD 0.21/data/Mod/TechDraw/Templates/A4_LandscapeTD.svg
  Width = 297
FEATURE [TechDraw::DrawProjGroupItem] ProjItem019  label="Front006"
  CoarseView = false
  Direction = (1,0,0)
  Focus = 100
  HardHidden = false
  IsoCount = 0
  IsoHidden = false
  IsoVisible = false
  LockPosition = true
  Perspective = false
  Rotation = 0
  RotationVector = (0,0,-1)
  Scale = 3
  ScaleType = 2
  ScrubCount = 0
  SeamHidden = false
  SeamVisible = false
  SmoothHidden = false
  SmoothVisible = true
  Source = -> [Body010]
  Type = 0
  X = 0
  XDirection = (0,0,-1)
  Y = 0
FEATURE [TechDraw::DrawProjGroupItem] ProjItem020  label="Top005"
  CoarseView = false
  Direction = (0,1,0)
  Focus = 100
  HardHidden = false
  IsoCount = 0
  IsoHidden = false
  IsoVisible = false
  LockPosition = false
  Perspective = false
  Rotation = 0
  RotationVector = (1,0,0)
  Scale = 3
  ScaleType = 2
  ScrubCount = 0
  SeamHidden = false
  SeamVisible = false
  SmoothHidden = false
  SmoothVisible = true
  Source = -> [Body010]
  Type = 4
  X = 0
  XDirection = (0,0,-1)
  Y = 83.7
FEATURE [TechDraw::DrawProjGroup] ProjGroup006
  Anchor = -> ProjItem019
  AutoDistribute = true
  LockPosition = false
  ProjectionType = 1
  Rotation = 0
  Scale = 3
  ScaleType = 0
  Source = -> [Body010]
  Views = -> [ProjItem019,ProjItem020]
  X = 102.089
  Y = 31.4095
  spacingX = 15
  spacingY = 15
FEATURE [TechDraw::DrawViewDimension] Dimension016
  AngleOverride = false
  Arbitrary = false
  ArbitraryTolerances = false
  EqualTolerance = true
  ExtensionAngle = 0
  FormatSpec = %.2w
  FormatSpecOverTolerance = %+.2w
  FormatSpecUnderTolerance = %+.2w
  Inverted = false
  LineAngle = 0
  LockPosition = false
  MeasureType = 1
  OverTolerance = 0
  References2D = -> [ProjItem020]
  Rotation = 0
  Scale = 3
  ScaleType = 0
  TheoreticalExact = false
  Type = 2
  UnderTolerance = 0
  X = -40.7171
  Y = 4.49762
FEATURE [TechDraw::DrawViewDimension] Dimension017
  AngleOverride = false
  Arbitrary = false
  ArbitraryTolerances = false
  EqualTolerance = true
  ExtensionAngle = 0
  FormatSpec = %.2w
  FormatSpecOverTolerance = %+.2w
  FormatSpecUnderTolerance = %+.2w
  Inverted = false
  LineAngle = 0
  LockPosition = false
  MeasureType = 1
  OverTolerance = 0
  References2D = -> [ProjItem019]
  Rotation = 0
  Scale = 3
  ScaleType = 0
  TheoreticalExact = false
  Type = 2
  UnderTolerance = 0
  X = -40.9879
  Y = -7.10956
FEATURE [TechDraw::DrawViewDimension] Dimension018
  AngleOverride = false
  Arbitrary = false
  ArbitraryTolerances = false
  EqualTolerance = true
  ExtensionAngle = 0
  FormatSpec = %.2w
  FormatSpecOverTolerance = %+.2w
  FormatSpecUnderTolerance = %+.2w
  Inverted = false
  LineAngle = 0
  LockPosition = false
  MeasureType = 1
  OverTolerance = 0
  References2D = -> [ProjItem020]
  Rotation = 0
  Scale = 3
  ScaleType = 0
  TheoreticalExact = false
  Type = 1
  UnderTolerance = 0
  X = 0
  Y = 80.5098
FEATURE [TechDraw::DrawPage] Page009  label="Shimstock"
  KeepUpdated = true
  NextBalloonIndex = 1
  ProjectionType = 0
  Scale = 3
  Template = -> Template009
  Views = -> [ProjGroup006,Dimension016,Dimension017,Dimension018]
